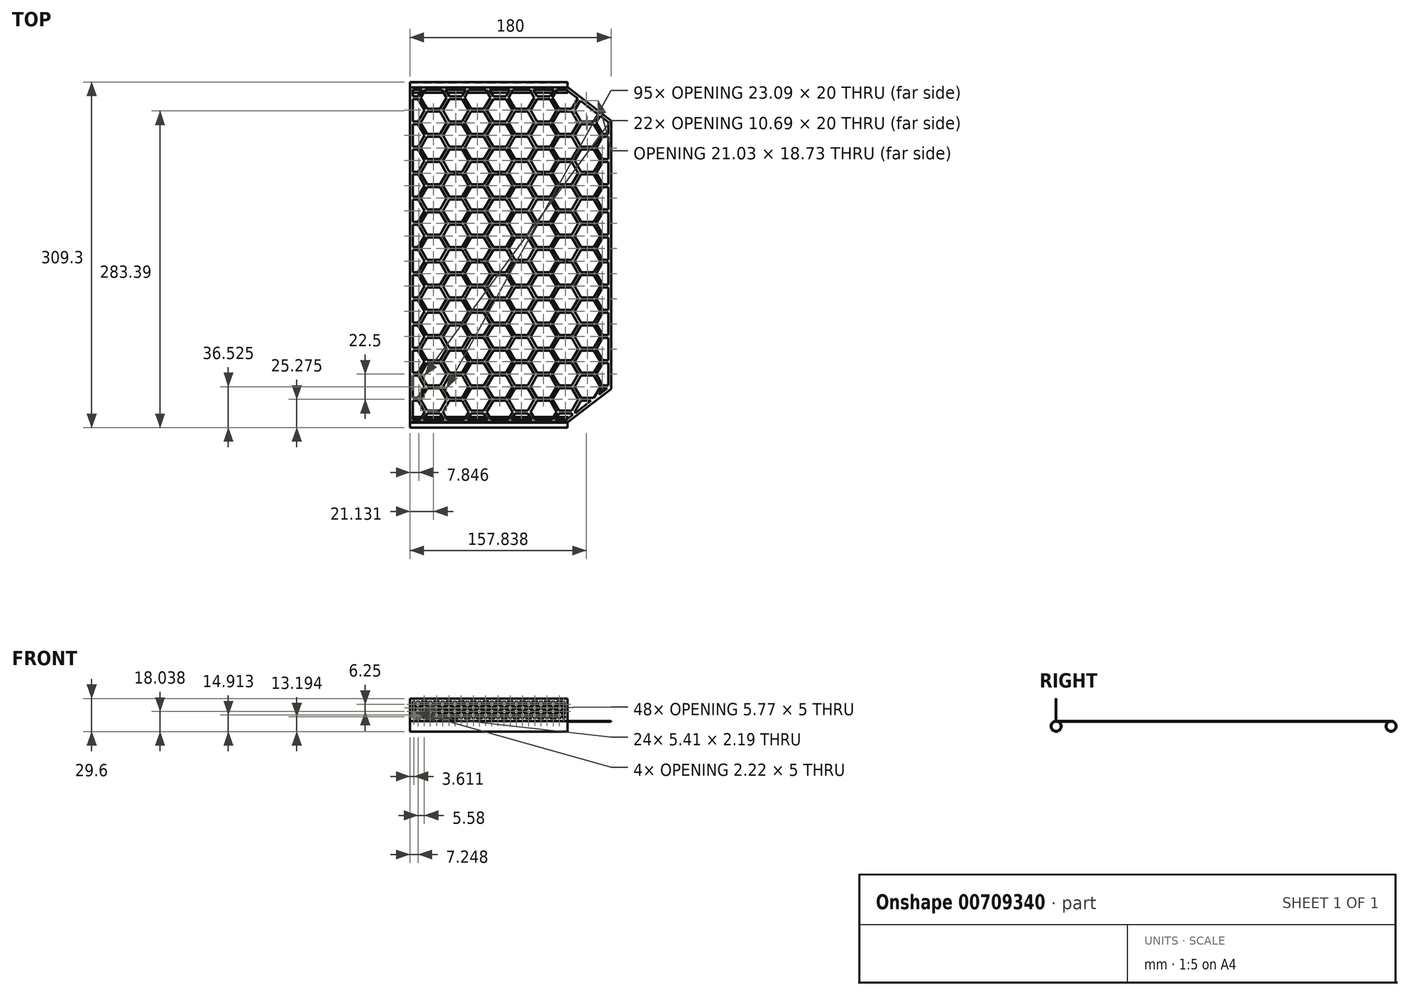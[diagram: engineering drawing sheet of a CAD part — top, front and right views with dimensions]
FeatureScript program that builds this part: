
annotation { "Feature Type Name" : "Feature", "Feature Type Description" : "" }
export const myFeature = defineFeature(function(context is Context, id is Id, definition is map)
    precondition{}
    {
        {
            var Q0;
            Q0=qCreatedBy(makeId("Top.planeOp"),FACE);
            var sketch = newSketch(context, id + "F0", { "sketchPlane" : qUnion([Q0])});
            skLineSegment(sketch, "E0.bottom", {"start": v(90, -150) * mm, "end": v(-90, -150) * mm});
            skLineSegment(sketch, "E0.top", {"start": v(90, 150) * mm, "end": v(-90, 150) * mm});
            skLineSegment(sketch, "E0.left", {"start": v(90, -150) * mm, "end": v(90, 150) * mm});
            skLineSegment(sketch, "E0.right", {"start": v(-90, -150) * mm, "end": v(-90, 150) * mm});
            skPoint(sketch, "E0.middle", {"position": v(0, 0) * mm});
            skLineSegment(sketch, "E1", {"start": v(90, -120) * mm, "end": v(51, -150) * mm});
            skLineSegment(sketch, "E2", {"start": v(51, 150) * mm, "end": v(90, 120) * mm});
            skSolve(sketch);
        }
        {
            var Q0;
            {var subQ0=sQuery(id+"F0.wireOp",EDGE,"E0.right");Q0=makeQuery(id+"F0.imprint","IMPRINT",FACE,{"disambiguationData":[TD([[makeQuery(id+"F0.imprint","IMPRINT",EDGE,{"derivedFrom":subQ0}),-1.0]])]});}
            extrude(context, id + "F1", {"entities" : qUnion([Q0]), "endBound" : BoundingType.SYMMETRIC, "depth" : 0.6 * mm, "offsetDistance" : 25 * mm});
        }
        {
            var Q0;
            Q0=qCreatedBy(makeId("Right.planeOp"),FACE);
            var sketch = newSketch(context, id + "F2", { "sketchPlane" : qUnion([Q0])});
            skCircle(sketch, "E3", {"center": v(-149.85, -4.5) * mm, "radius": 4.2 * mm});
            skCircle(sketch, "E4", {"center": v(-149.85, -4.5) * mm, "radius": 4.8 * mm});
            skCircle(sketch, "E5.MirrorC", {"center": v(149.85, -4.5) * mm, "radius": 4.8 * mm});
            skCircle(sketch, "E6.MirrorC", {"center": v(149.85, -4.5) * mm, "radius": 4.2 * mm});
            skLineSegment(sketch, "E7.bottom", {"start": v(-150.3, 0.3) * mm, "end": v(-149.7, 0.3) * mm});
            skLineSegment(sketch, "E7.top", {"start": v(-150.3, 20.3) * mm, "end": v(-149.7, 20.3) * mm});
            skLineSegment(sketch, "E7.left", {"start": v(-150.3, 0.3) * mm, "end": v(-150.3, 20.3) * mm});
            skLineSegment(sketch, "E7.right", {"start": v(-149.7, 0.3) * mm, "end": v(-149.7, 20.3) * mm});
            skPoint(sketch, "E8", {"position": v(-150, 0.3) * mm});
            skLineSegment(sketch, "E9.0.1", {"start": v(-150, -0.3) * mm, "end": v(-150, 0.3) * mm});
            skLineSegment(sketch, "E9.0.3", {"start": v(-150, 0.3) * mm, "end": v(-150, -0.3) * mm, "construction": true});
            skSolve(sketch);
        }
        {
            var Q0;
            Q0=qSketchRegion(id+"F2",true);
            var Q1;
            Q1=makeQuery(id+"F1.opExtrude","CAP_EDGE",EDGE,{"disambiguationData":[OSD([sQuery(id+"F0.wireOp",EDGE,"E0.bottom")])],"isStart":false});
            sweep(context, id + "F3", {"operationType" : NewBodyOperationType.ADD, "profiles" : qUnion([Q0]), "path" : qUnion([Q1])});
        }
        {
            var Q0;
            Q0=makeQuery(id+"F1.opExtrude","CAP_FACE",FACE,{"disambiguationData":[OSD([sQuery(id+"F0.wireOp",EDGE,"E0.bottom"),sQuery(id+"F0.wireOp",EDGE,"E0.top"),sQuery(id+"F0.wireOp",EDGE,"E0.left"),sQuery(id+"F0.wireOp",EDGE,"E0.right")])],"isStart":false});
            var sketch = newSketch(context, id + "F4", { "sketchPlane" : qUnion([Q0])});
            skPoint(sketch, "E10.0", {"position": v(-90, 147.52) * mm});
            skPoint(sketch, "E11.0", {"position": v(-90, -147.52) * mm});
            skLineSegment(sketch, "E12", {"start": v(-90, 147.52) * mm, "end": v(90, 147.52) * mm});
            skLineSegment(sketch, "E13", {"start": v(-90, -147.52) * mm, "end": v(90, -147.52) * mm});
            skCircle(sketch, "E14.cCircle", {"center": v(-68.87, 163.12) * mm, "radius": 10 * mm, "construction": true});
            skLineSegment(sketch, "E14.0", {"start": v(-63.1, 153.12) * mm, "end": v(-74.64, 153.12) * mm});
            skLineSegment(sketch, "E14.1", {"start": v(-74.64, 153.12) * mm, "end": v(-80.42, 163.12) * mm});
            skLineSegment(sketch, "E14.2", {"start": v(-80.42, 163.12) * mm, "end": v(-74.64, 173.12) * mm});
            skLineSegment(sketch, "E14.3", {"start": v(-74.64, 173.12) * mm, "end": v(-63.1, 173.12) * mm});
            skLineSegment(sketch, "E14.4", {"start": v(-63.1, 173.12) * mm, "end": v(-57.32, 163.12) * mm});
            skLineSegment(sketch, "E14.5", {"start": v(-57.32, 163.12) * mm, "end": v(-63.1, 153.12) * mm});
            skPoint(sketch, "E14.0.midPoint", {"position": v(-68.87, 153.12) * mm});
            skCircle(sketch, "E15.cCircle", {"center": v(-88.35, 151.87) * mm, "radius": 10 * mm, "construction": true});
            skLineSegment(sketch, "E15.0", {"start": v(-82.58, 141.87) * mm, "end": v(-94.13, 141.87) * mm});
            skLineSegment(sketch, "E15.1", {"start": v(-94.13, 141.87) * mm, "end": v(-99.9, 151.87) * mm});
            skLineSegment(sketch, "E15.2", {"start": v(-99.9, 151.87) * mm, "end": v(-94.13, 161.87) * mm});
            skLineSegment(sketch, "E15.3", {"start": v(-94.13, 161.87) * mm, "end": v(-82.58, 161.87) * mm});
            skLineSegment(sketch, "E15.4", {"start": v(-82.58, 161.87) * mm, "end": v(-76.8, 151.87) * mm});
            skLineSegment(sketch, "E15.5", {"start": v(-76.8, 151.87) * mm, "end": v(-82.58, 141.87) * mm});
            skPoint(sketch, "E15.0.midPoint", {"position": v(-88.35, 141.87) * mm});
            skLineSegment(sketch, "E16.0", {"start": v(87.5, -149.7) * mm, "end": v(87.5, 149.7) * mm});
            skLineSegment(sketch, "E17.0", {"start": v(-87.5, -149.7) * mm, "end": v(-87.5, 149.7) * mm});
            skLineSegment(sketch, "E18", {"start": v(0, 147.52) * mm, "end": v(0, -147.52) * mm, "construction": true});
            skLineSegment(sketch, "E19", {"start": v(-87.5, 0) * mm, "end": v(87.5, 0) * mm, "construction": true});
            skLineSegment(sketch, "E20.0.1.0", {"start": v(-94.13, 139.37) * mm, "end": v(-82.58, 139.37) * mm});
            skLineSegment(sketch, "E20.0.1.1", {"start": v(-99.9, 129.37) * mm, "end": v(-94.13, 139.37) * mm});
            skLineSegment(sketch, "E20.0.1.2", {"start": v(-94.13, 119.37) * mm, "end": v(-99.9, 129.37) * mm});
            skLineSegment(sketch, "E20.0.1.3", {"start": v(-82.58, 119.37) * mm, "end": v(-94.13, 119.37) * mm});
            skLineSegment(sketch, "E20.0.1.4", {"start": v(-76.8, 129.37) * mm, "end": v(-82.58, 119.37) * mm});
            skLineSegment(sketch, "E20.0.1.5", {"start": v(-82.58, 139.37) * mm, "end": v(-76.8, 129.37) * mm});
            skLineSegment(sketch, "E20.0.1.6", {"start": v(-80.42, 140.62) * mm, "end": v(-74.64, 150.62) * mm});
            skLineSegment(sketch, "E20.0.1.7", {"start": v(-74.64, 130.62) * mm, "end": v(-80.42, 140.62) * mm});
            skLineSegment(sketch, "E20.0.1.8", {"start": v(-74.64, 150.62) * mm, "end": v(-63.1, 150.62) * mm});
            skLineSegment(sketch, "E20.0.1.9", {"start": v(-63.1, 150.62) * mm, "end": v(-57.32, 140.62) * mm});
            skLineSegment(sketch, "E20.0.1.10", {"start": v(-57.32, 140.62) * mm, "end": v(-63.1, 130.62) * mm});
            skLineSegment(sketch, "E20.0.1.11", {"start": v(-63.1, 130.62) * mm, "end": v(-74.64, 130.62) * mm});
            skLineSegment(sketch, "E20.1.0.0", {"start": v(-54.82, 161.87) * mm, "end": v(-43.28, 161.87) * mm});
            skLineSegment(sketch, "E20.1.0.1", {"start": v(-60.6, 151.87) * mm, "end": v(-54.82, 161.87) * mm});
            skLineSegment(sketch, "E20.1.0.2", {"start": v(-54.82, 141.87) * mm, "end": v(-60.6, 151.87) * mm});
            skLineSegment(sketch, "E20.1.0.3", {"start": v(-43.28, 141.87) * mm, "end": v(-54.82, 141.87) * mm});
            skLineSegment(sketch, "E20.1.0.4", {"start": v(-37.5, 151.87) * mm, "end": v(-43.28, 141.87) * mm});
            skLineSegment(sketch, "E20.1.0.5", {"start": v(-43.28, 161.87) * mm, "end": v(-37.5, 151.87) * mm});
            skLineSegment(sketch, "E20.1.0.6", {"start": v(-41.11, 163.12) * mm, "end": v(-35.34, 173.12) * mm});
            skLineSegment(sketch, "E20.1.0.7", {"start": v(-35.34, 153.12) * mm, "end": v(-41.11, 163.12) * mm});
            skLineSegment(sketch, "E20.1.0.8", {"start": v(-35.34, 173.12) * mm, "end": v(-23.79, 173.12) * mm});
            skLineSegment(sketch, "E20.1.0.9", {"start": v(-23.79, 173.12) * mm, "end": v(-18.02, 163.12) * mm});
            skLineSegment(sketch, "E20.1.0.10", {"start": v(-18.02, 163.12) * mm, "end": v(-23.79, 153.12) * mm});
            skLineSegment(sketch, "E20.1.0.11", {"start": v(-23.79, 153.12) * mm, "end": v(-35.34, 153.12) * mm});
            skLineSegment(sketch, "E20.1.1.0", {"start": v(-54.82, 139.37) * mm, "end": v(-43.28, 139.37) * mm});
            skLineSegment(sketch, "E20.1.1.1", {"start": v(-60.6, 129.37) * mm, "end": v(-54.82, 139.37) * mm});
            skLineSegment(sketch, "E20.1.1.2", {"start": v(-54.82, 119.37) * mm, "end": v(-60.6, 129.37) * mm});
            skLineSegment(sketch, "E20.1.1.3", {"start": v(-43.28, 119.37) * mm, "end": v(-54.82, 119.37) * mm});
            skLineSegment(sketch, "E20.1.1.4", {"start": v(-37.5, 129.37) * mm, "end": v(-43.28, 119.37) * mm});
            skLineSegment(sketch, "E20.1.1.5", {"start": v(-43.28, 139.37) * mm, "end": v(-37.5, 129.37) * mm});
            skLineSegment(sketch, "E20.1.1.6", {"start": v(-41.11, 140.62) * mm, "end": v(-35.34, 150.62) * mm});
            skLineSegment(sketch, "E20.1.1.7", {"start": v(-35.34, 130.62) * mm, "end": v(-41.11, 140.62) * mm});
            skLineSegment(sketch, "E20.1.1.8", {"start": v(-35.34, 150.62) * mm, "end": v(-23.79, 150.62) * mm});
            skLineSegment(sketch, "E20.1.1.9", {"start": v(-23.79, 150.62) * mm, "end": v(-18.02, 140.62) * mm});
            skLineSegment(sketch, "E20.1.1.10", {"start": v(-18.02, 140.62) * mm, "end": v(-23.79, 130.62) * mm});
            skLineSegment(sketch, "E20.1.1.11", {"start": v(-23.79, 130.62) * mm, "end": v(-35.34, 130.62) * mm});
            skLineSegment(sketch, "E20.2.0.0", {"start": v(-15.52, 161.87) * mm, "end": v(-3.97, 161.87) * mm});
            skLineSegment(sketch, "E20.2.0.1", {"start": v(-21.29, 151.87) * mm, "end": v(-15.52, 161.87) * mm});
            skLineSegment(sketch, "E20.2.0.2", {"start": v(-15.52, 141.87) * mm, "end": v(-21.29, 151.87) * mm});
            skLineSegment(sketch, "E20.2.0.3", {"start": v(-3.97, 141.87) * mm, "end": v(-15.52, 141.87) * mm});
            skLineSegment(sketch, "E20.2.0.4", {"start": v(1.8, 151.87) * mm, "end": v(-3.97, 141.87) * mm});
            skLineSegment(sketch, "E20.2.0.5", {"start": v(-3.97, 161.87) * mm, "end": v(1.8, 151.87) * mm});
            skLineSegment(sketch, "E20.2.0.6", {"start": v(-1.8, 163.12) * mm, "end": v(3.97, 173.12) * mm});
            skLineSegment(sketch, "E20.2.0.7", {"start": v(3.97, 153.12) * mm, "end": v(-1.8, 163.12) * mm});
            skLineSegment(sketch, "E20.2.0.8", {"start": v(3.97, 173.12) * mm, "end": v(15.52, 173.12) * mm});
            skLineSegment(sketch, "E20.2.0.9", {"start": v(15.52, 173.12) * mm, "end": v(21.29, 163.12) * mm});
            skLineSegment(sketch, "E20.2.0.10", {"start": v(21.29, 163.12) * mm, "end": v(15.52, 153.12) * mm});
            skLineSegment(sketch, "E20.2.0.11", {"start": v(15.52, 153.12) * mm, "end": v(3.97, 153.12) * mm});
            skLineSegment(sketch, "E20.2.1.0", {"start": v(-15.52, 139.37) * mm, "end": v(-3.97, 139.37) * mm});
            skLineSegment(sketch, "E20.2.1.1", {"start": v(-21.29, 129.37) * mm, "end": v(-15.52, 139.37) * mm});
            skLineSegment(sketch, "E20.2.1.2", {"start": v(-15.52, 119.37) * mm, "end": v(-21.29, 129.37) * mm});
            skLineSegment(sketch, "E20.2.1.3", {"start": v(-3.97, 119.37) * mm, "end": v(-15.52, 119.37) * mm});
            skLineSegment(sketch, "E20.2.1.4", {"start": v(1.8, 129.37) * mm, "end": v(-3.97, 119.37) * mm});
            skLineSegment(sketch, "E20.2.1.5", {"start": v(-3.97, 139.37) * mm, "end": v(1.8, 129.37) * mm});
            skLineSegment(sketch, "E20.2.1.6", {"start": v(-1.8, 140.62) * mm, "end": v(3.97, 150.62) * mm});
            skLineSegment(sketch, "E20.2.1.7", {"start": v(3.97, 130.62) * mm, "end": v(-1.8, 140.62) * mm});
            skLineSegment(sketch, "E20.2.1.8", {"start": v(3.97, 150.62) * mm, "end": v(15.52, 150.62) * mm});
            skLineSegment(sketch, "E20.2.1.9", {"start": v(15.52, 150.62) * mm, "end": v(21.29, 140.62) * mm});
            skLineSegment(sketch, "E20.2.1.10", {"start": v(21.29, 140.62) * mm, "end": v(15.52, 130.62) * mm});
            skLineSegment(sketch, "E20.2.1.11", {"start": v(15.52, 130.62) * mm, "end": v(3.97, 130.62) * mm});
            skLineSegment(sketch, "E20.direction1", {"start": v(-94.13, 161.87) * mm, "end": v(-54.82, 161.87) * mm, "construction": true});
            skLineSegment(sketch, "E20.direction2", {"start": v(-94.13, 161.87) * mm, "end": v(-94.13, 139.37) * mm, "construction": true});
            skLineSegment(sketch, "E21.0.3.0", {"start": v(23.79, 161.87) * mm, "end": v(35.34, 161.87) * mm});
            skLineSegment(sketch, "E21.3.3.0", {"start": v(18.02, 151.87) * mm, "end": v(23.79, 161.87) * mm});
            skLineSegment(sketch, "E21.6.3.0", {"start": v(23.79, 141.87) * mm, "end": v(18.02, 151.87) * mm});
            skLineSegment(sketch, "E21.9.3.0", {"start": v(35.34, 141.87) * mm, "end": v(23.79, 141.87) * mm});
            skLineSegment(sketch, "E21.12.3.0", {"start": v(41.11, 151.87) * mm, "end": v(35.34, 141.87) * mm});
            skLineSegment(sketch, "E21.15.3.0", {"start": v(35.34, 161.87) * mm, "end": v(41.11, 151.87) * mm});
            skLineSegment(sketch, "E21.18.3.0", {"start": v(37.5, 163.12) * mm, "end": v(43.28, 173.12) * mm});
            skLineSegment(sketch, "E21.21.3.0", {"start": v(43.28, 153.12) * mm, "end": v(37.5, 163.12) * mm});
            skLineSegment(sketch, "E21.24.3.0", {"start": v(43.28, 173.12) * mm, "end": v(54.82, 173.12) * mm});
            skLineSegment(sketch, "E21.27.3.0", {"start": v(54.82, 173.12) * mm, "end": v(60.6, 163.12) * mm});
            skLineSegment(sketch, "E21.30.3.0", {"start": v(60.6, 163.12) * mm, "end": v(54.82, 153.12) * mm});
            skLineSegment(sketch, "E21.33.3.0", {"start": v(54.82, 153.12) * mm, "end": v(43.28, 153.12) * mm});
            skLineSegment(sketch, "E21.0.3.1", {"start": v(23.79, 139.37) * mm, "end": v(35.34, 139.37) * mm});
            skLineSegment(sketch, "E21.3.3.1", {"start": v(18.02, 129.37) * mm, "end": v(23.79, 139.37) * mm});
            skLineSegment(sketch, "E21.6.3.1", {"start": v(23.79, 119.37) * mm, "end": v(18.02, 129.37) * mm});
            skLineSegment(sketch, "E21.9.3.1", {"start": v(35.34, 119.37) * mm, "end": v(23.79, 119.37) * mm});
            skLineSegment(sketch, "E21.12.3.1", {"start": v(41.11, 129.37) * mm, "end": v(35.34, 119.37) * mm});
            skLineSegment(sketch, "E21.15.3.1", {"start": v(35.34, 139.37) * mm, "end": v(41.11, 129.37) * mm});
            skLineSegment(sketch, "E21.18.3.1", {"start": v(37.5, 140.62) * mm, "end": v(43.28, 150.62) * mm});
            skLineSegment(sketch, "E21.21.3.1", {"start": v(43.28, 130.62) * mm, "end": v(37.5, 140.62) * mm});
            skLineSegment(sketch, "E21.24.3.1", {"start": v(43.28, 150.62) * mm, "end": v(54.82, 150.62) * mm});
            skLineSegment(sketch, "E21.27.3.1", {"start": v(54.82, 150.62) * mm, "end": v(60.6, 140.62) * mm});
            skLineSegment(sketch, "E21.30.3.1", {"start": v(60.6, 140.62) * mm, "end": v(54.82, 130.62) * mm});
            skLineSegment(sketch, "E21.33.3.1", {"start": v(54.82, 130.62) * mm, "end": v(43.28, 130.62) * mm});
            skLineSegment(sketch, "E21.0.4.0", {"start": v(63.1, 161.87) * mm, "end": v(74.64, 161.87) * mm});
            skLineSegment(sketch, "E21.3.4.0", {"start": v(57.32, 151.87) * mm, "end": v(63.1, 161.87) * mm});
            skLineSegment(sketch, "E21.6.4.0", {"start": v(63.1, 141.87) * mm, "end": v(57.32, 151.87) * mm});
            skLineSegment(sketch, "E21.9.4.0", {"start": v(74.64, 141.87) * mm, "end": v(63.1, 141.87) * mm});
            skLineSegment(sketch, "E21.12.4.0", {"start": v(80.42, 151.87) * mm, "end": v(74.64, 141.87) * mm});
            skLineSegment(sketch, "E21.15.4.0", {"start": v(74.64, 161.87) * mm, "end": v(80.42, 151.87) * mm});
            skLineSegment(sketch, "E21.18.4.0", {"start": v(76.8, 163.12) * mm, "end": v(82.58, 173.12) * mm});
            skLineSegment(sketch, "E21.21.4.0", {"start": v(82.58, 153.12) * mm, "end": v(76.8, 163.12) * mm});
            skLineSegment(sketch, "E21.24.4.0", {"start": v(82.58, 173.12) * mm, "end": v(94.13, 173.12) * mm});
            skLineSegment(sketch, "E21.27.4.0", {"start": v(94.13, 173.12) * mm, "end": v(99.9, 163.12) * mm});
            skLineSegment(sketch, "E21.30.4.0", {"start": v(99.9, 163.12) * mm, "end": v(94.13, 153.12) * mm});
            skLineSegment(sketch, "E21.33.4.0", {"start": v(94.13, 153.12) * mm, "end": v(82.58, 153.12) * mm});
            skLineSegment(sketch, "E21.0.4.1", {"start": v(63.1, 139.37) * mm, "end": v(74.64, 139.37) * mm});
            skLineSegment(sketch, "E21.3.4.1", {"start": v(57.32, 129.37) * mm, "end": v(63.1, 139.37) * mm});
            skLineSegment(sketch, "E21.6.4.1", {"start": v(63.1, 119.37) * mm, "end": v(57.32, 129.37) * mm});
            skLineSegment(sketch, "E21.9.4.1", {"start": v(74.64, 119.37) * mm, "end": v(63.1, 119.37) * mm});
            skLineSegment(sketch, "E21.12.4.1", {"start": v(80.42, 129.37) * mm, "end": v(74.64, 119.37) * mm});
            skLineSegment(sketch, "E21.15.4.1", {"start": v(74.64, 139.37) * mm, "end": v(80.42, 129.37) * mm});
            skLineSegment(sketch, "E21.18.4.1", {"start": v(76.8, 140.62) * mm, "end": v(82.58, 150.62) * mm});
            skLineSegment(sketch, "E21.21.4.1", {"start": v(82.58, 130.62) * mm, "end": v(76.8, 140.62) * mm});
            skLineSegment(sketch, "E21.24.4.1", {"start": v(82.58, 150.62) * mm, "end": v(94.13, 150.62) * mm});
            skLineSegment(sketch, "E21.27.4.1", {"start": v(94.13, 150.62) * mm, "end": v(99.9, 140.62) * mm});
            skLineSegment(sketch, "E21.30.4.1", {"start": v(99.9, 140.62) * mm, "end": v(94.13, 130.62) * mm});
            skLineSegment(sketch, "E21.33.4.1", {"start": v(94.13, 130.62) * mm, "end": v(82.58, 130.62) * mm});
            skLineSegment(sketch, "E22.0.0.2", {"start": v(-94.13, 116.87) * mm, "end": v(-82.58, 116.87) * mm});
            skLineSegment(sketch, "E22.3.0.2", {"start": v(-99.9, 106.87) * mm, "end": v(-94.13, 116.87) * mm});
            skLineSegment(sketch, "E22.6.0.2", {"start": v(-94.13, 96.87) * mm, "end": v(-99.9, 106.87) * mm});
            skLineSegment(sketch, "E22.9.0.2", {"start": v(-82.58, 96.87) * mm, "end": v(-94.13, 96.87) * mm});
            skLineSegment(sketch, "E22.12.0.2", {"start": v(-76.8, 106.87) * mm, "end": v(-82.58, 96.87) * mm});
            skLineSegment(sketch, "E22.15.0.2", {"start": v(-82.58, 116.87) * mm, "end": v(-76.8, 106.87) * mm});
            skLineSegment(sketch, "E22.18.0.2", {"start": v(-80.42, 118.12) * mm, "end": v(-74.64, 128.12) * mm});
            skLineSegment(sketch, "E22.21.0.2", {"start": v(-74.64, 108.12) * mm, "end": v(-80.42, 118.12) * mm});
            skLineSegment(sketch, "E22.24.0.2", {"start": v(-74.64, 128.12) * mm, "end": v(-63.1, 128.12) * mm});
            skLineSegment(sketch, "E22.27.0.2", {"start": v(-63.1, 128.12) * mm, "end": v(-57.32, 118.12) * mm});
            skLineSegment(sketch, "E22.30.0.2", {"start": v(-57.32, 118.12) * mm, "end": v(-63.1, 108.12) * mm});
            skLineSegment(sketch, "E22.33.0.2", {"start": v(-63.1, 108.12) * mm, "end": v(-74.64, 108.12) * mm});
            skLineSegment(sketch, "E22.0.0.3", {"start": v(-94.13, 94.37) * mm, "end": v(-82.58, 94.37) * mm});
            skLineSegment(sketch, "E22.3.0.3", {"start": v(-99.9, 84.37) * mm, "end": v(-94.13, 94.37) * mm});
            skLineSegment(sketch, "E22.6.0.3", {"start": v(-94.13, 74.37) * mm, "end": v(-99.9, 84.37) * mm});
            skLineSegment(sketch, "E22.9.0.3", {"start": v(-82.58, 74.37) * mm, "end": v(-94.13, 74.37) * mm});
            skLineSegment(sketch, "E22.12.0.3", {"start": v(-76.8, 84.37) * mm, "end": v(-82.58, 74.37) * mm});
            skLineSegment(sketch, "E22.15.0.3", {"start": v(-82.58, 94.37) * mm, "end": v(-76.8, 84.37) * mm});
            skLineSegment(sketch, "E22.18.0.3", {"start": v(-80.42, 95.62) * mm, "end": v(-74.64, 105.62) * mm});
            skLineSegment(sketch, "E22.21.0.3", {"start": v(-74.64, 85.62) * mm, "end": v(-80.42, 95.62) * mm});
            skLineSegment(sketch, "E22.24.0.3", {"start": v(-74.64, 105.62) * mm, "end": v(-63.1, 105.62) * mm});
            skLineSegment(sketch, "E22.27.0.3", {"start": v(-63.1, 105.62) * mm, "end": v(-57.32, 95.62) * mm});
            skLineSegment(sketch, "E22.30.0.3", {"start": v(-57.32, 95.62) * mm, "end": v(-63.1, 85.62) * mm});
            skLineSegment(sketch, "E22.33.0.3", {"start": v(-63.1, 85.62) * mm, "end": v(-74.64, 85.62) * mm});
            skLineSegment(sketch, "E22.0.0.4", {"start": v(-94.13, 71.87) * mm, "end": v(-82.58, 71.87) * mm});
            skLineSegment(sketch, "E22.3.0.4", {"start": v(-99.9, 61.87) * mm, "end": v(-94.13, 71.87) * mm});
            skLineSegment(sketch, "E22.6.0.4", {"start": v(-94.13, 51.87) * mm, "end": v(-99.9, 61.87) * mm});
            skLineSegment(sketch, "E22.9.0.4", {"start": v(-82.58, 51.87) * mm, "end": v(-94.13, 51.87) * mm});
            skLineSegment(sketch, "E22.12.0.4", {"start": v(-76.8, 61.87) * mm, "end": v(-82.58, 51.87) * mm});
            skLineSegment(sketch, "E22.15.0.4", {"start": v(-82.58, 71.87) * mm, "end": v(-76.8, 61.87) * mm});
            skLineSegment(sketch, "E22.18.0.4", {"start": v(-80.42, 73.12) * mm, "end": v(-74.64, 83.12) * mm});
            skLineSegment(sketch, "E22.21.0.4", {"start": v(-74.64, 63.12) * mm, "end": v(-80.42, 73.12) * mm});
            skLineSegment(sketch, "E22.24.0.4", {"start": v(-74.64, 83.12) * mm, "end": v(-63.1, 83.12) * mm});
            skLineSegment(sketch, "E22.27.0.4", {"start": v(-63.1, 83.12) * mm, "end": v(-57.32, 73.12) * mm});
            skLineSegment(sketch, "E22.30.0.4", {"start": v(-57.32, 73.12) * mm, "end": v(-63.1, 63.12) * mm});
            skLineSegment(sketch, "E22.33.0.4", {"start": v(-63.1, 63.12) * mm, "end": v(-74.64, 63.12) * mm});
            skLineSegment(sketch, "E22.0.0.5", {"start": v(-94.13, 49.37) * mm, "end": v(-82.58, 49.37) * mm});
            skLineSegment(sketch, "E22.3.0.5", {"start": v(-99.9, 39.37) * mm, "end": v(-94.13, 49.37) * mm});
            skLineSegment(sketch, "E22.6.0.5", {"start": v(-94.13, 29.37) * mm, "end": v(-99.9, 39.37) * mm});
            skLineSegment(sketch, "E22.9.0.5", {"start": v(-82.58, 29.37) * mm, "end": v(-94.13, 29.37) * mm});
            skLineSegment(sketch, "E22.12.0.5", {"start": v(-76.8, 39.37) * mm, "end": v(-82.58, 29.37) * mm});
            skLineSegment(sketch, "E22.15.0.5", {"start": v(-82.58, 49.37) * mm, "end": v(-76.8, 39.37) * mm});
            skLineSegment(sketch, "E22.18.0.5", {"start": v(-80.42, 50.62) * mm, "end": v(-74.64, 60.62) * mm});
            skLineSegment(sketch, "E22.21.0.5", {"start": v(-74.64, 40.62) * mm, "end": v(-80.42, 50.62) * mm});
            skLineSegment(sketch, "E22.24.0.5", {"start": v(-74.64, 60.62) * mm, "end": v(-63.1, 60.62) * mm});
            skLineSegment(sketch, "E22.27.0.5", {"start": v(-63.1, 60.62) * mm, "end": v(-57.32, 50.62) * mm});
            skLineSegment(sketch, "E22.30.0.5", {"start": v(-57.32, 50.62) * mm, "end": v(-63.1, 40.62) * mm});
            skLineSegment(sketch, "E22.33.0.5", {"start": v(-63.1, 40.62) * mm, "end": v(-74.64, 40.62) * mm});
            skLineSegment(sketch, "E22.0.0.6", {"start": v(-94.13, 26.87) * mm, "end": v(-82.58, 26.87) * mm});
            skLineSegment(sketch, "E22.3.0.6", {"start": v(-99.9, 16.87) * mm, "end": v(-94.13, 26.87) * mm});
            skLineSegment(sketch, "E22.6.0.6", {"start": v(-94.13, 6.87) * mm, "end": v(-99.9, 16.87) * mm});
            skLineSegment(sketch, "E22.9.0.6", {"start": v(-82.58, 6.87) * mm, "end": v(-94.13, 6.87) * mm});
            skLineSegment(sketch, "E22.12.0.6", {"start": v(-76.8, 16.87) * mm, "end": v(-82.58, 6.87) * mm});
            skLineSegment(sketch, "E22.15.0.6", {"start": v(-82.58, 26.87) * mm, "end": v(-76.8, 16.87) * mm});
            skLineSegment(sketch, "E22.18.0.6", {"start": v(-80.42, 28.12) * mm, "end": v(-74.64, 38.12) * mm});
            skLineSegment(sketch, "E22.21.0.6", {"start": v(-74.64, 18.12) * mm, "end": v(-80.42, 28.12) * mm});
            skLineSegment(sketch, "E22.24.0.6", {"start": v(-74.64, 38.12) * mm, "end": v(-63.1, 38.12) * mm});
            skLineSegment(sketch, "E22.27.0.6", {"start": v(-63.1, 38.12) * mm, "end": v(-57.32, 28.12) * mm});
            skLineSegment(sketch, "E22.30.0.6", {"start": v(-57.32, 28.12) * mm, "end": v(-63.1, 18.12) * mm});
            skLineSegment(sketch, "E22.33.0.6", {"start": v(-63.1, 18.12) * mm, "end": v(-74.64, 18.12) * mm});
            skLineSegment(sketch, "E22.0.0.7", {"start": v(-94.13, 4.37) * mm, "end": v(-82.58, 4.37) * mm});
            skLineSegment(sketch, "E22.3.0.7", {"start": v(-99.9, -5.63) * mm, "end": v(-94.13, 4.37) * mm});
            skLineSegment(sketch, "E22.6.0.7", {"start": v(-94.13, -15.63) * mm, "end": v(-99.9, -5.63) * mm});
            skLineSegment(sketch, "E22.9.0.7", {"start": v(-82.58, -15.63) * mm, "end": v(-94.13, -15.63) * mm});
            skLineSegment(sketch, "E22.12.0.7", {"start": v(-76.8, -5.63) * mm, "end": v(-82.58, -15.63) * mm});
            skLineSegment(sketch, "E22.15.0.7", {"start": v(-82.58, 4.37) * mm, "end": v(-76.8, -5.63) * mm});
            skLineSegment(sketch, "E22.18.0.7", {"start": v(-80.42, 5.62) * mm, "end": v(-74.64, 15.62) * mm});
            skLineSegment(sketch, "E22.21.0.7", {"start": v(-74.64, -4.38) * mm, "end": v(-80.42, 5.62) * mm});
            skLineSegment(sketch, "E22.24.0.7", {"start": v(-74.64, 15.62) * mm, "end": v(-63.1, 15.62) * mm});
            skLineSegment(sketch, "E22.27.0.7", {"start": v(-63.1, 15.62) * mm, "end": v(-57.32, 5.62) * mm});
            skLineSegment(sketch, "E22.30.0.7", {"start": v(-57.32, 5.62) * mm, "end": v(-63.1, -4.38) * mm});
            skLineSegment(sketch, "E22.33.0.7", {"start": v(-63.1, -4.38) * mm, "end": v(-74.64, -4.38) * mm});
            skLineSegment(sketch, "E22.0.0.8", {"start": v(-94.13, -18.13) * mm, "end": v(-82.58, -18.13) * mm});
            skLineSegment(sketch, "E22.3.0.8", {"start": v(-99.9, -28.13) * mm, "end": v(-94.13, -18.13) * mm});
            skLineSegment(sketch, "E22.6.0.8", {"start": v(-94.13, -38.13) * mm, "end": v(-99.9, -28.13) * mm});
            skLineSegment(sketch, "E22.9.0.8", {"start": v(-82.58, -38.13) * mm, "end": v(-94.13, -38.13) * mm});
            skLineSegment(sketch, "E22.12.0.8", {"start": v(-76.8, -28.13) * mm, "end": v(-82.58, -38.13) * mm});
            skLineSegment(sketch, "E22.15.0.8", {"start": v(-82.58, -18.13) * mm, "end": v(-76.8, -28.13) * mm});
            skLineSegment(sketch, "E22.18.0.8", {"start": v(-80.42, -16.88) * mm, "end": v(-74.64, -6.88) * mm});
            skLineSegment(sketch, "E22.21.0.8", {"start": v(-74.64, -26.88) * mm, "end": v(-80.42, -16.88) * mm});
            skLineSegment(sketch, "E22.24.0.8", {"start": v(-74.64, -6.88) * mm, "end": v(-63.1, -6.88) * mm});
            skLineSegment(sketch, "E22.27.0.8", {"start": v(-63.1, -6.88) * mm, "end": v(-57.32, -16.88) * mm});
            skLineSegment(sketch, "E22.30.0.8", {"start": v(-57.32, -16.88) * mm, "end": v(-63.1, -26.88) * mm});
            skLineSegment(sketch, "E22.33.0.8", {"start": v(-63.1, -26.88) * mm, "end": v(-74.64, -26.88) * mm});
            skLineSegment(sketch, "E22.0.0.9", {"start": v(-94.13, -40.63) * mm, "end": v(-82.58, -40.63) * mm});
            skLineSegment(sketch, "E22.3.0.9", {"start": v(-99.9, -50.63) * mm, "end": v(-94.13, -40.63) * mm});
            skLineSegment(sketch, "E22.6.0.9", {"start": v(-94.13, -60.63) * mm, "end": v(-99.9, -50.63) * mm});
            skLineSegment(sketch, "E22.9.0.9", {"start": v(-82.58, -60.63) * mm, "end": v(-94.13, -60.63) * mm});
            skLineSegment(sketch, "E22.12.0.9", {"start": v(-76.8, -50.63) * mm, "end": v(-82.58, -60.63) * mm});
            skLineSegment(sketch, "E22.15.0.9", {"start": v(-82.58, -40.63) * mm, "end": v(-76.8, -50.63) * mm});
            skLineSegment(sketch, "E22.18.0.9", {"start": v(-80.42, -39.38) * mm, "end": v(-74.64, -29.38) * mm});
            skLineSegment(sketch, "E22.21.0.9", {"start": v(-74.64, -49.38) * mm, "end": v(-80.42, -39.38) * mm});
            skLineSegment(sketch, "E22.24.0.9", {"start": v(-74.64, -29.38) * mm, "end": v(-63.1, -29.38) * mm});
            skLineSegment(sketch, "E22.27.0.9", {"start": v(-63.1, -29.38) * mm, "end": v(-57.32, -39.38) * mm});
            skLineSegment(sketch, "E22.30.0.9", {"start": v(-57.32, -39.38) * mm, "end": v(-63.1, -49.38) * mm});
            skLineSegment(sketch, "E22.33.0.9", {"start": v(-63.1, -49.38) * mm, "end": v(-74.64, -49.38) * mm});
            skLineSegment(sketch, "E22.0.0.10", {"start": v(-94.13, -63.13) * mm, "end": v(-82.58, -63.13) * mm});
            skLineSegment(sketch, "E22.3.0.10", {"start": v(-99.9, -73.13) * mm, "end": v(-94.13, -63.13) * mm});
            skLineSegment(sketch, "E22.6.0.10", {"start": v(-94.13, -83.13) * mm, "end": v(-99.9, -73.13) * mm});
            skLineSegment(sketch, "E22.9.0.10", {"start": v(-82.58, -83.13) * mm, "end": v(-94.13, -83.13) * mm});
            skLineSegment(sketch, "E22.12.0.10", {"start": v(-76.8, -73.13) * mm, "end": v(-82.58, -83.13) * mm});
            skLineSegment(sketch, "E22.15.0.10", {"start": v(-82.58, -63.13) * mm, "end": v(-76.8, -73.13) * mm});
            skLineSegment(sketch, "E22.18.0.10", {"start": v(-80.42, -61.88) * mm, "end": v(-74.64, -51.88) * mm});
            skLineSegment(sketch, "E22.21.0.10", {"start": v(-74.64, -71.88) * mm, "end": v(-80.42, -61.88) * mm});
            skLineSegment(sketch, "E22.24.0.10", {"start": v(-74.64, -51.88) * mm, "end": v(-63.1, -51.88) * mm});
            skLineSegment(sketch, "E22.27.0.10", {"start": v(-63.1, -51.88) * mm, "end": v(-57.32, -61.88) * mm});
            skLineSegment(sketch, "E22.30.0.10", {"start": v(-57.32, -61.88) * mm, "end": v(-63.1, -71.88) * mm});
            skLineSegment(sketch, "E22.33.0.10", {"start": v(-63.1, -71.88) * mm, "end": v(-74.64, -71.88) * mm});
            skLineSegment(sketch, "E22.0.0.11", {"start": v(-94.13, -85.63) * mm, "end": v(-82.58, -85.63) * mm});
            skLineSegment(sketch, "E22.3.0.11", {"start": v(-99.9, -95.63) * mm, "end": v(-94.13, -85.63) * mm});
            skLineSegment(sketch, "E22.6.0.11", {"start": v(-94.13, -105.63) * mm, "end": v(-99.9, -95.63) * mm});
            skLineSegment(sketch, "E22.9.0.11", {"start": v(-82.58, -105.63) * mm, "end": v(-94.13, -105.63) * mm});
            skLineSegment(sketch, "E22.12.0.11", {"start": v(-76.8, -95.63) * mm, "end": v(-82.58, -105.63) * mm});
            skLineSegment(sketch, "E22.15.0.11", {"start": v(-82.58, -85.62) * mm, "end": v(-76.8, -95.63) * mm});
            skLineSegment(sketch, "E22.18.0.11", {"start": v(-80.42, -84.38) * mm, "end": v(-74.64, -74.38) * mm});
            skLineSegment(sketch, "E22.21.0.11", {"start": v(-74.64, -94.38) * mm, "end": v(-80.42, -84.38) * mm});
            skLineSegment(sketch, "E22.24.0.11", {"start": v(-74.64, -74.38) * mm, "end": v(-63.1, -74.38) * mm});
            skLineSegment(sketch, "E22.27.0.11", {"start": v(-63.1, -74.38) * mm, "end": v(-57.32, -84.38) * mm});
            skLineSegment(sketch, "E22.30.0.11", {"start": v(-57.32, -84.38) * mm, "end": v(-63.1, -94.38) * mm});
            skLineSegment(sketch, "E22.33.0.11", {"start": v(-63.1, -94.38) * mm, "end": v(-74.64, -94.38) * mm});
            skLineSegment(sketch, "E22.0.0.12", {"start": v(-94.13, -108.13) * mm, "end": v(-82.58, -108.13) * mm});
            skLineSegment(sketch, "E22.3.0.12", {"start": v(-99.9, -118.13) * mm, "end": v(-94.13, -108.13) * mm});
            skLineSegment(sketch, "E22.6.0.12", {"start": v(-94.13, -128.13) * mm, "end": v(-99.9, -118.13) * mm});
            skLineSegment(sketch, "E22.9.0.12", {"start": v(-82.58, -128.13) * mm, "end": v(-94.13, -128.13) * mm});
            skLineSegment(sketch, "E22.12.0.12", {"start": v(-76.8, -118.13) * mm, "end": v(-82.58, -128.13) * mm});
            skLineSegment(sketch, "E22.15.0.12", {"start": v(-82.58, -108.13) * mm, "end": v(-76.8, -118.13) * mm});
            skLineSegment(sketch, "E22.18.0.12", {"start": v(-80.42, -106.88) * mm, "end": v(-74.64, -96.88) * mm});
            skLineSegment(sketch, "E22.21.0.12", {"start": v(-74.64, -116.87) * mm, "end": v(-80.42, -106.88) * mm});
            skLineSegment(sketch, "E22.24.0.12", {"start": v(-74.64, -96.88) * mm, "end": v(-63.1, -96.88) * mm});
            skLineSegment(sketch, "E22.27.0.12", {"start": v(-63.1, -96.88) * mm, "end": v(-57.32, -106.88) * mm});
            skLineSegment(sketch, "E22.30.0.12", {"start": v(-57.32, -106.88) * mm, "end": v(-63.1, -116.88) * mm});
            skLineSegment(sketch, "E22.33.0.12", {"start": v(-63.1, -116.88) * mm, "end": v(-74.64, -116.88) * mm});
            skLineSegment(sketch, "E22.0.0.13", {"start": v(-94.13, -130.62) * mm, "end": v(-82.58, -130.62) * mm});
            skLineSegment(sketch, "E22.3.0.13", {"start": v(-99.9, -140.63) * mm, "end": v(-94.13, -130.63) * mm});
            skLineSegment(sketch, "E22.6.0.13", {"start": v(-94.13, -150.63) * mm, "end": v(-99.9, -140.63) * mm});
            skLineSegment(sketch, "E22.9.0.13", {"start": v(-82.58, -150.62) * mm, "end": v(-94.13, -150.62) * mm});
            skLineSegment(sketch, "E22.12.0.13", {"start": v(-76.8, -140.62) * mm, "end": v(-82.58, -150.62) * mm});
            skLineSegment(sketch, "E22.15.0.13", {"start": v(-82.58, -130.62) * mm, "end": v(-76.8, -140.62) * mm});
            skLineSegment(sketch, "E22.18.0.13", {"start": v(-80.42, -129.38) * mm, "end": v(-74.64, -119.38) * mm});
            skLineSegment(sketch, "E22.21.0.13", {"start": v(-74.64, -139.37) * mm, "end": v(-80.42, -129.38) * mm});
            skLineSegment(sketch, "E22.24.0.13", {"start": v(-74.64, -119.37) * mm, "end": v(-63.1, -119.37) * mm});
            skLineSegment(sketch, "E22.27.0.13", {"start": v(-63.1, -119.38) * mm, "end": v(-57.32, -129.37) * mm});
            skLineSegment(sketch, "E22.30.0.13", {"start": v(-57.32, -129.38) * mm, "end": v(-63.1, -139.38) * mm});
            skLineSegment(sketch, "E22.33.0.13", {"start": v(-63.1, -139.38) * mm, "end": v(-74.64, -139.38) * mm});
            skLineSegment(sketch, "E22.0.0.14", {"start": v(-94.13, -153.12) * mm, "end": v(-82.58, -153.12) * mm});
            skLineSegment(sketch, "E22.3.0.14", {"start": v(-99.9, -163.13) * mm, "end": v(-94.13, -153.13) * mm});
            skLineSegment(sketch, "E22.6.0.14", {"start": v(-94.13, -173.13) * mm, "end": v(-99.9, -163.13) * mm});
            skLineSegment(sketch, "E22.9.0.14", {"start": v(-82.58, -173.12) * mm, "end": v(-94.13, -173.12) * mm});
            skLineSegment(sketch, "E22.12.0.14", {"start": v(-76.8, -163.13) * mm, "end": v(-82.58, -173.12) * mm});
            skLineSegment(sketch, "E22.15.0.14", {"start": v(-82.58, -153.12) * mm, "end": v(-76.8, -163.12) * mm});
            skLineSegment(sketch, "E22.18.0.14", {"start": v(-80.42, -151.88) * mm, "end": v(-74.64, -141.88) * mm});
            skLineSegment(sketch, "E22.21.0.14", {"start": v(-74.64, -161.87) * mm, "end": v(-80.42, -151.88) * mm});
            skLineSegment(sketch, "E22.24.0.14", {"start": v(-74.64, -141.88) * mm, "end": v(-63.1, -141.88) * mm});
            skLineSegment(sketch, "E22.27.0.14", {"start": v(-63.1, -141.88) * mm, "end": v(-57.32, -151.87) * mm});
            skLineSegment(sketch, "E22.30.0.14", {"start": v(-57.32, -151.88) * mm, "end": v(-63.1, -161.88) * mm});
            skLineSegment(sketch, "E22.33.0.14", {"start": v(-63.1, -161.88) * mm, "end": v(-74.64, -161.88) * mm});
            skLineSegment(sketch, "E22.0.1.2", {"start": v(-54.82, 116.87) * mm, "end": v(-43.28, 116.87) * mm});
            skLineSegment(sketch, "E22.3.1.2", {"start": v(-60.6, 106.87) * mm, "end": v(-54.82, 116.87) * mm});
            skLineSegment(sketch, "E22.6.1.2", {"start": v(-54.82, 96.87) * mm, "end": v(-60.6, 106.87) * mm});
            skLineSegment(sketch, "E22.9.1.2", {"start": v(-43.28, 96.87) * mm, "end": v(-54.82, 96.87) * mm});
            skLineSegment(sketch, "E22.12.1.2", {"start": v(-37.5, 106.87) * mm, "end": v(-43.28, 96.87) * mm});
            skLineSegment(sketch, "E22.15.1.2", {"start": v(-43.28, 116.87) * mm, "end": v(-37.5, 106.87) * mm});
            skLineSegment(sketch, "E22.18.1.2", {"start": v(-41.11, 118.12) * mm, "end": v(-35.34, 128.12) * mm});
            skLineSegment(sketch, "E22.21.1.2", {"start": v(-35.34, 108.12) * mm, "end": v(-41.11, 118.12) * mm});
            skLineSegment(sketch, "E22.24.1.2", {"start": v(-35.34, 128.12) * mm, "end": v(-23.79, 128.12) * mm});
            skLineSegment(sketch, "E22.27.1.2", {"start": v(-23.79, 128.12) * mm, "end": v(-18.02, 118.12) * mm});
            skLineSegment(sketch, "E22.30.1.2", {"start": v(-18.02, 118.12) * mm, "end": v(-23.79, 108.12) * mm});
            skLineSegment(sketch, "E22.33.1.2", {"start": v(-23.79, 108.12) * mm, "end": v(-35.34, 108.12) * mm});
            skLineSegment(sketch, "E22.0.1.3", {"start": v(-54.82, 94.37) * mm, "end": v(-43.28, 94.37) * mm});
            skLineSegment(sketch, "E22.3.1.3", {"start": v(-60.6, 84.37) * mm, "end": v(-54.82, 94.37) * mm});
            skLineSegment(sketch, "E22.6.1.3", {"start": v(-54.82, 74.37) * mm, "end": v(-60.6, 84.37) * mm});
            skLineSegment(sketch, "E22.9.1.3", {"start": v(-43.28, 74.37) * mm, "end": v(-54.82, 74.37) * mm});
            skLineSegment(sketch, "E22.12.1.3", {"start": v(-37.5, 84.37) * mm, "end": v(-43.28, 74.37) * mm});
            skLineSegment(sketch, "E22.15.1.3", {"start": v(-43.28, 94.37) * mm, "end": v(-37.5, 84.37) * mm});
            skLineSegment(sketch, "E22.18.1.3", {"start": v(-41.11, 95.62) * mm, "end": v(-35.34, 105.62) * mm});
            skLineSegment(sketch, "E22.21.1.3", {"start": v(-35.34, 85.62) * mm, "end": v(-41.11, 95.62) * mm});
            skLineSegment(sketch, "E22.24.1.3", {"start": v(-35.34, 105.62) * mm, "end": v(-23.79, 105.62) * mm});
            skLineSegment(sketch, "E22.27.1.3", {"start": v(-23.79, 105.62) * mm, "end": v(-18.02, 95.62) * mm});
            skLineSegment(sketch, "E22.30.1.3", {"start": v(-18.02, 95.62) * mm, "end": v(-23.79, 85.62) * mm});
            skLineSegment(sketch, "E22.33.1.3", {"start": v(-23.79, 85.62) * mm, "end": v(-35.34, 85.62) * mm});
            skLineSegment(sketch, "E22.0.1.4", {"start": v(-54.82, 71.87) * mm, "end": v(-43.28, 71.87) * mm});
            skLineSegment(sketch, "E22.3.1.4", {"start": v(-60.6, 61.87) * mm, "end": v(-54.82, 71.87) * mm});
            skLineSegment(sketch, "E22.6.1.4", {"start": v(-54.82, 51.87) * mm, "end": v(-60.6, 61.87) * mm});
            skLineSegment(sketch, "E22.9.1.4", {"start": v(-43.28, 51.87) * mm, "end": v(-54.82, 51.87) * mm});
            skLineSegment(sketch, "E22.12.1.4", {"start": v(-37.5, 61.87) * mm, "end": v(-43.28, 51.87) * mm});
            skLineSegment(sketch, "E22.15.1.4", {"start": v(-43.28, 71.87) * mm, "end": v(-37.5, 61.87) * mm});
            skLineSegment(sketch, "E22.18.1.4", {"start": v(-41.11, 73.12) * mm, "end": v(-35.34, 83.12) * mm});
            skLineSegment(sketch, "E22.21.1.4", {"start": v(-35.34, 63.12) * mm, "end": v(-41.11, 73.12) * mm});
            skLineSegment(sketch, "E22.24.1.4", {"start": v(-35.34, 83.12) * mm, "end": v(-23.79, 83.12) * mm});
            skLineSegment(sketch, "E22.27.1.4", {"start": v(-23.79, 83.12) * mm, "end": v(-18.02, 73.12) * mm});
            skLineSegment(sketch, "E22.30.1.4", {"start": v(-18.02, 73.12) * mm, "end": v(-23.79, 63.12) * mm});
            skLineSegment(sketch, "E22.33.1.4", {"start": v(-23.79, 63.12) * mm, "end": v(-35.34, 63.12) * mm});
            skLineSegment(sketch, "E22.0.1.5", {"start": v(-54.82, 49.37) * mm, "end": v(-43.28, 49.37) * mm});
            skLineSegment(sketch, "E22.3.1.5", {"start": v(-60.6, 39.37) * mm, "end": v(-54.82, 49.37) * mm});
            skLineSegment(sketch, "E22.6.1.5", {"start": v(-54.82, 29.37) * mm, "end": v(-60.6, 39.37) * mm});
            skLineSegment(sketch, "E22.9.1.5", {"start": v(-43.28, 29.37) * mm, "end": v(-54.82, 29.37) * mm});
            skLineSegment(sketch, "E22.12.1.5", {"start": v(-37.5, 39.37) * mm, "end": v(-43.28, 29.37) * mm});
            skLineSegment(sketch, "E22.15.1.5", {"start": v(-43.28, 49.37) * mm, "end": v(-37.5, 39.37) * mm});
            skLineSegment(sketch, "E22.18.1.5", {"start": v(-41.11, 50.62) * mm, "end": v(-35.34, 60.62) * mm});
            skLineSegment(sketch, "E22.21.1.5", {"start": v(-35.34, 40.62) * mm, "end": v(-41.11, 50.62) * mm});
            skLineSegment(sketch, "E22.24.1.5", {"start": v(-35.34, 60.62) * mm, "end": v(-23.79, 60.62) * mm});
            skLineSegment(sketch, "E22.27.1.5", {"start": v(-23.79, 60.62) * mm, "end": v(-18.02, 50.62) * mm});
            skLineSegment(sketch, "E22.30.1.5", {"start": v(-18.02, 50.62) * mm, "end": v(-23.79, 40.62) * mm});
            skLineSegment(sketch, "E22.33.1.5", {"start": v(-23.79, 40.62) * mm, "end": v(-35.34, 40.62) * mm});
            skLineSegment(sketch, "E22.0.1.6", {"start": v(-54.82, 26.87) * mm, "end": v(-43.28, 26.87) * mm});
            skLineSegment(sketch, "E22.3.1.6", {"start": v(-60.6, 16.87) * mm, "end": v(-54.82, 26.87) * mm});
            skLineSegment(sketch, "E22.6.1.6", {"start": v(-54.82, 6.87) * mm, "end": v(-60.6, 16.87) * mm});
            skLineSegment(sketch, "E22.9.1.6", {"start": v(-43.28, 6.87) * mm, "end": v(-54.82, 6.87) * mm});
            skLineSegment(sketch, "E22.12.1.6", {"start": v(-37.5, 16.87) * mm, "end": v(-43.28, 6.87) * mm});
            skLineSegment(sketch, "E22.15.1.6", {"start": v(-43.28, 26.87) * mm, "end": v(-37.5, 16.87) * mm});
            skLineSegment(sketch, "E22.18.1.6", {"start": v(-41.11, 28.12) * mm, "end": v(-35.34, 38.12) * mm});
            skLineSegment(sketch, "E22.21.1.6", {"start": v(-35.34, 18.12) * mm, "end": v(-41.11, 28.12) * mm});
            skLineSegment(sketch, "E22.24.1.6", {"start": v(-35.34, 38.12) * mm, "end": v(-23.79, 38.12) * mm});
            skLineSegment(sketch, "E22.27.1.6", {"start": v(-23.79, 38.12) * mm, "end": v(-18.02, 28.12) * mm});
            skLineSegment(sketch, "E22.30.1.6", {"start": v(-18.02, 28.12) * mm, "end": v(-23.79, 18.12) * mm});
            skLineSegment(sketch, "E22.33.1.6", {"start": v(-23.79, 18.12) * mm, "end": v(-35.34, 18.12) * mm});
            skLineSegment(sketch, "E22.0.1.7", {"start": v(-54.82, 4.37) * mm, "end": v(-43.28, 4.37) * mm});
            skLineSegment(sketch, "E22.3.1.7", {"start": v(-60.6, -5.63) * mm, "end": v(-54.82, 4.37) * mm});
            skLineSegment(sketch, "E22.6.1.7", {"start": v(-54.82, -15.63) * mm, "end": v(-60.6, -5.63) * mm});
            skLineSegment(sketch, "E22.9.1.7", {"start": v(-43.28, -15.63) * mm, "end": v(-54.82, -15.63) * mm});
            skLineSegment(sketch, "E22.12.1.7", {"start": v(-37.5, -5.63) * mm, "end": v(-43.28, -15.63) * mm});
            skLineSegment(sketch, "E22.15.1.7", {"start": v(-43.28, 4.37) * mm, "end": v(-37.5, -5.63) * mm});
            skLineSegment(sketch, "E22.18.1.7", {"start": v(-41.11, 5.62) * mm, "end": v(-35.34, 15.62) * mm});
            skLineSegment(sketch, "E22.21.1.7", {"start": v(-35.34, -4.38) * mm, "end": v(-41.11, 5.62) * mm});
            skLineSegment(sketch, "E22.24.1.7", {"start": v(-35.34, 15.62) * mm, "end": v(-23.79, 15.62) * mm});
            skLineSegment(sketch, "E22.27.1.7", {"start": v(-23.79, 15.62) * mm, "end": v(-18.02, 5.62) * mm});
            skLineSegment(sketch, "E22.30.1.7", {"start": v(-18.02, 5.62) * mm, "end": v(-23.79, -4.38) * mm});
            skLineSegment(sketch, "E22.33.1.7", {"start": v(-23.79, -4.38) * mm, "end": v(-35.34, -4.38) * mm});
            skLineSegment(sketch, "E22.0.1.8", {"start": v(-54.82, -18.13) * mm, "end": v(-43.28, -18.13) * mm});
            skLineSegment(sketch, "E22.3.1.8", {"start": v(-60.6, -28.13) * mm, "end": v(-54.82, -18.13) * mm});
            skLineSegment(sketch, "E22.6.1.8", {"start": v(-54.82, -38.13) * mm, "end": v(-60.6, -28.13) * mm});
            skLineSegment(sketch, "E22.9.1.8", {"start": v(-43.28, -38.13) * mm, "end": v(-54.82, -38.13) * mm});
            skLineSegment(sketch, "E22.12.1.8", {"start": v(-37.5, -28.13) * mm, "end": v(-43.28, -38.13) * mm});
            skLineSegment(sketch, "E22.15.1.8", {"start": v(-43.28, -18.13) * mm, "end": v(-37.5, -28.13) * mm});
            skLineSegment(sketch, "E22.18.1.8", {"start": v(-41.11, -16.88) * mm, "end": v(-35.34, -6.88) * mm});
            skLineSegment(sketch, "E22.21.1.8", {"start": v(-35.34, -26.88) * mm, "end": v(-41.11, -16.88) * mm});
            skLineSegment(sketch, "E22.24.1.8", {"start": v(-35.34, -6.88) * mm, "end": v(-23.79, -6.88) * mm});
            skLineSegment(sketch, "E22.27.1.8", {"start": v(-23.79, -6.88) * mm, "end": v(-18.02, -16.88) * mm});
            skLineSegment(sketch, "E22.30.1.8", {"start": v(-18.02, -16.88) * mm, "end": v(-23.79, -26.88) * mm});
            skLineSegment(sketch, "E22.33.1.8", {"start": v(-23.79, -26.88) * mm, "end": v(-35.34, -26.88) * mm});
            skLineSegment(sketch, "E22.0.1.9", {"start": v(-54.82, -40.63) * mm, "end": v(-43.28, -40.63) * mm});
            skLineSegment(sketch, "E22.3.1.9", {"start": v(-60.6, -50.63) * mm, "end": v(-54.82, -40.63) * mm});
            skLineSegment(sketch, "E22.6.1.9", {"start": v(-54.82, -60.63) * mm, "end": v(-60.6, -50.63) * mm});
            skLineSegment(sketch, "E22.9.1.9", {"start": v(-43.28, -60.63) * mm, "end": v(-54.82, -60.63) * mm});
            skLineSegment(sketch, "E22.12.1.9", {"start": v(-37.5, -50.63) * mm, "end": v(-43.28, -60.63) * mm});
            skLineSegment(sketch, "E22.15.1.9", {"start": v(-43.28, -40.63) * mm, "end": v(-37.5, -50.63) * mm});
            skLineSegment(sketch, "E22.18.1.9", {"start": v(-41.11, -39.38) * mm, "end": v(-35.34, -29.38) * mm});
            skLineSegment(sketch, "E22.21.1.9", {"start": v(-35.34, -49.38) * mm, "end": v(-41.11, -39.38) * mm});
            skLineSegment(sketch, "E22.24.1.9", {"start": v(-35.34, -29.38) * mm, "end": v(-23.79, -29.38) * mm});
            skLineSegment(sketch, "E22.27.1.9", {"start": v(-23.79, -29.38) * mm, "end": v(-18.02, -39.38) * mm});
            skLineSegment(sketch, "E22.30.1.9", {"start": v(-18.02, -39.38) * mm, "end": v(-23.79, -49.38) * mm});
            skLineSegment(sketch, "E22.33.1.9", {"start": v(-23.79, -49.38) * mm, "end": v(-35.34, -49.38) * mm});
            skLineSegment(sketch, "E22.0.1.10", {"start": v(-54.82, -63.13) * mm, "end": v(-43.28, -63.13) * mm});
            skLineSegment(sketch, "E22.3.1.10", {"start": v(-60.6, -73.13) * mm, "end": v(-54.82, -63.13) * mm});
            skLineSegment(sketch, "E22.6.1.10", {"start": v(-54.82, -83.13) * mm, "end": v(-60.6, -73.13) * mm});
            skLineSegment(sketch, "E22.9.1.10", {"start": v(-43.28, -83.13) * mm, "end": v(-54.82, -83.13) * mm});
            skLineSegment(sketch, "E22.12.1.10", {"start": v(-37.5, -73.13) * mm, "end": v(-43.28, -83.13) * mm});
            skLineSegment(sketch, "E22.15.1.10", {"start": v(-43.28, -63.13) * mm, "end": v(-37.5, -73.13) * mm});
            skLineSegment(sketch, "E22.18.1.10", {"start": v(-41.11, -61.88) * mm, "end": v(-35.34, -51.88) * mm});
            skLineSegment(sketch, "E22.21.1.10", {"start": v(-35.34, -71.88) * mm, "end": v(-41.11, -61.88) * mm});
            skLineSegment(sketch, "E22.24.1.10", {"start": v(-35.34, -51.88) * mm, "end": v(-23.79, -51.88) * mm});
            skLineSegment(sketch, "E22.27.1.10", {"start": v(-23.79, -51.88) * mm, "end": v(-18.02, -61.88) * mm});
            skLineSegment(sketch, "E22.30.1.10", {"start": v(-18.02, -61.88) * mm, "end": v(-23.79, -71.88) * mm});
            skLineSegment(sketch, "E22.33.1.10", {"start": v(-23.79, -71.88) * mm, "end": v(-35.34, -71.88) * mm});
            skLineSegment(sketch, "E22.0.1.11", {"start": v(-54.82, -85.63) * mm, "end": v(-43.28, -85.63) * mm});
            skLineSegment(sketch, "E22.3.1.11", {"start": v(-60.6, -95.63) * mm, "end": v(-54.82, -85.63) * mm});
            skLineSegment(sketch, "E22.6.1.11", {"start": v(-54.82, -105.63) * mm, "end": v(-60.6, -95.63) * mm});
            skLineSegment(sketch, "E22.9.1.11", {"start": v(-43.28, -105.63) * mm, "end": v(-54.82, -105.63) * mm});
            skLineSegment(sketch, "E22.12.1.11", {"start": v(-37.5, -95.63) * mm, "end": v(-43.28, -105.63) * mm});
            skLineSegment(sketch, "E22.15.1.11", {"start": v(-43.28, -85.62) * mm, "end": v(-37.5, -95.63) * mm});
            skLineSegment(sketch, "E22.18.1.11", {"start": v(-41.11, -84.38) * mm, "end": v(-35.34, -74.38) * mm});
            skLineSegment(sketch, "E22.21.1.11", {"start": v(-35.34, -94.38) * mm, "end": v(-41.11, -84.38) * mm});
            skLineSegment(sketch, "E22.24.1.11", {"start": v(-35.34, -74.38) * mm, "end": v(-23.79, -74.38) * mm});
            skLineSegment(sketch, "E22.27.1.11", {"start": v(-23.79, -74.38) * mm, "end": v(-18.02, -84.38) * mm});
            skLineSegment(sketch, "E22.30.1.11", {"start": v(-18.02, -84.38) * mm, "end": v(-23.79, -94.38) * mm});
            skLineSegment(sketch, "E22.33.1.11", {"start": v(-23.79, -94.38) * mm, "end": v(-35.34, -94.38) * mm});
            skLineSegment(sketch, "E22.0.1.12", {"start": v(-54.82, -108.13) * mm, "end": v(-43.28, -108.13) * mm});
            skLineSegment(sketch, "E22.3.1.12", {"start": v(-60.6, -118.13) * mm, "end": v(-54.82, -108.13) * mm});
            skLineSegment(sketch, "E22.6.1.12", {"start": v(-54.82, -128.13) * mm, "end": v(-60.6, -118.13) * mm});
            skLineSegment(sketch, "E22.9.1.12", {"start": v(-43.28, -128.13) * mm, "end": v(-54.82, -128.13) * mm});
            skLineSegment(sketch, "E22.12.1.12", {"start": v(-37.5, -118.13) * mm, "end": v(-43.28, -128.13) * mm});
            skLineSegment(sketch, "E22.15.1.12", {"start": v(-43.28, -108.12) * mm, "end": v(-37.5, -118.13) * mm});
            skLineSegment(sketch, "E22.18.1.12", {"start": v(-41.11, -106.88) * mm, "end": v(-35.34, -96.88) * mm});
            skLineSegment(sketch, "E22.21.1.12", {"start": v(-35.34, -116.87) * mm, "end": v(-41.11, -106.88) * mm});
            skLineSegment(sketch, "E22.24.1.12", {"start": v(-35.34, -96.88) * mm, "end": v(-23.79, -96.88) * mm});
            skLineSegment(sketch, "E22.27.1.12", {"start": v(-23.79, -96.88) * mm, "end": v(-18.02, -106.88) * mm});
            skLineSegment(sketch, "E22.30.1.12", {"start": v(-18.02, -106.88) * mm, "end": v(-23.79, -116.88) * mm});
            skLineSegment(sketch, "E22.33.1.12", {"start": v(-23.79, -116.88) * mm, "end": v(-35.34, -116.88) * mm});
            skLineSegment(sketch, "E22.0.1.13", {"start": v(-54.82, -130.62) * mm, "end": v(-43.28, -130.62) * mm});
            skLineSegment(sketch, "E22.3.1.13", {"start": v(-60.6, -140.63) * mm, "end": v(-54.82, -130.63) * mm});
            skLineSegment(sketch, "E22.6.1.13", {"start": v(-54.82, -150.63) * mm, "end": v(-60.6, -140.62) * mm});
            skLineSegment(sketch, "E22.9.1.13", {"start": v(-43.28, -150.62) * mm, "end": v(-54.82, -150.62) * mm});
            skLineSegment(sketch, "E22.12.1.13", {"start": v(-37.5, -140.62) * mm, "end": v(-43.28, -150.62) * mm});
            skLineSegment(sketch, "E22.15.1.13", {"start": v(-43.28, -130.62) * mm, "end": v(-37.5, -140.62) * mm});
            skLineSegment(sketch, "E22.18.1.13", {"start": v(-41.11, -129.38) * mm, "end": v(-35.34, -119.38) * mm});
            skLineSegment(sketch, "E22.21.1.13", {"start": v(-35.34, -139.37) * mm, "end": v(-41.11, -129.38) * mm});
            skLineSegment(sketch, "E22.24.1.13", {"start": v(-35.34, -119.37) * mm, "end": v(-23.79, -119.37) * mm});
            skLineSegment(sketch, "E22.27.1.13", {"start": v(-23.79, -119.38) * mm, "end": v(-18.02, -129.37) * mm});
            skLineSegment(sketch, "E22.30.1.13", {"start": v(-18.02, -129.38) * mm, "end": v(-23.79, -139.38) * mm});
            skLineSegment(sketch, "E22.33.1.13", {"start": v(-23.79, -139.38) * mm, "end": v(-35.34, -139.38) * mm});
            skLineSegment(sketch, "E22.0.1.14", {"start": v(-54.82, -153.12) * mm, "end": v(-43.28, -153.12) * mm});
            skLineSegment(sketch, "E22.3.1.14", {"start": v(-60.6, -163.13) * mm, "end": v(-54.82, -153.13) * mm});
            skLineSegment(sketch, "E22.6.1.14", {"start": v(-54.82, -173.13) * mm, "end": v(-60.6, -163.13) * mm});
            skLineSegment(sketch, "E22.9.1.14", {"start": v(-43.28, -173.12) * mm, "end": v(-54.82, -173.12) * mm});
            skLineSegment(sketch, "E22.12.1.14", {"start": v(-37.5, -163.13) * mm, "end": v(-43.28, -173.12) * mm});
            skLineSegment(sketch, "E22.15.1.14", {"start": v(-43.28, -153.12) * mm, "end": v(-37.5, -163.12) * mm});
            skLineSegment(sketch, "E22.18.1.14", {"start": v(-41.11, -151.88) * mm, "end": v(-35.34, -141.88) * mm});
            skLineSegment(sketch, "E22.21.1.14", {"start": v(-35.34, -161.87) * mm, "end": v(-41.11, -151.88) * mm});
            skLineSegment(sketch, "E22.24.1.14", {"start": v(-35.34, -141.88) * mm, "end": v(-23.79, -141.88) * mm});
            skLineSegment(sketch, "E22.27.1.14", {"start": v(-23.79, -141.88) * mm, "end": v(-18.02, -151.87) * mm});
            skLineSegment(sketch, "E22.30.1.14", {"start": v(-18.02, -151.88) * mm, "end": v(-23.79, -161.88) * mm});
            skLineSegment(sketch, "E22.33.1.14", {"start": v(-23.79, -161.88) * mm, "end": v(-35.34, -161.88) * mm});
            skLineSegment(sketch, "E22.0.2.2", {"start": v(-15.52, 116.87) * mm, "end": v(-3.97, 116.87) * mm});
            skLineSegment(sketch, "E22.3.2.2", {"start": v(-21.29, 106.87) * mm, "end": v(-15.52, 116.87) * mm});
            skLineSegment(sketch, "E22.6.2.2", {"start": v(-15.52, 96.87) * mm, "end": v(-21.29, 106.87) * mm});
            skLineSegment(sketch, "E22.9.2.2", {"start": v(-3.97, 96.87) * mm, "end": v(-15.52, 96.87) * mm});
            skLineSegment(sketch, "E22.12.2.2", {"start": v(1.8, 106.87) * mm, "end": v(-3.97, 96.87) * mm});
            skLineSegment(sketch, "E22.15.2.2", {"start": v(-3.97, 116.87) * mm, "end": v(1.8, 106.87) * mm});
            skLineSegment(sketch, "E22.18.2.2", {"start": v(-1.8, 118.12) * mm, "end": v(3.97, 128.12) * mm});
            skLineSegment(sketch, "E22.21.2.2", {"start": v(3.97, 108.12) * mm, "end": v(-1.8, 118.12) * mm});
            skLineSegment(sketch, "E22.24.2.2", {"start": v(3.97, 128.12) * mm, "end": v(15.52, 128.12) * mm});
            skLineSegment(sketch, "E22.27.2.2", {"start": v(15.52, 128.12) * mm, "end": v(21.29, 118.12) * mm});
            skLineSegment(sketch, "E22.30.2.2", {"start": v(21.29, 118.12) * mm, "end": v(15.52, 108.12) * mm});
            skLineSegment(sketch, "E22.33.2.2", {"start": v(15.52, 108.12) * mm, "end": v(3.97, 108.12) * mm});
            skLineSegment(sketch, "E22.0.2.3", {"start": v(-15.52, 94.37) * mm, "end": v(-3.97, 94.37) * mm});
            skLineSegment(sketch, "E22.3.2.3", {"start": v(-21.29, 84.37) * mm, "end": v(-15.52, 94.37) * mm});
            skLineSegment(sketch, "E22.6.2.3", {"start": v(-15.52, 74.37) * mm, "end": v(-21.29, 84.37) * mm});
            skLineSegment(sketch, "E22.9.2.3", {"start": v(-3.97, 74.37) * mm, "end": v(-15.52, 74.37) * mm});
            skLineSegment(sketch, "E22.12.2.3", {"start": v(1.8, 84.37) * mm, "end": v(-3.97, 74.37) * mm});
            skLineSegment(sketch, "E22.15.2.3", {"start": v(-3.97, 94.37) * mm, "end": v(1.8, 84.37) * mm});
            skLineSegment(sketch, "E22.18.2.3", {"start": v(-1.8, 95.62) * mm, "end": v(3.97, 105.62) * mm});
            skLineSegment(sketch, "E22.21.2.3", {"start": v(3.97, 85.62) * mm, "end": v(-1.8, 95.62) * mm});
            skLineSegment(sketch, "E22.24.2.3", {"start": v(3.97, 105.62) * mm, "end": v(15.52, 105.62) * mm});
            skLineSegment(sketch, "E22.27.2.3", {"start": v(15.52, 105.62) * mm, "end": v(21.29, 95.62) * mm});
            skLineSegment(sketch, "E22.30.2.3", {"start": v(21.29, 95.62) * mm, "end": v(15.52, 85.62) * mm});
            skLineSegment(sketch, "E22.33.2.3", {"start": v(15.52, 85.62) * mm, "end": v(3.97, 85.62) * mm});
            skLineSegment(sketch, "E22.0.2.4", {"start": v(-15.52, 71.87) * mm, "end": v(-3.97, 71.87) * mm});
            skLineSegment(sketch, "E22.3.2.4", {"start": v(-21.29, 61.87) * mm, "end": v(-15.52, 71.87) * mm});
            skLineSegment(sketch, "E22.6.2.4", {"start": v(-15.52, 51.87) * mm, "end": v(-21.29, 61.87) * mm});
            skLineSegment(sketch, "E22.9.2.4", {"start": v(-3.97, 51.87) * mm, "end": v(-15.52, 51.87) * mm});
            skLineSegment(sketch, "E22.12.2.4", {"start": v(1.8, 61.87) * mm, "end": v(-3.97, 51.87) * mm});
            skLineSegment(sketch, "E22.15.2.4", {"start": v(-3.97, 71.87) * mm, "end": v(1.8, 61.87) * mm});
            skLineSegment(sketch, "E22.18.2.4", {"start": v(-1.8, 73.12) * mm, "end": v(3.97, 83.12) * mm});
            skLineSegment(sketch, "E22.21.2.4", {"start": v(3.97, 63.12) * mm, "end": v(-1.8, 73.12) * mm});
            skLineSegment(sketch, "E22.24.2.4", {"start": v(3.97, 83.12) * mm, "end": v(15.52, 83.12) * mm});
            skLineSegment(sketch, "E22.27.2.4", {"start": v(15.52, 83.12) * mm, "end": v(21.29, 73.12) * mm});
            skLineSegment(sketch, "E22.30.2.4", {"start": v(21.29, 73.12) * mm, "end": v(15.52, 63.12) * mm});
            skLineSegment(sketch, "E22.33.2.4", {"start": v(15.52, 63.12) * mm, "end": v(3.97, 63.12) * mm});
            skLineSegment(sketch, "E22.0.2.5", {"start": v(-15.52, 49.37) * mm, "end": v(-3.97, 49.37) * mm});
            skLineSegment(sketch, "E22.3.2.5", {"start": v(-21.29, 39.37) * mm, "end": v(-15.52, 49.37) * mm});
            skLineSegment(sketch, "E22.6.2.5", {"start": v(-15.52, 29.37) * mm, "end": v(-21.29, 39.37) * mm});
            skLineSegment(sketch, "E22.9.2.5", {"start": v(-3.97, 29.37) * mm, "end": v(-15.52, 29.37) * mm});
            skLineSegment(sketch, "E22.12.2.5", {"start": v(1.8, 39.37) * mm, "end": v(-3.97, 29.37) * mm});
            skLineSegment(sketch, "E22.15.2.5", {"start": v(-3.97, 49.37) * mm, "end": v(1.8, 39.37) * mm});
            skLineSegment(sketch, "E22.18.2.5", {"start": v(-1.8, 50.62) * mm, "end": v(3.97, 60.62) * mm});
            skLineSegment(sketch, "E22.21.2.5", {"start": v(3.97, 40.62) * mm, "end": v(-1.8, 50.62) * mm});
            skLineSegment(sketch, "E22.24.2.5", {"start": v(3.97, 60.62) * mm, "end": v(15.52, 60.62) * mm});
            skLineSegment(sketch, "E22.27.2.5", {"start": v(15.52, 60.62) * mm, "end": v(21.29, 50.62) * mm});
            skLineSegment(sketch, "E22.30.2.5", {"start": v(21.29, 50.62) * mm, "end": v(15.52, 40.62) * mm});
            skLineSegment(sketch, "E22.33.2.5", {"start": v(15.52, 40.62) * mm, "end": v(3.97, 40.62) * mm});
            skLineSegment(sketch, "E22.0.2.6", {"start": v(-15.52, 26.87) * mm, "end": v(-3.97, 26.87) * mm});
            skLineSegment(sketch, "E22.3.2.6", {"start": v(-21.29, 16.87) * mm, "end": v(-15.52, 26.87) * mm});
            skLineSegment(sketch, "E22.6.2.6", {"start": v(-15.52, 6.87) * mm, "end": v(-21.29, 16.87) * mm});
            skLineSegment(sketch, "E22.9.2.6", {"start": v(-3.97, 6.87) * mm, "end": v(-15.52, 6.87) * mm});
            skLineSegment(sketch, "E22.12.2.6", {"start": v(1.8, 16.87) * mm, "end": v(-3.97, 6.87) * mm});
            skLineSegment(sketch, "E22.15.2.6", {"start": v(-3.97, 26.87) * mm, "end": v(1.8, 16.87) * mm});
            skLineSegment(sketch, "E22.18.2.6", {"start": v(-1.8, 28.12) * mm, "end": v(3.97, 38.12) * mm});
            skLineSegment(sketch, "E22.21.2.6", {"start": v(3.97, 18.12) * mm, "end": v(-1.8, 28.12) * mm});
            skLineSegment(sketch, "E22.24.2.6", {"start": v(3.97, 38.12) * mm, "end": v(15.52, 38.12) * mm});
            skLineSegment(sketch, "E22.27.2.6", {"start": v(15.52, 38.12) * mm, "end": v(21.29, 28.12) * mm});
            skLineSegment(sketch, "E22.30.2.6", {"start": v(21.29, 28.12) * mm, "end": v(15.52, 18.12) * mm});
            skLineSegment(sketch, "E22.33.2.6", {"start": v(15.52, 18.12) * mm, "end": v(3.97, 18.12) * mm});
            skLineSegment(sketch, "E22.0.2.7", {"start": v(-15.52, 4.37) * mm, "end": v(-3.97, 4.37) * mm});
            skLineSegment(sketch, "E22.3.2.7", {"start": v(-21.29, -5.63) * mm, "end": v(-15.52, 4.37) * mm});
            skLineSegment(sketch, "E22.6.2.7", {"start": v(-15.52, -15.63) * mm, "end": v(-21.29, -5.63) * mm});
            skLineSegment(sketch, "E22.9.2.7", {"start": v(-3.97, -15.63) * mm, "end": v(-15.52, -15.63) * mm});
            skLineSegment(sketch, "E22.12.2.7", {"start": v(1.8, -5.63) * mm, "end": v(-3.97, -15.63) * mm});
            skLineSegment(sketch, "E22.15.2.7", {"start": v(-3.97, 4.37) * mm, "end": v(1.8, -5.63) * mm});
            skLineSegment(sketch, "E22.18.2.7", {"start": v(-1.8, 5.62) * mm, "end": v(3.97, 15.62) * mm});
            skLineSegment(sketch, "E22.21.2.7", {"start": v(3.97, -4.38) * mm, "end": v(-1.8, 5.62) * mm});
            skLineSegment(sketch, "E22.24.2.7", {"start": v(3.97, 15.62) * mm, "end": v(15.52, 15.62) * mm});
            skLineSegment(sketch, "E22.27.2.7", {"start": v(15.52, 15.62) * mm, "end": v(21.29, 5.62) * mm});
            skLineSegment(sketch, "E22.30.2.7", {"start": v(21.29, 5.62) * mm, "end": v(15.52, -4.38) * mm});
            skLineSegment(sketch, "E22.33.2.7", {"start": v(15.52, -4.38) * mm, "end": v(3.97, -4.38) * mm});
            skLineSegment(sketch, "E22.0.2.8", {"start": v(-15.52, -18.13) * mm, "end": v(-3.97, -18.13) * mm});
            skLineSegment(sketch, "E22.3.2.8", {"start": v(-21.29, -28.13) * mm, "end": v(-15.52, -18.13) * mm});
            skLineSegment(sketch, "E22.6.2.8", {"start": v(-15.52, -38.13) * mm, "end": v(-21.29, -28.13) * mm});
            skLineSegment(sketch, "E22.9.2.8", {"start": v(-3.97, -38.13) * mm, "end": v(-15.52, -38.13) * mm});
            skLineSegment(sketch, "E22.12.2.8", {"start": v(1.8, -28.13) * mm, "end": v(-3.97, -38.13) * mm});
            skLineSegment(sketch, "E22.15.2.8", {"start": v(-3.97, -18.13) * mm, "end": v(1.8, -28.13) * mm});
            skLineSegment(sketch, "E22.18.2.8", {"start": v(-1.8, -16.88) * mm, "end": v(3.97, -6.88) * mm});
            skLineSegment(sketch, "E22.21.2.8", {"start": v(3.97, -26.88) * mm, "end": v(-1.8, -16.88) * mm});
            skLineSegment(sketch, "E22.24.2.8", {"start": v(3.97, -6.88) * mm, "end": v(15.52, -6.88) * mm});
            skLineSegment(sketch, "E22.27.2.8", {"start": v(15.52, -6.88) * mm, "end": v(21.29, -16.88) * mm});
            skLineSegment(sketch, "E22.30.2.8", {"start": v(21.29, -16.88) * mm, "end": v(15.52, -26.88) * mm});
            skLineSegment(sketch, "E22.33.2.8", {"start": v(15.52, -26.88) * mm, "end": v(3.97, -26.88) * mm});
            skLineSegment(sketch, "E22.0.2.9", {"start": v(-15.52, -40.63) * mm, "end": v(-3.97, -40.63) * mm});
            skLineSegment(sketch, "E22.3.2.9", {"start": v(-21.29, -50.63) * mm, "end": v(-15.52, -40.63) * mm});
            skLineSegment(sketch, "E22.6.2.9", {"start": v(-15.52, -60.63) * mm, "end": v(-21.29, -50.63) * mm});
            skLineSegment(sketch, "E22.9.2.9", {"start": v(-3.97, -60.63) * mm, "end": v(-15.52, -60.63) * mm});
            skLineSegment(sketch, "E22.12.2.9", {"start": v(1.8, -50.63) * mm, "end": v(-3.97, -60.63) * mm});
            skLineSegment(sketch, "E22.15.2.9", {"start": v(-3.97, -40.63) * mm, "end": v(1.8, -50.63) * mm});
            skLineSegment(sketch, "E22.18.2.9", {"start": v(-1.8, -39.38) * mm, "end": v(3.97, -29.38) * mm});
            skLineSegment(sketch, "E22.21.2.9", {"start": v(3.97, -49.38) * mm, "end": v(-1.8, -39.38) * mm});
            skLineSegment(sketch, "E22.24.2.9", {"start": v(3.97, -29.38) * mm, "end": v(15.52, -29.38) * mm});
            skLineSegment(sketch, "E22.27.2.9", {"start": v(15.52, -29.38) * mm, "end": v(21.29, -39.38) * mm});
            skLineSegment(sketch, "E22.30.2.9", {"start": v(21.29, -39.38) * mm, "end": v(15.52, -49.38) * mm});
            skLineSegment(sketch, "E22.33.2.9", {"start": v(15.52, -49.38) * mm, "end": v(3.97, -49.38) * mm});
            skLineSegment(sketch, "E22.0.2.10", {"start": v(-15.52, -63.13) * mm, "end": v(-3.97, -63.13) * mm});
            skLineSegment(sketch, "E22.3.2.10", {"start": v(-21.29, -73.13) * mm, "end": v(-15.52, -63.13) * mm});
            skLineSegment(sketch, "E22.6.2.10", {"start": v(-15.52, -83.13) * mm, "end": v(-21.29, -73.13) * mm});
            skLineSegment(sketch, "E22.9.2.10", {"start": v(-3.97, -83.13) * mm, "end": v(-15.52, -83.13) * mm});
            skLineSegment(sketch, "E22.12.2.10", {"start": v(1.8, -73.13) * mm, "end": v(-3.97, -83.13) * mm});
            skLineSegment(sketch, "E22.15.2.10", {"start": v(-3.97, -63.13) * mm, "end": v(1.8, -73.13) * mm});
            skLineSegment(sketch, "E22.18.2.10", {"start": v(-1.8, -61.88) * mm, "end": v(3.97, -51.88) * mm});
            skLineSegment(sketch, "E22.21.2.10", {"start": v(3.97, -71.88) * mm, "end": v(-1.8, -61.88) * mm});
            skLineSegment(sketch, "E22.24.2.10", {"start": v(3.97, -51.88) * mm, "end": v(15.52, -51.88) * mm});
            skLineSegment(sketch, "E22.27.2.10", {"start": v(15.52, -51.88) * mm, "end": v(21.29, -61.88) * mm});
            skLineSegment(sketch, "E22.30.2.10", {"start": v(21.29, -61.88) * mm, "end": v(15.52, -71.88) * mm});
            skLineSegment(sketch, "E22.33.2.10", {"start": v(15.52, -71.88) * mm, "end": v(3.97, -71.88) * mm});
            skLineSegment(sketch, "E22.0.2.11", {"start": v(-15.52, -85.63) * mm, "end": v(-3.97, -85.63) * mm});
            skLineSegment(sketch, "E22.3.2.11", {"start": v(-21.29, -95.63) * mm, "end": v(-15.52, -85.63) * mm});
            skLineSegment(sketch, "E22.6.2.11", {"start": v(-15.52, -105.63) * mm, "end": v(-21.29, -95.63) * mm});
            skLineSegment(sketch, "E22.9.2.11", {"start": v(-3.97, -105.63) * mm, "end": v(-15.52, -105.63) * mm});
            skLineSegment(sketch, "E22.12.2.11", {"start": v(1.8, -95.63) * mm, "end": v(-3.97, -105.63) * mm});
            skLineSegment(sketch, "E22.15.2.11", {"start": v(-3.97, -85.62) * mm, "end": v(1.8, -95.63) * mm});
            skLineSegment(sketch, "E22.18.2.11", {"start": v(-1.8, -84.38) * mm, "end": v(3.97, -74.38) * mm});
            skLineSegment(sketch, "E22.21.2.11", {"start": v(3.97, -94.38) * mm, "end": v(-1.8, -84.38) * mm});
            skLineSegment(sketch, "E22.24.2.11", {"start": v(3.97, -74.38) * mm, "end": v(15.52, -74.38) * mm});
            skLineSegment(sketch, "E22.27.2.11", {"start": v(15.52, -74.38) * mm, "end": v(21.29, -84.38) * mm});
            skLineSegment(sketch, "E22.30.2.11", {"start": v(21.29, -84.38) * mm, "end": v(15.52, -94.38) * mm});
            skLineSegment(sketch, "E22.33.2.11", {"start": v(15.52, -94.38) * mm, "end": v(3.97, -94.38) * mm});
            skLineSegment(sketch, "E22.0.2.12", {"start": v(-15.52, -108.13) * mm, "end": v(-3.97, -108.13) * mm});
            skLineSegment(sketch, "E22.3.2.12", {"start": v(-21.29, -118.13) * mm, "end": v(-15.52, -108.13) * mm});
            skLineSegment(sketch, "E22.6.2.12", {"start": v(-15.52, -128.13) * mm, "end": v(-21.29, -118.13) * mm});
            skLineSegment(sketch, "E22.9.2.12", {"start": v(-3.97, -128.13) * mm, "end": v(-15.52, -128.13) * mm});
            skLineSegment(sketch, "E22.12.2.12", {"start": v(1.8, -118.13) * mm, "end": v(-3.97, -128.13) * mm});
            skLineSegment(sketch, "E22.15.2.12", {"start": v(-3.97, -108.12) * mm, "end": v(1.8, -118.13) * mm});
            skLineSegment(sketch, "E22.18.2.12", {"start": v(-1.8, -106.88) * mm, "end": v(3.97, -96.88) * mm});
            skLineSegment(sketch, "E22.21.2.12", {"start": v(3.97, -116.87) * mm, "end": v(-1.8, -106.88) * mm});
            skLineSegment(sketch, "E22.24.2.12", {"start": v(3.97, -96.88) * mm, "end": v(15.52, -96.88) * mm});
            skLineSegment(sketch, "E22.27.2.12", {"start": v(15.52, -96.88) * mm, "end": v(21.29, -106.88) * mm});
            skLineSegment(sketch, "E22.30.2.12", {"start": v(21.29, -106.88) * mm, "end": v(15.52, -116.88) * mm});
            skLineSegment(sketch, "E22.33.2.12", {"start": v(15.52, -116.88) * mm, "end": v(3.97, -116.88) * mm});
            skLineSegment(sketch, "E22.0.2.13", {"start": v(-15.52, -130.62) * mm, "end": v(-3.97, -130.62) * mm});
            skLineSegment(sketch, "E22.3.2.13", {"start": v(-21.29, -140.63) * mm, "end": v(-15.52, -130.63) * mm});
            skLineSegment(sketch, "E22.6.2.13", {"start": v(-15.52, -150.63) * mm, "end": v(-21.29, -140.63) * mm});
            skLineSegment(sketch, "E22.9.2.13", {"start": v(-3.97, -150.62) * mm, "end": v(-15.52, -150.62) * mm});
            skLineSegment(sketch, "E22.12.2.13", {"start": v(1.8, -140.62) * mm, "end": v(-3.97, -150.62) * mm});
            skLineSegment(sketch, "E22.15.2.13", {"start": v(-3.97, -130.62) * mm, "end": v(1.8, -140.62) * mm});
            skLineSegment(sketch, "E22.18.2.13", {"start": v(-1.8, -129.38) * mm, "end": v(3.97, -119.38) * mm});
            skLineSegment(sketch, "E22.21.2.13", {"start": v(3.97, -139.37) * mm, "end": v(-1.8, -129.38) * mm});
            skLineSegment(sketch, "E22.24.2.13", {"start": v(3.97, -119.37) * mm, "end": v(15.52, -119.37) * mm});
            skLineSegment(sketch, "E22.27.2.13", {"start": v(15.52, -119.38) * mm, "end": v(21.29, -129.37) * mm});
            skLineSegment(sketch, "E22.30.2.13", {"start": v(21.29, -129.38) * mm, "end": v(15.52, -139.38) * mm});
            skLineSegment(sketch, "E22.33.2.13", {"start": v(15.52, -139.38) * mm, "end": v(3.97, -139.38) * mm});
            skLineSegment(sketch, "E22.0.2.14", {"start": v(-15.52, -153.12) * mm, "end": v(-3.97, -153.12) * mm});
            skLineSegment(sketch, "E22.3.2.14", {"start": v(-21.29, -163.13) * mm, "end": v(-15.52, -153.13) * mm});
            skLineSegment(sketch, "E22.6.2.14", {"start": v(-15.52, -173.13) * mm, "end": v(-21.29, -163.13) * mm});
            skLineSegment(sketch, "E22.9.2.14", {"start": v(-3.97, -173.12) * mm, "end": v(-15.52, -173.12) * mm});
            skLineSegment(sketch, "E22.12.2.14", {"start": v(1.8, -163.13) * mm, "end": v(-3.97, -173.12) * mm});
            skLineSegment(sketch, "E22.15.2.14", {"start": v(-3.97, -153.12) * mm, "end": v(1.8, -163.12) * mm});
            skLineSegment(sketch, "E22.18.2.14", {"start": v(-1.8, -151.88) * mm, "end": v(3.97, -141.88) * mm});
            skLineSegment(sketch, "E22.21.2.14", {"start": v(3.97, -161.87) * mm, "end": v(-1.8, -151.88) * mm});
            skLineSegment(sketch, "E22.24.2.14", {"start": v(3.97, -141.88) * mm, "end": v(15.52, -141.88) * mm});
            skLineSegment(sketch, "E22.27.2.14", {"start": v(15.52, -141.88) * mm, "end": v(21.29, -151.87) * mm});
            skLineSegment(sketch, "E22.30.2.14", {"start": v(21.29, -151.88) * mm, "end": v(15.52, -161.88) * mm});
            skLineSegment(sketch, "E22.33.2.14", {"start": v(15.52, -161.88) * mm, "end": v(3.97, -161.88) * mm});
            skLineSegment(sketch, "E22.0.3.2", {"start": v(23.79, 116.87) * mm, "end": v(35.34, 116.87) * mm});
            skLineSegment(sketch, "E22.3.3.2", {"start": v(18.02, 106.87) * mm, "end": v(23.79, 116.87) * mm});
            skLineSegment(sketch, "E22.6.3.2", {"start": v(23.79, 96.87) * mm, "end": v(18.02, 106.87) * mm});
            skLineSegment(sketch, "E22.9.3.2", {"start": v(35.34, 96.87) * mm, "end": v(23.79, 96.87) * mm});
            skLineSegment(sketch, "E22.12.3.2", {"start": v(41.11, 106.87) * mm, "end": v(35.34, 96.87) * mm});
            skLineSegment(sketch, "E22.15.3.2", {"start": v(35.34, 116.87) * mm, "end": v(41.11, 106.87) * mm});
            skLineSegment(sketch, "E22.18.3.2", {"start": v(37.5, 118.12) * mm, "end": v(43.28, 128.12) * mm});
            skLineSegment(sketch, "E22.21.3.2", {"start": v(43.28, 108.12) * mm, "end": v(37.5, 118.12) * mm});
            skLineSegment(sketch, "E22.24.3.2", {"start": v(43.28, 128.12) * mm, "end": v(54.82, 128.12) * mm});
            skLineSegment(sketch, "E22.27.3.2", {"start": v(54.82, 128.12) * mm, "end": v(60.6, 118.12) * mm});
            skLineSegment(sketch, "E22.30.3.2", {"start": v(60.6, 118.12) * mm, "end": v(54.82, 108.12) * mm});
            skLineSegment(sketch, "E22.33.3.2", {"start": v(54.82, 108.12) * mm, "end": v(43.28, 108.12) * mm});
            skLineSegment(sketch, "E22.0.3.3", {"start": v(23.79, 94.37) * mm, "end": v(35.34, 94.37) * mm});
            skLineSegment(sketch, "E22.3.3.3", {"start": v(18.02, 84.37) * mm, "end": v(23.79, 94.37) * mm});
            skLineSegment(sketch, "E22.6.3.3", {"start": v(23.79, 74.37) * mm, "end": v(18.02, 84.37) * mm});
            skLineSegment(sketch, "E22.9.3.3", {"start": v(35.34, 74.37) * mm, "end": v(23.79, 74.37) * mm});
            skLineSegment(sketch, "E22.12.3.3", {"start": v(41.11, 84.37) * mm, "end": v(35.34, 74.37) * mm});
            skLineSegment(sketch, "E22.15.3.3", {"start": v(35.34, 94.37) * mm, "end": v(41.11, 84.37) * mm});
            skLineSegment(sketch, "E22.18.3.3", {"start": v(37.5, 95.62) * mm, "end": v(43.28, 105.62) * mm});
            skLineSegment(sketch, "E22.21.3.3", {"start": v(43.28, 85.62) * mm, "end": v(37.5, 95.62) * mm});
            skLineSegment(sketch, "E22.24.3.3", {"start": v(43.28, 105.62) * mm, "end": v(54.82, 105.62) * mm});
            skLineSegment(sketch, "E22.27.3.3", {"start": v(54.82, 105.62) * mm, "end": v(60.6, 95.62) * mm});
            skLineSegment(sketch, "E22.30.3.3", {"start": v(60.6, 95.62) * mm, "end": v(54.82, 85.62) * mm});
            skLineSegment(sketch, "E22.33.3.3", {"start": v(54.82, 85.62) * mm, "end": v(43.28, 85.62) * mm});
            skLineSegment(sketch, "E22.0.3.4", {"start": v(23.79, 71.87) * mm, "end": v(35.34, 71.87) * mm});
            skLineSegment(sketch, "E22.3.3.4", {"start": v(18.02, 61.87) * mm, "end": v(23.79, 71.87) * mm});
            skLineSegment(sketch, "E22.6.3.4", {"start": v(23.79, 51.87) * mm, "end": v(18.02, 61.87) * mm});
            skLineSegment(sketch, "E22.9.3.4", {"start": v(35.34, 51.87) * mm, "end": v(23.79, 51.87) * mm});
            skLineSegment(sketch, "E22.12.3.4", {"start": v(41.11, 61.87) * mm, "end": v(35.34, 51.87) * mm});
            skLineSegment(sketch, "E22.15.3.4", {"start": v(35.34, 71.87) * mm, "end": v(41.11, 61.87) * mm});
            skLineSegment(sketch, "E22.18.3.4", {"start": v(37.5, 73.12) * mm, "end": v(43.28, 83.12) * mm});
            skLineSegment(sketch, "E22.21.3.4", {"start": v(43.28, 63.12) * mm, "end": v(37.5, 73.12) * mm});
            skLineSegment(sketch, "E22.24.3.4", {"start": v(43.28, 83.12) * mm, "end": v(54.82, 83.12) * mm});
            skLineSegment(sketch, "E22.27.3.4", {"start": v(54.82, 83.12) * mm, "end": v(60.6, 73.12) * mm});
            skLineSegment(sketch, "E22.30.3.4", {"start": v(60.6, 73.12) * mm, "end": v(54.82, 63.12) * mm});
            skLineSegment(sketch, "E22.33.3.4", {"start": v(54.82, 63.12) * mm, "end": v(43.28, 63.12) * mm});
            skLineSegment(sketch, "E22.0.3.5", {"start": v(23.79, 49.37) * mm, "end": v(35.34, 49.37) * mm});
            skLineSegment(sketch, "E22.3.3.5", {"start": v(18.02, 39.37) * mm, "end": v(23.79, 49.37) * mm});
            skLineSegment(sketch, "E22.6.3.5", {"start": v(23.79, 29.37) * mm, "end": v(18.02, 39.37) * mm});
            skLineSegment(sketch, "E22.9.3.5", {"start": v(35.34, 29.37) * mm, "end": v(23.79, 29.37) * mm});
            skLineSegment(sketch, "E22.12.3.5", {"start": v(41.11, 39.37) * mm, "end": v(35.34, 29.37) * mm});
            skLineSegment(sketch, "E22.15.3.5", {"start": v(35.34, 49.37) * mm, "end": v(41.11, 39.37) * mm});
            skLineSegment(sketch, "E22.18.3.5", {"start": v(37.5, 50.62) * mm, "end": v(43.28, 60.62) * mm});
            skLineSegment(sketch, "E22.21.3.5", {"start": v(43.28, 40.62) * mm, "end": v(37.5, 50.62) * mm});
            skLineSegment(sketch, "E22.24.3.5", {"start": v(43.28, 60.62) * mm, "end": v(54.82, 60.62) * mm});
            skLineSegment(sketch, "E22.27.3.5", {"start": v(54.82, 60.62) * mm, "end": v(60.6, 50.62) * mm});
            skLineSegment(sketch, "E22.30.3.5", {"start": v(60.6, 50.62) * mm, "end": v(54.82, 40.62) * mm});
            skLineSegment(sketch, "E22.33.3.5", {"start": v(54.82, 40.62) * mm, "end": v(43.28, 40.62) * mm});
            skLineSegment(sketch, "E22.0.3.6", {"start": v(23.79, 26.87) * mm, "end": v(35.34, 26.87) * mm});
            skLineSegment(sketch, "E22.3.3.6", {"start": v(18.02, 16.87) * mm, "end": v(23.79, 26.87) * mm});
            skLineSegment(sketch, "E22.6.3.6", {"start": v(23.79, 6.87) * mm, "end": v(18.02, 16.87) * mm});
            skLineSegment(sketch, "E22.9.3.6", {"start": v(35.34, 6.87) * mm, "end": v(23.79, 6.87) * mm});
            skLineSegment(sketch, "E22.12.3.6", {"start": v(41.11, 16.87) * mm, "end": v(35.34, 6.87) * mm});
            skLineSegment(sketch, "E22.15.3.6", {"start": v(35.34, 26.87) * mm, "end": v(41.11, 16.87) * mm});
            skLineSegment(sketch, "E22.18.3.6", {"start": v(37.5, 28.12) * mm, "end": v(43.28, 38.12) * mm});
            skLineSegment(sketch, "E22.21.3.6", {"start": v(43.28, 18.12) * mm, "end": v(37.5, 28.12) * mm});
            skLineSegment(sketch, "E22.24.3.6", {"start": v(43.28, 38.12) * mm, "end": v(54.82, 38.12) * mm});
            skLineSegment(sketch, "E22.27.3.6", {"start": v(54.82, 38.12) * mm, "end": v(60.6, 28.12) * mm});
            skLineSegment(sketch, "E22.30.3.6", {"start": v(60.6, 28.12) * mm, "end": v(54.82, 18.12) * mm});
            skLineSegment(sketch, "E22.33.3.6", {"start": v(54.82, 18.12) * mm, "end": v(43.28, 18.12) * mm});
            skLineSegment(sketch, "E22.0.3.7", {"start": v(23.79, 4.37) * mm, "end": v(35.34, 4.37) * mm});
            skLineSegment(sketch, "E22.3.3.7", {"start": v(18.02, -5.63) * mm, "end": v(23.79, 4.37) * mm});
            skLineSegment(sketch, "E22.6.3.7", {"start": v(23.79, -15.63) * mm, "end": v(18.02, -5.63) * mm});
            skLineSegment(sketch, "E22.9.3.7", {"start": v(35.34, -15.63) * mm, "end": v(23.79, -15.63) * mm});
            skLineSegment(sketch, "E22.12.3.7", {"start": v(41.11, -5.63) * mm, "end": v(35.34, -15.63) * mm});
            skLineSegment(sketch, "E22.15.3.7", {"start": v(35.34, 4.37) * mm, "end": v(41.11, -5.63) * mm});
            skLineSegment(sketch, "E22.18.3.7", {"start": v(37.5, 5.62) * mm, "end": v(43.28, 15.62) * mm});
            skLineSegment(sketch, "E22.21.3.7", {"start": v(43.28, -4.38) * mm, "end": v(37.5, 5.62) * mm});
            skLineSegment(sketch, "E22.24.3.7", {"start": v(43.28, 15.62) * mm, "end": v(54.82, 15.62) * mm});
            skLineSegment(sketch, "E22.27.3.7", {"start": v(54.82, 15.62) * mm, "end": v(60.6, 5.62) * mm});
            skLineSegment(sketch, "E22.30.3.7", {"start": v(60.6, 5.62) * mm, "end": v(54.82, -4.38) * mm});
            skLineSegment(sketch, "E22.33.3.7", {"start": v(54.82, -4.38) * mm, "end": v(43.28, -4.38) * mm});
            skLineSegment(sketch, "E22.0.3.8", {"start": v(23.79, -18.13) * mm, "end": v(35.34, -18.13) * mm});
            skLineSegment(sketch, "E22.3.3.8", {"start": v(18.02, -28.13) * mm, "end": v(23.79, -18.13) * mm});
            skLineSegment(sketch, "E22.6.3.8", {"start": v(23.79, -38.13) * mm, "end": v(18.02, -28.13) * mm});
            skLineSegment(sketch, "E22.9.3.8", {"start": v(35.34, -38.13) * mm, "end": v(23.79, -38.13) * mm});
            skLineSegment(sketch, "E22.12.3.8", {"start": v(41.11, -28.13) * mm, "end": v(35.34, -38.13) * mm});
            skLineSegment(sketch, "E22.15.3.8", {"start": v(35.34, -18.13) * mm, "end": v(41.11, -28.13) * mm});
            skLineSegment(sketch, "E22.18.3.8", {"start": v(37.5, -16.88) * mm, "end": v(43.28, -6.88) * mm});
            skLineSegment(sketch, "E22.21.3.8", {"start": v(43.28, -26.88) * mm, "end": v(37.5, -16.88) * mm});
            skLineSegment(sketch, "E22.24.3.8", {"start": v(43.28, -6.88) * mm, "end": v(54.82, -6.88) * mm});
            skLineSegment(sketch, "E22.27.3.8", {"start": v(54.82, -6.88) * mm, "end": v(60.6, -16.88) * mm});
            skLineSegment(sketch, "E22.30.3.8", {"start": v(60.6, -16.88) * mm, "end": v(54.82, -26.88) * mm});
            skLineSegment(sketch, "E22.33.3.8", {"start": v(54.82, -26.88) * mm, "end": v(43.28, -26.88) * mm});
            skLineSegment(sketch, "E22.0.3.9", {"start": v(23.79, -40.63) * mm, "end": v(35.34, -40.63) * mm});
            skLineSegment(sketch, "E22.3.3.9", {"start": v(18.02, -50.63) * mm, "end": v(23.79, -40.63) * mm});
            skLineSegment(sketch, "E22.6.3.9", {"start": v(23.79, -60.63) * mm, "end": v(18.02, -50.63) * mm});
            skLineSegment(sketch, "E22.9.3.9", {"start": v(35.34, -60.63) * mm, "end": v(23.79, -60.63) * mm});
            skLineSegment(sketch, "E22.12.3.9", {"start": v(41.11, -50.63) * mm, "end": v(35.34, -60.63) * mm});
            skLineSegment(sketch, "E22.15.3.9", {"start": v(35.34, -40.63) * mm, "end": v(41.11, -50.63) * mm});
            skLineSegment(sketch, "E22.18.3.9", {"start": v(37.5, -39.38) * mm, "end": v(43.28, -29.38) * mm});
            skLineSegment(sketch, "E22.21.3.9", {"start": v(43.28, -49.38) * mm, "end": v(37.5, -39.38) * mm});
            skLineSegment(sketch, "E22.24.3.9", {"start": v(43.28, -29.38) * mm, "end": v(54.82, -29.38) * mm});
            skLineSegment(sketch, "E22.27.3.9", {"start": v(54.82, -29.38) * mm, "end": v(60.6, -39.38) * mm});
            skLineSegment(sketch, "E22.30.3.9", {"start": v(60.6, -39.38) * mm, "end": v(54.82, -49.38) * mm});
            skLineSegment(sketch, "E22.33.3.9", {"start": v(54.82, -49.38) * mm, "end": v(43.28, -49.38) * mm});
            skLineSegment(sketch, "E22.0.3.10", {"start": v(23.79, -63.13) * mm, "end": v(35.34, -63.13) * mm});
            skLineSegment(sketch, "E22.3.3.10", {"start": v(18.02, -73.13) * mm, "end": v(23.79, -63.13) * mm});
            skLineSegment(sketch, "E22.6.3.10", {"start": v(23.79, -83.13) * mm, "end": v(18.02, -73.13) * mm});
            skLineSegment(sketch, "E22.9.3.10", {"start": v(35.34, -83.13) * mm, "end": v(23.79, -83.13) * mm});
            skLineSegment(sketch, "E22.12.3.10", {"start": v(41.11, -73.13) * mm, "end": v(35.34, -83.13) * mm});
            skLineSegment(sketch, "E22.15.3.10", {"start": v(35.34, -63.13) * mm, "end": v(41.11, -73.13) * mm});
            skLineSegment(sketch, "E22.18.3.10", {"start": v(37.5, -61.88) * mm, "end": v(43.28, -51.88) * mm});
            skLineSegment(sketch, "E22.21.3.10", {"start": v(43.28, -71.88) * mm, "end": v(37.5, -61.88) * mm});
            skLineSegment(sketch, "E22.24.3.10", {"start": v(43.28, -51.88) * mm, "end": v(54.82, -51.88) * mm});
            skLineSegment(sketch, "E22.27.3.10", {"start": v(54.82, -51.88) * mm, "end": v(60.6, -61.88) * mm});
            skLineSegment(sketch, "E22.30.3.10", {"start": v(60.6, -61.88) * mm, "end": v(54.82, -71.88) * mm});
            skLineSegment(sketch, "E22.33.3.10", {"start": v(54.82, -71.88) * mm, "end": v(43.28, -71.88) * mm});
            skLineSegment(sketch, "E22.0.3.11", {"start": v(23.79, -85.63) * mm, "end": v(35.34, -85.63) * mm});
            skLineSegment(sketch, "E22.3.3.11", {"start": v(18.02, -95.63) * mm, "end": v(23.79, -85.63) * mm});
            skLineSegment(sketch, "E22.6.3.11", {"start": v(23.79, -105.63) * mm, "end": v(18.02, -95.63) * mm});
            skLineSegment(sketch, "E22.9.3.11", {"start": v(35.34, -105.63) * mm, "end": v(23.79, -105.63) * mm});
            skLineSegment(sketch, "E22.12.3.11", {"start": v(41.11, -95.63) * mm, "end": v(35.34, -105.63) * mm});
            skLineSegment(sketch, "E22.15.3.11", {"start": v(35.34, -85.62) * mm, "end": v(41.11, -95.63) * mm});
            skLineSegment(sketch, "E22.18.3.11", {"start": v(37.5, -84.38) * mm, "end": v(43.28, -74.38) * mm});
            skLineSegment(sketch, "E22.21.3.11", {"start": v(43.28, -94.37) * mm, "end": v(37.5, -84.38) * mm});
            skLineSegment(sketch, "E22.24.3.11", {"start": v(43.28, -74.38) * mm, "end": v(54.82, -74.38) * mm});
            skLineSegment(sketch, "E22.27.3.11", {"start": v(54.82, -74.38) * mm, "end": v(60.6, -84.38) * mm});
            skLineSegment(sketch, "E22.30.3.11", {"start": v(60.6, -84.38) * mm, "end": v(54.82, -94.38) * mm});
            skLineSegment(sketch, "E22.33.3.11", {"start": v(54.82, -94.38) * mm, "end": v(43.28, -94.38) * mm});
            skLineSegment(sketch, "E22.0.3.12", {"start": v(23.79, -108.13) * mm, "end": v(35.34, -108.13) * mm});
            skLineSegment(sketch, "E22.3.3.12", {"start": v(18.02, -118.13) * mm, "end": v(23.79, -108.13) * mm});
            skLineSegment(sketch, "E22.6.3.12", {"start": v(23.79, -128.13) * mm, "end": v(18.02, -118.13) * mm});
            skLineSegment(sketch, "E22.9.3.12", {"start": v(35.34, -128.13) * mm, "end": v(23.79, -128.13) * mm});
            skLineSegment(sketch, "E22.12.3.12", {"start": v(41.11, -118.13) * mm, "end": v(35.34, -128.13) * mm});
            skLineSegment(sketch, "E22.15.3.12", {"start": v(35.34, -108.12) * mm, "end": v(41.11, -118.13) * mm});
            skLineSegment(sketch, "E22.18.3.12", {"start": v(37.5, -106.88) * mm, "end": v(43.28, -96.88) * mm});
            skLineSegment(sketch, "E22.21.3.12", {"start": v(43.28, -116.87) * mm, "end": v(37.5, -106.88) * mm});
            skLineSegment(sketch, "E22.24.3.12", {"start": v(43.28, -96.88) * mm, "end": v(54.82, -96.88) * mm});
            skLineSegment(sketch, "E22.27.3.12", {"start": v(54.82, -96.88) * mm, "end": v(60.6, -106.88) * mm});
            skLineSegment(sketch, "E22.30.3.12", {"start": v(60.6, -106.88) * mm, "end": v(54.82, -116.88) * mm});
            skLineSegment(sketch, "E22.33.3.12", {"start": v(54.82, -116.88) * mm, "end": v(43.28, -116.88) * mm});
            skLineSegment(sketch, "E22.0.3.13", {"start": v(23.79, -130.62) * mm, "end": v(35.34, -130.62) * mm});
            skLineSegment(sketch, "E22.3.3.13", {"start": v(18.02, -140.63) * mm, "end": v(23.79, -130.63) * mm});
            skLineSegment(sketch, "E22.6.3.13", {"start": v(23.79, -150.63) * mm, "end": v(18.02, -140.63) * mm});
            skLineSegment(sketch, "E22.9.3.13", {"start": v(35.34, -150.62) * mm, "end": v(23.79, -150.62) * mm});
            skLineSegment(sketch, "E22.12.3.13", {"start": v(41.11, -140.62) * mm, "end": v(35.34, -150.62) * mm});
            skLineSegment(sketch, "E22.15.3.13", {"start": v(35.34, -130.62) * mm, "end": v(41.11, -140.62) * mm});
            skLineSegment(sketch, "E22.18.3.13", {"start": v(37.5, -129.38) * mm, "end": v(43.28, -119.38) * mm});
            skLineSegment(sketch, "E22.21.3.13", {"start": v(43.28, -139.37) * mm, "end": v(37.5, -129.38) * mm});
            skLineSegment(sketch, "E22.24.3.13", {"start": v(43.28, -119.37) * mm, "end": v(54.82, -119.37) * mm});
            skLineSegment(sketch, "E22.27.3.13", {"start": v(54.82, -119.37) * mm, "end": v(60.6, -129.37) * mm});
            skLineSegment(sketch, "E22.30.3.13", {"start": v(60.6, -129.38) * mm, "end": v(54.82, -139.38) * mm});
            skLineSegment(sketch, "E22.33.3.13", {"start": v(54.82, -139.38) * mm, "end": v(43.28, -139.38) * mm});
            skLineSegment(sketch, "E22.0.3.14", {"start": v(23.79, -153.12) * mm, "end": v(35.34, -153.12) * mm});
            skLineSegment(sketch, "E22.3.3.14", {"start": v(18.02, -163.13) * mm, "end": v(23.79, -153.13) * mm});
            skLineSegment(sketch, "E22.6.3.14", {"start": v(23.79, -173.13) * mm, "end": v(18.02, -163.13) * mm});
            skLineSegment(sketch, "E22.9.3.14", {"start": v(35.34, -173.12) * mm, "end": v(23.79, -173.12) * mm});
            skLineSegment(sketch, "E22.12.3.14", {"start": v(41.11, -163.13) * mm, "end": v(35.34, -173.13) * mm});
            skLineSegment(sketch, "E22.15.3.14", {"start": v(35.34, -153.12) * mm, "end": v(41.11, -163.12) * mm});
            skLineSegment(sketch, "E22.18.3.14", {"start": v(37.5, -151.88) * mm, "end": v(43.28, -141.88) * mm});
            skLineSegment(sketch, "E22.21.3.14", {"start": v(43.28, -161.87) * mm, "end": v(37.5, -151.88) * mm});
            skLineSegment(sketch, "E22.24.3.14", {"start": v(43.28, -141.88) * mm, "end": v(54.82, -141.88) * mm});
            skLineSegment(sketch, "E22.27.3.14", {"start": v(54.82, -141.88) * mm, "end": v(60.6, -151.87) * mm});
            skLineSegment(sketch, "E22.30.3.14", {"start": v(60.6, -151.88) * mm, "end": v(54.82, -161.88) * mm});
            skLineSegment(sketch, "E22.33.3.14", {"start": v(54.82, -161.88) * mm, "end": v(43.28, -161.88) * mm});
            skLineSegment(sketch, "E22.0.4.2", {"start": v(63.1, 116.87) * mm, "end": v(74.64, 116.87) * mm});
            skLineSegment(sketch, "E22.3.4.2", {"start": v(57.32, 106.87) * mm, "end": v(63.1, 116.87) * mm});
            skLineSegment(sketch, "E22.6.4.2", {"start": v(63.1, 96.87) * mm, "end": v(57.32, 106.87) * mm});
            skLineSegment(sketch, "E22.9.4.2", {"start": v(74.64, 96.87) * mm, "end": v(63.1, 96.87) * mm});
            skLineSegment(sketch, "E22.12.4.2", {"start": v(80.42, 106.87) * mm, "end": v(74.64, 96.87) * mm});
            skLineSegment(sketch, "E22.15.4.2", {"start": v(74.64, 116.87) * mm, "end": v(80.42, 106.87) * mm});
            skLineSegment(sketch, "E22.18.4.2", {"start": v(76.8, 118.12) * mm, "end": v(82.58, 128.12) * mm});
            skLineSegment(sketch, "E22.21.4.2", {"start": v(82.58, 108.12) * mm, "end": v(76.8, 118.12) * mm});
            skLineSegment(sketch, "E22.24.4.2", {"start": v(82.58, 128.12) * mm, "end": v(94.13, 128.12) * mm});
            skLineSegment(sketch, "E22.27.4.2", {"start": v(94.13, 128.12) * mm, "end": v(99.9, 118.12) * mm});
            skLineSegment(sketch, "E22.30.4.2", {"start": v(99.9, 118.12) * mm, "end": v(94.13, 108.12) * mm});
            skLineSegment(sketch, "E22.33.4.2", {"start": v(94.13, 108.12) * mm, "end": v(82.58, 108.12) * mm});
            skLineSegment(sketch, "E22.0.4.3", {"start": v(63.1, 94.37) * mm, "end": v(74.64, 94.37) * mm});
            skLineSegment(sketch, "E22.3.4.3", {"start": v(57.32, 84.37) * mm, "end": v(63.1, 94.37) * mm});
            skLineSegment(sketch, "E22.6.4.3", {"start": v(63.1, 74.37) * mm, "end": v(57.32, 84.37) * mm});
            skLineSegment(sketch, "E22.9.4.3", {"start": v(74.64, 74.37) * mm, "end": v(63.1, 74.37) * mm});
            skLineSegment(sketch, "E22.12.4.3", {"start": v(80.42, 84.37) * mm, "end": v(74.64, 74.37) * mm});
            skLineSegment(sketch, "E22.15.4.3", {"start": v(74.64, 94.37) * mm, "end": v(80.42, 84.37) * mm});
            skLineSegment(sketch, "E22.18.4.3", {"start": v(76.8, 95.62) * mm, "end": v(82.58, 105.62) * mm});
            skLineSegment(sketch, "E22.21.4.3", {"start": v(82.58, 85.62) * mm, "end": v(76.8, 95.62) * mm});
            skLineSegment(sketch, "E22.24.4.3", {"start": v(82.58, 105.62) * mm, "end": v(94.13, 105.62) * mm});
            skLineSegment(sketch, "E22.27.4.3", {"start": v(94.13, 105.62) * mm, "end": v(99.9, 95.62) * mm});
            skLineSegment(sketch, "E22.30.4.3", {"start": v(99.9, 95.62) * mm, "end": v(94.13, 85.62) * mm});
            skLineSegment(sketch, "E22.33.4.3", {"start": v(94.13, 85.62) * mm, "end": v(82.58, 85.62) * mm});
            skLineSegment(sketch, "E22.0.4.4", {"start": v(63.1, 71.87) * mm, "end": v(74.64, 71.87) * mm});
            skLineSegment(sketch, "E22.3.4.4", {"start": v(57.32, 61.87) * mm, "end": v(63.1, 71.87) * mm});
            skLineSegment(sketch, "E22.6.4.4", {"start": v(63.1, 51.87) * mm, "end": v(57.32, 61.87) * mm});
            skLineSegment(sketch, "E22.9.4.4", {"start": v(74.64, 51.87) * mm, "end": v(63.1, 51.87) * mm});
            skLineSegment(sketch, "E22.12.4.4", {"start": v(80.42, 61.87) * mm, "end": v(74.64, 51.87) * mm});
            skLineSegment(sketch, "E22.15.4.4", {"start": v(74.64, 71.87) * mm, "end": v(80.42, 61.87) * mm});
            skLineSegment(sketch, "E22.18.4.4", {"start": v(76.8, 73.12) * mm, "end": v(82.58, 83.12) * mm});
            skLineSegment(sketch, "E22.21.4.4", {"start": v(82.58, 63.12) * mm, "end": v(76.8, 73.12) * mm});
            skLineSegment(sketch, "E22.24.4.4", {"start": v(82.58, 83.12) * mm, "end": v(94.13, 83.12) * mm});
            skLineSegment(sketch, "E22.27.4.4", {"start": v(94.13, 83.12) * mm, "end": v(99.9, 73.12) * mm});
            skLineSegment(sketch, "E22.30.4.4", {"start": v(99.9, 73.12) * mm, "end": v(94.13, 63.12) * mm});
            skLineSegment(sketch, "E22.33.4.4", {"start": v(94.13, 63.12) * mm, "end": v(82.58, 63.12) * mm});
            skLineSegment(sketch, "E22.0.4.5", {"start": v(63.1, 49.37) * mm, "end": v(74.64, 49.37) * mm});
            skLineSegment(sketch, "E22.3.4.5", {"start": v(57.32, 39.37) * mm, "end": v(63.1, 49.37) * mm});
            skLineSegment(sketch, "E22.6.4.5", {"start": v(63.1, 29.37) * mm, "end": v(57.32, 39.37) * mm});
            skLineSegment(sketch, "E22.9.4.5", {"start": v(74.64, 29.37) * mm, "end": v(63.1, 29.37) * mm});
            skLineSegment(sketch, "E22.12.4.5", {"start": v(80.42, 39.37) * mm, "end": v(74.64, 29.37) * mm});
            skLineSegment(sketch, "E22.15.4.5", {"start": v(74.64, 49.37) * mm, "end": v(80.42, 39.37) * mm});
            skLineSegment(sketch, "E22.18.4.5", {"start": v(76.8, 50.62) * mm, "end": v(82.58, 60.62) * mm});
            skLineSegment(sketch, "E22.21.4.5", {"start": v(82.58, 40.62) * mm, "end": v(76.8, 50.62) * mm});
            skLineSegment(sketch, "E22.24.4.5", {"start": v(82.58, 60.62) * mm, "end": v(94.13, 60.62) * mm});
            skLineSegment(sketch, "E22.27.4.5", {"start": v(94.13, 60.62) * mm, "end": v(99.9, 50.62) * mm});
            skLineSegment(sketch, "E22.30.4.5", {"start": v(99.9, 50.62) * mm, "end": v(94.13, 40.62) * mm});
            skLineSegment(sketch, "E22.33.4.5", {"start": v(94.13, 40.62) * mm, "end": v(82.58, 40.62) * mm});
            skLineSegment(sketch, "E22.0.4.6", {"start": v(63.1, 26.87) * mm, "end": v(74.64, 26.87) * mm});
            skLineSegment(sketch, "E22.3.4.6", {"start": v(57.32, 16.87) * mm, "end": v(63.1, 26.87) * mm});
            skLineSegment(sketch, "E22.6.4.6", {"start": v(63.1, 6.87) * mm, "end": v(57.32, 16.87) * mm});
            skLineSegment(sketch, "E22.9.4.6", {"start": v(74.64, 6.87) * mm, "end": v(63.1, 6.87) * mm});
            skLineSegment(sketch, "E22.12.4.6", {"start": v(80.42, 16.87) * mm, "end": v(74.64, 6.87) * mm});
            skLineSegment(sketch, "E22.15.4.6", {"start": v(74.64, 26.87) * mm, "end": v(80.42, 16.87) * mm});
            skLineSegment(sketch, "E22.18.4.6", {"start": v(76.8, 28.12) * mm, "end": v(82.58, 38.12) * mm});
            skLineSegment(sketch, "E22.21.4.6", {"start": v(82.58, 18.12) * mm, "end": v(76.8, 28.12) * mm});
            skLineSegment(sketch, "E22.24.4.6", {"start": v(82.58, 38.12) * mm, "end": v(94.13, 38.12) * mm});
            skLineSegment(sketch, "E22.27.4.6", {"start": v(94.13, 38.12) * mm, "end": v(99.9, 28.12) * mm});
            skLineSegment(sketch, "E22.30.4.6", {"start": v(99.9, 28.12) * mm, "end": v(94.13, 18.12) * mm});
            skLineSegment(sketch, "E22.33.4.6", {"start": v(94.13, 18.12) * mm, "end": v(82.58, 18.12) * mm});
            skLineSegment(sketch, "E22.0.4.7", {"start": v(63.1, 4.37) * mm, "end": v(74.64, 4.37) * mm});
            skLineSegment(sketch, "E22.3.4.7", {"start": v(57.32, -5.63) * mm, "end": v(63.1, 4.37) * mm});
            skLineSegment(sketch, "E22.6.4.7", {"start": v(63.1, -15.63) * mm, "end": v(57.32, -5.63) * mm});
            skLineSegment(sketch, "E22.9.4.7", {"start": v(74.64, -15.63) * mm, "end": v(63.1, -15.63) * mm});
            skLineSegment(sketch, "E22.12.4.7", {"start": v(80.42, -5.63) * mm, "end": v(74.64, -15.63) * mm});
            skLineSegment(sketch, "E22.15.4.7", {"start": v(74.64, 4.37) * mm, "end": v(80.42, -5.63) * mm});
            skLineSegment(sketch, "E22.18.4.7", {"start": v(76.8, 5.62) * mm, "end": v(82.58, 15.62) * mm});
            skLineSegment(sketch, "E22.21.4.7", {"start": v(82.58, -4.38) * mm, "end": v(76.8, 5.62) * mm});
            skLineSegment(sketch, "E22.24.4.7", {"start": v(82.58, 15.62) * mm, "end": v(94.13, 15.62) * mm});
            skLineSegment(sketch, "E22.27.4.7", {"start": v(94.13, 15.62) * mm, "end": v(99.9, 5.62) * mm});
            skLineSegment(sketch, "E22.30.4.7", {"start": v(99.9, 5.62) * mm, "end": v(94.13, -4.38) * mm});
            skLineSegment(sketch, "E22.33.4.7", {"start": v(94.13, -4.38) * mm, "end": v(82.58, -4.38) * mm});
            skLineSegment(sketch, "E22.0.4.8", {"start": v(63.1, -18.13) * mm, "end": v(74.64, -18.13) * mm});
            skLineSegment(sketch, "E22.3.4.8", {"start": v(57.32, -28.13) * mm, "end": v(63.1, -18.13) * mm});
            skLineSegment(sketch, "E22.6.4.8", {"start": v(63.1, -38.13) * mm, "end": v(57.32, -28.13) * mm});
            skLineSegment(sketch, "E22.9.4.8", {"start": v(74.64, -38.13) * mm, "end": v(63.1, -38.13) * mm});
            skLineSegment(sketch, "E22.12.4.8", {"start": v(80.42, -28.13) * mm, "end": v(74.64, -38.13) * mm});
            skLineSegment(sketch, "E22.15.4.8", {"start": v(74.64, -18.13) * mm, "end": v(80.42, -28.13) * mm});
            skLineSegment(sketch, "E22.18.4.8", {"start": v(76.8, -16.88) * mm, "end": v(82.58, -6.88) * mm});
            skLineSegment(sketch, "E22.21.4.8", {"start": v(82.58, -26.88) * mm, "end": v(76.8, -16.88) * mm});
            skLineSegment(sketch, "E22.24.4.8", {"start": v(82.58, -6.88) * mm, "end": v(94.13, -6.88) * mm});
            skLineSegment(sketch, "E22.27.4.8", {"start": v(94.13, -6.88) * mm, "end": v(99.9, -16.88) * mm});
            skLineSegment(sketch, "E22.30.4.8", {"start": v(99.9, -16.88) * mm, "end": v(94.13, -26.88) * mm});
            skLineSegment(sketch, "E22.33.4.8", {"start": v(94.13, -26.88) * mm, "end": v(82.58, -26.88) * mm});
            skLineSegment(sketch, "E22.0.4.9", {"start": v(63.1, -40.63) * mm, "end": v(74.64, -40.63) * mm});
            skLineSegment(sketch, "E22.3.4.9", {"start": v(57.32, -50.63) * mm, "end": v(63.1, -40.63) * mm});
            skLineSegment(sketch, "E22.6.4.9", {"start": v(63.1, -60.63) * mm, "end": v(57.32, -50.63) * mm});
            skLineSegment(sketch, "E22.9.4.9", {"start": v(74.64, -60.63) * mm, "end": v(63.1, -60.63) * mm});
            skLineSegment(sketch, "E22.12.4.9", {"start": v(80.42, -50.63) * mm, "end": v(74.64, -60.63) * mm});
            skLineSegment(sketch, "E22.15.4.9", {"start": v(74.64, -40.63) * mm, "end": v(80.42, -50.63) * mm});
            skLineSegment(sketch, "E22.18.4.9", {"start": v(76.8, -39.38) * mm, "end": v(82.58, -29.38) * mm});
            skLineSegment(sketch, "E22.21.4.9", {"start": v(82.58, -49.38) * mm, "end": v(76.8, -39.38) * mm});
            skLineSegment(sketch, "E22.24.4.9", {"start": v(82.58, -29.38) * mm, "end": v(94.13, -29.38) * mm});
            skLineSegment(sketch, "E22.27.4.9", {"start": v(94.13, -29.38) * mm, "end": v(99.9, -39.38) * mm});
            skLineSegment(sketch, "E22.30.4.9", {"start": v(99.9, -39.38) * mm, "end": v(94.13, -49.38) * mm});
            skLineSegment(sketch, "E22.33.4.9", {"start": v(94.13, -49.38) * mm, "end": v(82.58, -49.38) * mm});
            skLineSegment(sketch, "E22.0.4.10", {"start": v(63.1, -63.13) * mm, "end": v(74.64, -63.13) * mm});
            skLineSegment(sketch, "E22.3.4.10", {"start": v(57.32, -73.13) * mm, "end": v(63.1, -63.13) * mm});
            skLineSegment(sketch, "E22.6.4.10", {"start": v(63.1, -83.13) * mm, "end": v(57.32, -73.13) * mm});
            skLineSegment(sketch, "E22.9.4.10", {"start": v(74.64, -83.13) * mm, "end": v(63.1, -83.13) * mm});
            skLineSegment(sketch, "E22.12.4.10", {"start": v(80.42, -73.13) * mm, "end": v(74.64, -83.13) * mm});
            skLineSegment(sketch, "E22.15.4.10", {"start": v(74.64, -63.13) * mm, "end": v(80.42, -73.13) * mm});
            skLineSegment(sketch, "E22.18.4.10", {"start": v(76.8, -61.88) * mm, "end": v(82.58, -51.88) * mm});
            skLineSegment(sketch, "E22.21.4.10", {"start": v(82.58, -71.88) * mm, "end": v(76.8, -61.88) * mm});
            skLineSegment(sketch, "E22.24.4.10", {"start": v(82.58, -51.88) * mm, "end": v(94.13, -51.88) * mm});
            skLineSegment(sketch, "E22.27.4.10", {"start": v(94.13, -51.88) * mm, "end": v(99.9, -61.88) * mm});
            skLineSegment(sketch, "E22.30.4.10", {"start": v(99.9, -61.88) * mm, "end": v(94.13, -71.88) * mm});
            skLineSegment(sketch, "E22.33.4.10", {"start": v(94.13, -71.88) * mm, "end": v(82.58, -71.88) * mm});
            skLineSegment(sketch, "E22.0.4.11", {"start": v(63.1, -85.63) * mm, "end": v(74.64, -85.63) * mm});
            skLineSegment(sketch, "E22.3.4.11", {"start": v(57.32, -95.63) * mm, "end": v(63.1, -85.63) * mm});
            skLineSegment(sketch, "E22.6.4.11", {"start": v(63.1, -105.63) * mm, "end": v(57.32, -95.63) * mm});
            skLineSegment(sketch, "E22.9.4.11", {"start": v(74.64, -105.63) * mm, "end": v(63.1, -105.63) * mm});
            skLineSegment(sketch, "E22.12.4.11", {"start": v(80.42, -95.63) * mm, "end": v(74.64, -105.63) * mm});
            skLineSegment(sketch, "E22.15.4.11", {"start": v(74.64, -85.62) * mm, "end": v(80.42, -95.63) * mm});
            skLineSegment(sketch, "E22.18.4.11", {"start": v(76.8, -84.38) * mm, "end": v(82.58, -74.38) * mm});
            skLineSegment(sketch, "E22.21.4.11", {"start": v(82.58, -94.37) * mm, "end": v(76.8, -84.38) * mm});
            skLineSegment(sketch, "E22.24.4.11", {"start": v(82.58, -74.38) * mm, "end": v(94.13, -74.38) * mm});
            skLineSegment(sketch, "E22.27.4.11", {"start": v(94.13, -74.38) * mm, "end": v(99.9, -84.38) * mm});
            skLineSegment(sketch, "E22.30.4.11", {"start": v(99.9, -84.38) * mm, "end": v(94.13, -94.38) * mm});
            skLineSegment(sketch, "E22.33.4.11", {"start": v(94.13, -94.38) * mm, "end": v(82.58, -94.38) * mm});
            skLineSegment(sketch, "E22.0.4.12", {"start": v(63.1, -108.13) * mm, "end": v(74.64, -108.13) * mm});
            skLineSegment(sketch, "E22.3.4.12", {"start": v(57.32, -118.13) * mm, "end": v(63.1, -108.13) * mm});
            skLineSegment(sketch, "E22.6.4.12", {"start": v(63.1, -128.13) * mm, "end": v(57.32, -118.13) * mm});
            skLineSegment(sketch, "E22.9.4.12", {"start": v(74.64, -128.13) * mm, "end": v(63.1, -128.13) * mm});
            skLineSegment(sketch, "E22.12.4.12", {"start": v(80.42, -118.13) * mm, "end": v(74.64, -128.13) * mm});
            skLineSegment(sketch, "E22.15.4.12", {"start": v(74.64, -108.12) * mm, "end": v(80.42, -118.13) * mm});
            skLineSegment(sketch, "E22.18.4.12", {"start": v(76.8, -106.88) * mm, "end": v(82.58, -96.88) * mm});
            skLineSegment(sketch, "E22.21.4.12", {"start": v(82.58, -116.87) * mm, "end": v(76.8, -106.88) * mm});
            skLineSegment(sketch, "E22.24.4.12", {"start": v(82.58, -96.88) * mm, "end": v(94.13, -96.88) * mm});
            skLineSegment(sketch, "E22.27.4.12", {"start": v(94.13, -96.88) * mm, "end": v(99.9, -106.88) * mm});
            skLineSegment(sketch, "E22.30.4.12", {"start": v(99.9, -106.88) * mm, "end": v(94.13, -116.88) * mm});
            skLineSegment(sketch, "E22.33.4.12", {"start": v(94.13, -116.88) * mm, "end": v(82.58, -116.88) * mm});
            skLineSegment(sketch, "E22.0.4.13", {"start": v(63.1, -130.62) * mm, "end": v(74.64, -130.62) * mm});
            skLineSegment(sketch, "E22.3.4.13", {"start": v(57.32, -140.63) * mm, "end": v(63.1, -130.63) * mm});
            skLineSegment(sketch, "E22.6.4.13", {"start": v(63.1, -150.63) * mm, "end": v(57.32, -140.63) * mm});
            skLineSegment(sketch, "E22.9.4.13", {"start": v(74.64, -150.62) * mm, "end": v(63.1, -150.62) * mm});
            skLineSegment(sketch, "E22.12.4.13", {"start": v(80.42, -140.62) * mm, "end": v(74.64, -150.62) * mm});
            skLineSegment(sketch, "E22.15.4.13", {"start": v(74.64, -130.62) * mm, "end": v(80.42, -140.62) * mm});
            skLineSegment(sketch, "E22.18.4.13", {"start": v(76.8, -129.38) * mm, "end": v(82.58, -119.38) * mm});
            skLineSegment(sketch, "E22.21.4.13", {"start": v(82.58, -139.37) * mm, "end": v(76.8, -129.38) * mm});
            skLineSegment(sketch, "E22.24.4.13", {"start": v(82.58, -119.37) * mm, "end": v(94.13, -119.37) * mm});
            skLineSegment(sketch, "E22.27.4.13", {"start": v(94.13, -119.38) * mm, "end": v(99.9, -129.37) * mm});
            skLineSegment(sketch, "E22.30.4.13", {"start": v(99.9, -129.38) * mm, "end": v(94.13, -139.38) * mm});
            skLineSegment(sketch, "E22.33.4.13", {"start": v(94.13, -139.38) * mm, "end": v(82.58, -139.38) * mm});
            skLineSegment(sketch, "E22.0.4.14", {"start": v(63.1, -153.12) * mm, "end": v(74.64, -153.12) * mm});
            skLineSegment(sketch, "E22.3.4.14", {"start": v(57.32, -163.13) * mm, "end": v(63.1, -153.13) * mm});
            skLineSegment(sketch, "E22.6.4.14", {"start": v(63.1, -173.13) * mm, "end": v(57.32, -163.13) * mm});
            skLineSegment(sketch, "E22.9.4.14", {"start": v(74.64, -173.13) * mm, "end": v(63.1, -173.13) * mm});
            skLineSegment(sketch, "E22.12.4.14", {"start": v(80.42, -163.13) * mm, "end": v(74.64, -173.13) * mm});
            skLineSegment(sketch, "E22.15.4.14", {"start": v(74.64, -153.12) * mm, "end": v(80.42, -163.12) * mm});
            skLineSegment(sketch, "E22.18.4.14", {"start": v(76.8, -151.88) * mm, "end": v(82.58, -141.88) * mm});
            skLineSegment(sketch, "E22.21.4.14", {"start": v(82.58, -161.87) * mm, "end": v(76.8, -151.88) * mm});
            skLineSegment(sketch, "E22.24.4.14", {"start": v(82.58, -141.88) * mm, "end": v(94.13, -141.88) * mm});
            skLineSegment(sketch, "E22.27.4.14", {"start": v(94.13, -141.88) * mm, "end": v(99.9, -151.87) * mm});
            skLineSegment(sketch, "E22.30.4.14", {"start": v(99.9, -151.88) * mm, "end": v(94.13, -161.88) * mm});
            skLineSegment(sketch, "E22.33.4.14", {"start": v(94.13, -161.88) * mm, "end": v(82.58, -161.88) * mm});
            skLineSegment(sketch, "E23.0", {"start": v(50.12, 147.52) * mm, "end": v(87.5, 118.77) * mm});
            skLineSegment(sketch, "E24.0", {"start": v(87.5, -118.77) * mm, "end": v(50.12, -147.52) * mm});
            skSolve(sketch);
        }
        {
            var Q0;
            {var subQ0=sQuery(id+"F4.wireOp",EDGE,"E17.0");var subQ1=sQuery(id+"F4.wireOp",EDGE,"E12");var subQ2=makeQuery(id+"F4.imprint","INTERSECT",VERTEX,{"derivedFrom":[subQ1,subQ0]});Q0=makeQuery(id+"F4.imprint","IMPRINT",FACE,{"disambiguationData":[TD([[makeQuery(id+"F4.imprint","IMPRINT",EDGE,{"disambiguationData":[TD([[subQ2,-1.0]])],"derivedFrom":subQ1}),-1.0]])]});}
            var Q1;
            {var subQ4=sQuery(id+"F4.wireOp",EDGE,"E20.0.1.7");Q1=makeQuery(id+"F4.imprint","IMPRINT",FACE,{"disambiguationData":[TD([[makeQuery(id+"F4.imprint","IMPRINT",EDGE,{"derivedFrom":subQ4}),-1.0]])]});}
            var Q2;
            {var subQ5=sQuery(id+"F4.wireOp",EDGE,"E20.1.0.3");Q2=makeQuery(id+"F4.imprint","IMPRINT",FACE,{"disambiguationData":[TD([[makeQuery(id+"F4.imprint","IMPRINT",EDGE,{"derivedFrom":subQ5}),-1.0]])]});}
            var Q3;
            {var subQ4=sQuery(id+"F4.wireOp",EDGE,"E20.1.1.7");Q3=makeQuery(id+"F4.imprint","IMPRINT",FACE,{"disambiguationData":[TD([[makeQuery(id+"F4.imprint","IMPRINT",EDGE,{"derivedFrom":subQ4}),-1.0]])]});}
            var Q4;
            {var subQ5=sQuery(id+"F4.wireOp",EDGE,"E20.2.0.3");Q4=makeQuery(id+"F4.imprint","IMPRINT",FACE,{"disambiguationData":[TD([[makeQuery(id+"F4.imprint","IMPRINT",EDGE,{"derivedFrom":subQ5}),-1.0]])]});}
            var Q5;
            {var subQ0=sQuery(id+"F4.wireOp",EDGE,"E20.2.1.7");Q5=makeQuery(id+"F4.imprint","IMPRINT",FACE,{"disambiguationData":[TD([[makeQuery(id+"F4.imprint","IMPRINT",EDGE,{"derivedFrom":subQ0}),-1.0]])]});}
            var Q6;
            {var subQ5=sQuery(id+"F4.wireOp",EDGE,"E21.9.3.0");Q6=makeQuery(id+"F4.imprint","IMPRINT",FACE,{"disambiguationData":[TD([[makeQuery(id+"F4.imprint","IMPRINT",EDGE,{"derivedFrom":subQ5}),-1.0]])]});}
            var Q7;
            {var subQ0=sQuery(id+"F4.wireOp",EDGE,"E21.21.3.1");Q7=makeQuery(id+"F4.imprint","IMPRINT",FACE,{"disambiguationData":[TD([[makeQuery(id+"F4.imprint","IMPRINT",EDGE,{"derivedFrom":subQ0}),-1.0]])]});}
            var Q8;
            {var subQ0=sQuery(id+"F4.wireOp",EDGE,"E20.0.1.4");Q8=makeQuery(id+"F4.imprint","IMPRINT",FACE,{"disambiguationData":[TD([[makeQuery(id+"F4.imprint","IMPRINT",EDGE,{"derivedFrom":subQ0}),-1.0]])]});}
            var Q9;
            Q9=makeQuery(id+"F4.imprint","IMPRINT",FACE,{"disambiguationData":[TD([[makeQuery(id+"F4.imprint","IMPRINT",EDGE,{"derivedFrom":sQuery(id+"F4.wireOp",EDGE,"E20.1.1.0")}),-1.0]])]});
            var Q10;
            Q10=makeQuery(id+"F4.imprint","IMPRINT",FACE,{"disambiguationData":[TD([[makeQuery(id+"F4.imprint","IMPRINT",EDGE,{"derivedFrom":sQuery(id+"F4.wireOp",EDGE,"E20.2.1.0")}),-1.0]])]});
            var Q11;
            Q11=makeQuery(id+"F4.imprint","IMPRINT",FACE,{"disambiguationData":[TD([[makeQuery(id+"F4.imprint","IMPRINT",EDGE,{"derivedFrom":sQuery(id+"F4.wireOp",EDGE,"E21.0.3.1")}),-1.0]])]});
            var Q12;
            Q12=makeQuery(id+"F4.imprint","IMPRINT",FACE,{"disambiguationData":[TD([[makeQuery(id+"F4.imprint","IMPRINT",EDGE,{"derivedFrom":sQuery(id+"F4.wireOp",EDGE,"E22.18.0.2")}),-1.0]])]});
            var Q13;
            Q13=makeQuery(id+"F4.imprint","IMPRINT",FACE,{"disambiguationData":[TD([[makeQuery(id+"F4.imprint","IMPRINT",EDGE,{"derivedFrom":sQuery(id+"F4.wireOp",EDGE,"E22.18.1.2")}),-1.0]])]});
            var Q14;
            Q14=makeQuery(id+"F4.imprint","IMPRINT",FACE,{"disambiguationData":[TD([[makeQuery(id+"F4.imprint","IMPRINT",EDGE,{"derivedFrom":sQuery(id+"F4.wireOp",EDGE,"E22.18.2.2")}),-1.0]])]});
            var Q15;
            Q15=makeQuery(id+"F4.imprint","IMPRINT",FACE,{"disambiguationData":[TD([[makeQuery(id+"F4.imprint","IMPRINT",EDGE,{"derivedFrom":sQuery(id+"F4.wireOp",EDGE,"E22.18.3.2")}),-1.0]])]});
            var Q16;
            {var subQ0=sQuery(id+"F4.wireOp",EDGE,"E22.12.0.2");Q16=makeQuery(id+"F4.imprint","IMPRINT",FACE,{"disambiguationData":[TD([[makeQuery(id+"F4.imprint","IMPRINT",EDGE,{"derivedFrom":subQ0}),-1.0]])]});}
            var Q17;
            Q17=makeQuery(id+"F4.imprint","IMPRINT",FACE,{"disambiguationData":[TD([[makeQuery(id+"F4.imprint","IMPRINT",EDGE,{"derivedFrom":sQuery(id+"F4.wireOp",EDGE,"E22.0.1.2")}),-1.0]])]});
            var Q18;
            Q18=makeQuery(id+"F4.imprint","IMPRINT",FACE,{"disambiguationData":[TD([[makeQuery(id+"F4.imprint","IMPRINT",EDGE,{"derivedFrom":sQuery(id+"F4.wireOp",EDGE,"E22.0.2.2")}),-1.0]])]});
            var Q19;
            Q19=makeQuery(id+"F4.imprint","IMPRINT",FACE,{"disambiguationData":[TD([[makeQuery(id+"F4.imprint","IMPRINT",EDGE,{"derivedFrom":sQuery(id+"F4.wireOp",EDGE,"E22.0.3.2")}),-1.0]])]});
            var Q20;
            Q20=makeQuery(id+"F4.imprint","IMPRINT",FACE,{"disambiguationData":[TD([[makeQuery(id+"F4.imprint","IMPRINT",EDGE,{"derivedFrom":sQuery(id+"F4.wireOp",EDGE,"E22.0.4.2")}),-1.0]])]});
            var Q21;
            Q21=makeQuery(id+"F4.imprint","IMPRINT",FACE,{"disambiguationData":[TD([[makeQuery(id+"F4.imprint","IMPRINT",EDGE,{"derivedFrom":sQuery(id+"F4.wireOp",EDGE,"E22.18.0.3")}),-1.0]])]});
            var Q22;
            Q22=makeQuery(id+"F4.imprint","IMPRINT",FACE,{"disambiguationData":[TD([[makeQuery(id+"F4.imprint","IMPRINT",EDGE,{"derivedFrom":sQuery(id+"F4.wireOp",EDGE,"E22.18.1.3")}),-1.0]])]});
            var Q23;
            Q23=makeQuery(id+"F4.imprint","IMPRINT",FACE,{"disambiguationData":[TD([[makeQuery(id+"F4.imprint","IMPRINT",EDGE,{"derivedFrom":sQuery(id+"F4.wireOp",EDGE,"E22.18.2.3")}),-1.0]])]});
            var Q24;
            Q24=makeQuery(id+"F4.imprint","IMPRINT",FACE,{"disambiguationData":[TD([[makeQuery(id+"F4.imprint","IMPRINT",EDGE,{"derivedFrom":sQuery(id+"F4.wireOp",EDGE,"E22.18.3.3")}),-1.0]])]});
            var Q25;
            {var subQ1=sQuery(id+"F4.wireOp",EDGE,"E22.18.4.3");Q25=makeQuery(id+"F4.imprint","IMPRINT",FACE,{"disambiguationData":[TD([[makeQuery(id+"F4.imprint","IMPRINT",EDGE,{"derivedFrom":subQ1}),-1.0]])]});}
            var Q26;
            {var subQ0=sQuery(id+"F4.wireOp",EDGE,"E22.12.0.3");Q26=makeQuery(id+"F4.imprint","IMPRINT",FACE,{"disambiguationData":[TD([[makeQuery(id+"F4.imprint","IMPRINT",EDGE,{"derivedFrom":subQ0}),-1.0]])]});}
            var Q27;
            Q27=makeQuery(id+"F4.imprint","IMPRINT",FACE,{"disambiguationData":[TD([[makeQuery(id+"F4.imprint","IMPRINT",EDGE,{"derivedFrom":sQuery(id+"F4.wireOp",EDGE,"E22.0.1.3")}),-1.0]])]});
            var Q28;
            Q28=makeQuery(id+"F4.imprint","IMPRINT",FACE,{"disambiguationData":[TD([[makeQuery(id+"F4.imprint","IMPRINT",EDGE,{"derivedFrom":sQuery(id+"F4.wireOp",EDGE,"E22.0.2.3")}),-1.0]])]});
            var Q29;
            Q29=makeQuery(id+"F4.imprint","IMPRINT",FACE,{"disambiguationData":[TD([[makeQuery(id+"F4.imprint","IMPRINT",EDGE,{"derivedFrom":sQuery(id+"F4.wireOp",EDGE,"E22.0.3.3")}),-1.0]])]});
            var Q30;
            Q30=makeQuery(id+"F4.imprint","IMPRINT",FACE,{"disambiguationData":[TD([[makeQuery(id+"F4.imprint","IMPRINT",EDGE,{"derivedFrom":sQuery(id+"F4.wireOp",EDGE,"E22.0.4.3")}),-1.0]])]});
            var Q31;
            Q31=makeQuery(id+"F4.imprint","IMPRINT",FACE,{"disambiguationData":[TD([[makeQuery(id+"F4.imprint","IMPRINT",EDGE,{"derivedFrom":sQuery(id+"F4.wireOp",EDGE,"E22.18.0.4")}),-1.0]])]});
            var Q32;
            Q32=makeQuery(id+"F4.imprint","IMPRINT",FACE,{"disambiguationData":[TD([[makeQuery(id+"F4.imprint","IMPRINT",EDGE,{"derivedFrom":sQuery(id+"F4.wireOp",EDGE,"E22.18.1.4")}),-1.0]])]});
            var Q33;
            Q33=makeQuery(id+"F4.imprint","IMPRINT",FACE,{"disambiguationData":[TD([[makeQuery(id+"F4.imprint","IMPRINT",EDGE,{"derivedFrom":sQuery(id+"F4.wireOp",EDGE,"E22.18.2.4")}),-1.0]])]});
            var Q34;
            Q34=makeQuery(id+"F4.imprint","IMPRINT",FACE,{"disambiguationData":[TD([[makeQuery(id+"F4.imprint","IMPRINT",EDGE,{"derivedFrom":sQuery(id+"F4.wireOp",EDGE,"E22.18.3.4")}),-1.0]])]});
            var Q35;
            {var subQ1=sQuery(id+"F4.wireOp",EDGE,"E22.18.4.4");Q35=makeQuery(id+"F4.imprint","IMPRINT",FACE,{"disambiguationData":[TD([[makeQuery(id+"F4.imprint","IMPRINT",EDGE,{"derivedFrom":subQ1}),-1.0]])]});}
            var Q36;
            {var subQ0=sQuery(id+"F4.wireOp",EDGE,"E22.12.0.4");Q36=makeQuery(id+"F4.imprint","IMPRINT",FACE,{"disambiguationData":[TD([[makeQuery(id+"F4.imprint","IMPRINT",EDGE,{"derivedFrom":subQ0}),-1.0]])]});}
            var Q37;
            Q37=makeQuery(id+"F4.imprint","IMPRINT",FACE,{"disambiguationData":[TD([[makeQuery(id+"F4.imprint","IMPRINT",EDGE,{"derivedFrom":sQuery(id+"F4.wireOp",EDGE,"E22.0.1.4")}),-1.0]])]});
            var Q38;
            Q38=makeQuery(id+"F4.imprint","IMPRINT",FACE,{"disambiguationData":[TD([[makeQuery(id+"F4.imprint","IMPRINT",EDGE,{"derivedFrom":sQuery(id+"F4.wireOp",EDGE,"E22.0.2.4")}),-1.0]])]});
            var Q39;
            Q39=makeQuery(id+"F4.imprint","IMPRINT",FACE,{"disambiguationData":[TD([[makeQuery(id+"F4.imprint","IMPRINT",EDGE,{"derivedFrom":sQuery(id+"F4.wireOp",EDGE,"E22.0.3.4")}),-1.0]])]});
            var Q40;
            Q40=makeQuery(id+"F4.imprint","IMPRINT",FACE,{"disambiguationData":[TD([[makeQuery(id+"F4.imprint","IMPRINT",EDGE,{"derivedFrom":sQuery(id+"F4.wireOp",EDGE,"E22.0.4.4")}),-1.0]])]});
            var Q41;
            Q41=makeQuery(id+"F4.imprint","IMPRINT",FACE,{"disambiguationData":[TD([[makeQuery(id+"F4.imprint","IMPRINT",EDGE,{"derivedFrom":sQuery(id+"F4.wireOp",EDGE,"E22.18.0.5")}),-1.0]])]});
            var Q42;
            Q42=makeQuery(id+"F4.imprint","IMPRINT",FACE,{"disambiguationData":[TD([[makeQuery(id+"F4.imprint","IMPRINT",EDGE,{"derivedFrom":sQuery(id+"F4.wireOp",EDGE,"E22.18.1.5")}),-1.0]])]});
            var Q43;
            Q43=makeQuery(id+"F4.imprint","IMPRINT",FACE,{"disambiguationData":[TD([[makeQuery(id+"F4.imprint","IMPRINT",EDGE,{"derivedFrom":sQuery(id+"F4.wireOp",EDGE,"E22.18.2.5")}),-1.0]])]});
            var Q44;
            Q44=makeQuery(id+"F4.imprint","IMPRINT",FACE,{"disambiguationData":[TD([[makeQuery(id+"F4.imprint","IMPRINT",EDGE,{"derivedFrom":sQuery(id+"F4.wireOp",EDGE,"E22.18.3.5")}),-1.0]])]});
            var Q45;
            {var subQ1=sQuery(id+"F4.wireOp",EDGE,"E22.18.4.5");Q45=makeQuery(id+"F4.imprint","IMPRINT",FACE,{"disambiguationData":[TD([[makeQuery(id+"F4.imprint","IMPRINT",EDGE,{"derivedFrom":subQ1}),-1.0]])]});}
            var Q46;
            {var subQ0=sQuery(id+"F4.wireOp",EDGE,"E22.12.0.5");Q46=makeQuery(id+"F4.imprint","IMPRINT",FACE,{"disambiguationData":[TD([[makeQuery(id+"F4.imprint","IMPRINT",EDGE,{"derivedFrom":subQ0}),-1.0]])]});}
            var Q47;
            Q47=makeQuery(id+"F4.imprint","IMPRINT",FACE,{"disambiguationData":[TD([[makeQuery(id+"F4.imprint","IMPRINT",EDGE,{"derivedFrom":sQuery(id+"F4.wireOp",EDGE,"E22.0.1.5")}),-1.0]])]});
            var Q48;
            Q48=makeQuery(id+"F4.imprint","IMPRINT",FACE,{"disambiguationData":[TD([[makeQuery(id+"F4.imprint","IMPRINT",EDGE,{"derivedFrom":sQuery(id+"F4.wireOp",EDGE,"E22.0.2.5")}),-1.0]])]});
            var Q49;
            Q49=makeQuery(id+"F4.imprint","IMPRINT",FACE,{"disambiguationData":[TD([[makeQuery(id+"F4.imprint","IMPRINT",EDGE,{"derivedFrom":sQuery(id+"F4.wireOp",EDGE,"E22.0.3.5")}),-1.0]])]});
            var Q50;
            Q50=makeQuery(id+"F4.imprint","IMPRINT",FACE,{"disambiguationData":[TD([[makeQuery(id+"F4.imprint","IMPRINT",EDGE,{"derivedFrom":sQuery(id+"F4.wireOp",EDGE,"E22.0.4.5")}),-1.0]])]});
            var Q51;
            Q51=makeQuery(id+"F4.imprint","IMPRINT",FACE,{"disambiguationData":[TD([[makeQuery(id+"F4.imprint","IMPRINT",EDGE,{"derivedFrom":sQuery(id+"F4.wireOp",EDGE,"E22.18.0.6")}),-1.0]])]});
            var Q52;
            Q52=makeQuery(id+"F4.imprint","IMPRINT",FACE,{"disambiguationData":[TD([[makeQuery(id+"F4.imprint","IMPRINT",EDGE,{"derivedFrom":sQuery(id+"F4.wireOp",EDGE,"E22.18.1.6")}),-1.0]])]});
            var Q53;
            Q53=makeQuery(id+"F4.imprint","IMPRINT",FACE,{"disambiguationData":[TD([[makeQuery(id+"F4.imprint","IMPRINT",EDGE,{"derivedFrom":sQuery(id+"F4.wireOp",EDGE,"E22.18.2.6")}),-1.0]])]});
            var Q54;
            Q54=makeQuery(id+"F4.imprint","IMPRINT",FACE,{"disambiguationData":[TD([[makeQuery(id+"F4.imprint","IMPRINT",EDGE,{"derivedFrom":sQuery(id+"F4.wireOp",EDGE,"E22.18.3.6")}),-1.0]])]});
            var Q55;
            {var subQ1=sQuery(id+"F4.wireOp",EDGE,"E22.18.4.6");Q55=makeQuery(id+"F4.imprint","IMPRINT",FACE,{"disambiguationData":[TD([[makeQuery(id+"F4.imprint","IMPRINT",EDGE,{"derivedFrom":subQ1}),-1.0]])]});}
            var Q56;
            {var subQ0=sQuery(id+"F4.wireOp",EDGE,"E22.12.0.6");Q56=makeQuery(id+"F4.imprint","IMPRINT",FACE,{"disambiguationData":[TD([[makeQuery(id+"F4.imprint","IMPRINT",EDGE,{"derivedFrom":subQ0}),-1.0]])]});}
            var Q57;
            Q57=makeQuery(id+"F4.imprint","IMPRINT",FACE,{"disambiguationData":[TD([[makeQuery(id+"F4.imprint","IMPRINT",EDGE,{"derivedFrom":sQuery(id+"F4.wireOp",EDGE,"E22.0.1.6")}),-1.0]])]});
            var Q58;
            Q58=makeQuery(id+"F4.imprint","IMPRINT",FACE,{"disambiguationData":[TD([[makeQuery(id+"F4.imprint","IMPRINT",EDGE,{"derivedFrom":sQuery(id+"F4.wireOp",EDGE,"E22.0.2.6")}),-1.0]])]});
            var Q59;
            Q59=makeQuery(id+"F4.imprint","IMPRINT",FACE,{"disambiguationData":[TD([[makeQuery(id+"F4.imprint","IMPRINT",EDGE,{"derivedFrom":sQuery(id+"F4.wireOp",EDGE,"E22.0.3.6")}),-1.0]])]});
            var Q60;
            Q60=makeQuery(id+"F4.imprint","IMPRINT",FACE,{"disambiguationData":[TD([[makeQuery(id+"F4.imprint","IMPRINT",EDGE,{"derivedFrom":sQuery(id+"F4.wireOp",EDGE,"E22.0.4.6")}),-1.0]])]});
            var Q61;
            Q61=makeQuery(id+"F4.imprint","IMPRINT",FACE,{"disambiguationData":[TD([[makeQuery(id+"F4.imprint","IMPRINT",EDGE,{"derivedFrom":sQuery(id+"F4.wireOp",EDGE,"E22.18.0.7")}),-1.0]])]});
            var Q62;
            Q62=makeQuery(id+"F4.imprint","IMPRINT",FACE,{"disambiguationData":[TD([[makeQuery(id+"F4.imprint","IMPRINT",EDGE,{"derivedFrom":sQuery(id+"F4.wireOp",EDGE,"E22.18.1.7")}),-1.0]])]});
            var Q63;
            Q63=makeQuery(id+"F4.imprint","IMPRINT",FACE,{"disambiguationData":[TD([[makeQuery(id+"F4.imprint","IMPRINT",EDGE,{"derivedFrom":sQuery(id+"F4.wireOp",EDGE,"E22.18.2.7")}),-1.0]])]});
            var Q64;
            Q64=makeQuery(id+"F4.imprint","IMPRINT",FACE,{"disambiguationData":[TD([[makeQuery(id+"F4.imprint","IMPRINT",EDGE,{"derivedFrom":sQuery(id+"F4.wireOp",EDGE,"E22.18.3.7")}),-1.0]])]});
            var Q65;
            {var subQ1=sQuery(id+"F4.wireOp",EDGE,"E22.18.4.7");Q65=makeQuery(id+"F4.imprint","IMPRINT",FACE,{"disambiguationData":[TD([[makeQuery(id+"F4.imprint","IMPRINT",EDGE,{"derivedFrom":subQ1}),-1.0]])]});}
            var Q66;
            {var subQ0=sQuery(id+"F4.wireOp",EDGE,"E22.12.0.7");Q66=makeQuery(id+"F4.imprint","IMPRINT",FACE,{"disambiguationData":[TD([[makeQuery(id+"F4.imprint","IMPRINT",EDGE,{"derivedFrom":subQ0}),-1.0]])]});}
            var Q67;
            Q67=makeQuery(id+"F4.imprint","IMPRINT",FACE,{"disambiguationData":[TD([[makeQuery(id+"F4.imprint","IMPRINT",EDGE,{"derivedFrom":sQuery(id+"F4.wireOp",EDGE,"E22.0.1.7")}),-1.0]])]});
            var Q68;
            Q68=makeQuery(id+"F4.imprint","IMPRINT",FACE,{"disambiguationData":[TD([[makeQuery(id+"F4.imprint","IMPRINT",EDGE,{"derivedFrom":sQuery(id+"F4.wireOp",EDGE,"E22.0.2.7")}),-1.0]])]});
            var Q69;
            Q69=makeQuery(id+"F4.imprint","IMPRINT",FACE,{"disambiguationData":[TD([[makeQuery(id+"F4.imprint","IMPRINT",EDGE,{"derivedFrom":sQuery(id+"F4.wireOp",EDGE,"E22.0.3.7")}),-1.0]])]});
            var Q70;
            Q70=makeQuery(id+"F4.imprint","IMPRINT",FACE,{"disambiguationData":[TD([[makeQuery(id+"F4.imprint","IMPRINT",EDGE,{"derivedFrom":sQuery(id+"F4.wireOp",EDGE,"E22.0.4.7")}),-1.0]])]});
            var Q71;
            Q71=makeQuery(id+"F4.imprint","IMPRINT",FACE,{"disambiguationData":[TD([[makeQuery(id+"F4.imprint","IMPRINT",EDGE,{"derivedFrom":sQuery(id+"F4.wireOp",EDGE,"E22.18.0.8")}),-1.0]])]});
            var Q72;
            Q72=makeQuery(id+"F4.imprint","IMPRINT",FACE,{"disambiguationData":[TD([[makeQuery(id+"F4.imprint","IMPRINT",EDGE,{"derivedFrom":sQuery(id+"F4.wireOp",EDGE,"E22.18.1.8")}),-1.0]])]});
            var Q73;
            Q73=makeQuery(id+"F4.imprint","IMPRINT",FACE,{"disambiguationData":[TD([[makeQuery(id+"F4.imprint","IMPRINT",EDGE,{"derivedFrom":sQuery(id+"F4.wireOp",EDGE,"E22.18.2.8")}),-1.0]])]});
            var Q74;
            Q74=makeQuery(id+"F4.imprint","IMPRINT",FACE,{"disambiguationData":[TD([[makeQuery(id+"F4.imprint","IMPRINT",EDGE,{"derivedFrom":sQuery(id+"F4.wireOp",EDGE,"E22.18.3.8")}),-1.0]])]});
            var Q75;
            {var subQ1=sQuery(id+"F4.wireOp",EDGE,"E22.18.4.8");Q75=makeQuery(id+"F4.imprint","IMPRINT",FACE,{"disambiguationData":[TD([[makeQuery(id+"F4.imprint","IMPRINT",EDGE,{"derivedFrom":subQ1}),-1.0]])]});}
            var Q76;
            {var subQ0=sQuery(id+"F4.wireOp",EDGE,"E22.12.0.8");Q76=makeQuery(id+"F4.imprint","IMPRINT",FACE,{"disambiguationData":[TD([[makeQuery(id+"F4.imprint","IMPRINT",EDGE,{"derivedFrom":subQ0}),-1.0]])]});}
            var Q77;
            Q77=makeQuery(id+"F4.imprint","IMPRINT",FACE,{"disambiguationData":[TD([[makeQuery(id+"F4.imprint","IMPRINT",EDGE,{"derivedFrom":sQuery(id+"F4.wireOp",EDGE,"E22.0.1.8")}),-1.0]])]});
            var Q78;
            Q78=makeQuery(id+"F4.imprint","IMPRINT",FACE,{"disambiguationData":[TD([[makeQuery(id+"F4.imprint","IMPRINT",EDGE,{"derivedFrom":sQuery(id+"F4.wireOp",EDGE,"E22.0.2.8")}),-1.0]])]});
            var Q79;
            Q79=makeQuery(id+"F4.imprint","IMPRINT",FACE,{"disambiguationData":[TD([[makeQuery(id+"F4.imprint","IMPRINT",EDGE,{"derivedFrom":sQuery(id+"F4.wireOp",EDGE,"E22.0.3.8")}),-1.0]])]});
            var Q80;
            Q80=makeQuery(id+"F4.imprint","IMPRINT",FACE,{"disambiguationData":[TD([[makeQuery(id+"F4.imprint","IMPRINT",EDGE,{"derivedFrom":sQuery(id+"F4.wireOp",EDGE,"E22.0.4.8")}),-1.0]])]});
            var Q81;
            Q81=makeQuery(id+"F4.imprint","IMPRINT",FACE,{"disambiguationData":[TD([[makeQuery(id+"F4.imprint","IMPRINT",EDGE,{"derivedFrom":sQuery(id+"F4.wireOp",EDGE,"E22.18.0.9")}),-1.0]])]});
            var Q82;
            Q82=makeQuery(id+"F4.imprint","IMPRINT",FACE,{"disambiguationData":[TD([[makeQuery(id+"F4.imprint","IMPRINT",EDGE,{"derivedFrom":sQuery(id+"F4.wireOp",EDGE,"E22.18.1.9")}),-1.0]])]});
            var Q83;
            Q83=makeQuery(id+"F4.imprint","IMPRINT",FACE,{"disambiguationData":[TD([[makeQuery(id+"F4.imprint","IMPRINT",EDGE,{"derivedFrom":sQuery(id+"F4.wireOp",EDGE,"E22.18.2.9")}),-1.0]])]});
            var Q84;
            Q84=makeQuery(id+"F4.imprint","IMPRINT",FACE,{"disambiguationData":[TD([[makeQuery(id+"F4.imprint","IMPRINT",EDGE,{"derivedFrom":sQuery(id+"F4.wireOp",EDGE,"E22.18.3.9")}),-1.0]])]});
            var Q85;
            {var subQ1=sQuery(id+"F4.wireOp",EDGE,"E22.18.4.9");Q85=makeQuery(id+"F4.imprint","IMPRINT",FACE,{"disambiguationData":[TD([[makeQuery(id+"F4.imprint","IMPRINT",EDGE,{"derivedFrom":subQ1}),-1.0]])]});}
            var Q86;
            {var subQ0=sQuery(id+"F4.wireOp",EDGE,"E22.12.0.9");Q86=makeQuery(id+"F4.imprint","IMPRINT",FACE,{"disambiguationData":[TD([[makeQuery(id+"F4.imprint","IMPRINT",EDGE,{"derivedFrom":subQ0}),-1.0]])]});}
            var Q87;
            Q87=makeQuery(id+"F4.imprint","IMPRINT",FACE,{"disambiguationData":[TD([[makeQuery(id+"F4.imprint","IMPRINT",EDGE,{"derivedFrom":sQuery(id+"F4.wireOp",EDGE,"E22.0.1.9")}),-1.0]])]});
            var Q88;
            Q88=makeQuery(id+"F4.imprint","IMPRINT",FACE,{"disambiguationData":[TD([[makeQuery(id+"F4.imprint","IMPRINT",EDGE,{"derivedFrom":sQuery(id+"F4.wireOp",EDGE,"E22.0.2.9")}),-1.0]])]});
            var Q89;
            Q89=makeQuery(id+"F4.imprint","IMPRINT",FACE,{"disambiguationData":[TD([[makeQuery(id+"F4.imprint","IMPRINT",EDGE,{"derivedFrom":sQuery(id+"F4.wireOp",EDGE,"E22.0.3.9")}),-1.0]])]});
            var Q90;
            Q90=makeQuery(id+"F4.imprint","IMPRINT",FACE,{"disambiguationData":[TD([[makeQuery(id+"F4.imprint","IMPRINT",EDGE,{"derivedFrom":sQuery(id+"F4.wireOp",EDGE,"E22.0.4.9")}),-1.0]])]});
            var Q91;
            Q91=makeQuery(id+"F4.imprint","IMPRINT",FACE,{"disambiguationData":[TD([[makeQuery(id+"F4.imprint","IMPRINT",EDGE,{"derivedFrom":sQuery(id+"F4.wireOp",EDGE,"E22.18.0.10")}),-1.0]])]});
            var Q92;
            Q92=makeQuery(id+"F4.imprint","IMPRINT",FACE,{"disambiguationData":[TD([[makeQuery(id+"F4.imprint","IMPRINT",EDGE,{"derivedFrom":sQuery(id+"F4.wireOp",EDGE,"E22.18.1.10")}),-1.0]])]});
            var Q93;
            Q93=makeQuery(id+"F4.imprint","IMPRINT",FACE,{"disambiguationData":[TD([[makeQuery(id+"F4.imprint","IMPRINT",EDGE,{"derivedFrom":sQuery(id+"F4.wireOp",EDGE,"E22.18.2.10")}),-1.0]])]});
            var Q94;
            Q94=makeQuery(id+"F4.imprint","IMPRINT",FACE,{"disambiguationData":[TD([[makeQuery(id+"F4.imprint","IMPRINT",EDGE,{"derivedFrom":sQuery(id+"F4.wireOp",EDGE,"E22.18.3.10")}),-1.0]])]});
            var Q95;
            {var subQ1=sQuery(id+"F4.wireOp",EDGE,"E22.18.4.10");Q95=makeQuery(id+"F4.imprint","IMPRINT",FACE,{"disambiguationData":[TD([[makeQuery(id+"F4.imprint","IMPRINT",EDGE,{"derivedFrom":subQ1}),-1.0]])]});}
            var Q96;
            {var subQ0=sQuery(id+"F4.wireOp",EDGE,"E22.12.0.10");Q96=makeQuery(id+"F4.imprint","IMPRINT",FACE,{"disambiguationData":[TD([[makeQuery(id+"F4.imprint","IMPRINT",EDGE,{"derivedFrom":subQ0}),-1.0]])]});}
            var Q97;
            Q97=makeQuery(id+"F4.imprint","IMPRINT",FACE,{"disambiguationData":[TD([[makeQuery(id+"F4.imprint","IMPRINT",EDGE,{"derivedFrom":sQuery(id+"F4.wireOp",EDGE,"E22.0.1.10")}),-1.0]])]});
            var Q98;
            Q98=makeQuery(id+"F4.imprint","IMPRINT",FACE,{"disambiguationData":[TD([[makeQuery(id+"F4.imprint","IMPRINT",EDGE,{"derivedFrom":sQuery(id+"F4.wireOp",EDGE,"E22.0.2.10")}),-1.0]])]});
            var Q99;
            Q99=makeQuery(id+"F4.imprint","IMPRINT",FACE,{"disambiguationData":[TD([[makeQuery(id+"F4.imprint","IMPRINT",EDGE,{"derivedFrom":sQuery(id+"F4.wireOp",EDGE,"E22.0.3.10")}),-1.0]])]});
            var Q100;
            Q100=makeQuery(id+"F4.imprint","IMPRINT",FACE,{"disambiguationData":[TD([[makeQuery(id+"F4.imprint","IMPRINT",EDGE,{"derivedFrom":sQuery(id+"F4.wireOp",EDGE,"E22.0.4.10")}),-1.0]])]});
            var Q101;
            Q101=makeQuery(id+"F4.imprint","IMPRINT",FACE,{"disambiguationData":[TD([[makeQuery(id+"F4.imprint","IMPRINT",EDGE,{"derivedFrom":sQuery(id+"F4.wireOp",EDGE,"E22.18.0.11")}),-1.0]])]});
            var Q102;
            Q102=makeQuery(id+"F4.imprint","IMPRINT",FACE,{"disambiguationData":[TD([[makeQuery(id+"F4.imprint","IMPRINT",EDGE,{"derivedFrom":sQuery(id+"F4.wireOp",EDGE,"E22.18.1.11")}),-1.0]])]});
            var Q103;
            Q103=makeQuery(id+"F4.imprint","IMPRINT",FACE,{"disambiguationData":[TD([[makeQuery(id+"F4.imprint","IMPRINT",EDGE,{"derivedFrom":sQuery(id+"F4.wireOp",EDGE,"E22.18.2.11")}),-1.0]])]});
            var Q104;
            Q104=makeQuery(id+"F4.imprint","IMPRINT",FACE,{"disambiguationData":[TD([[makeQuery(id+"F4.imprint","IMPRINT",EDGE,{"derivedFrom":sQuery(id+"F4.wireOp",EDGE,"E22.18.3.11")}),-1.0]])]});
            var Q105;
            {var subQ1=sQuery(id+"F4.wireOp",EDGE,"E22.18.4.11");Q105=makeQuery(id+"F4.imprint","IMPRINT",FACE,{"disambiguationData":[TD([[makeQuery(id+"F4.imprint","IMPRINT",EDGE,{"derivedFrom":subQ1}),-1.0]])]});}
            var Q106;
            {var subQ0=sQuery(id+"F4.wireOp",EDGE,"E22.12.0.11");Q106=makeQuery(id+"F4.imprint","IMPRINT",FACE,{"disambiguationData":[TD([[makeQuery(id+"F4.imprint","IMPRINT",EDGE,{"derivedFrom":subQ0}),-1.0]])]});}
            var Q107;
            Q107=makeQuery(id+"F4.imprint","IMPRINT",FACE,{"disambiguationData":[TD([[makeQuery(id+"F4.imprint","IMPRINT",EDGE,{"derivedFrom":sQuery(id+"F4.wireOp",EDGE,"E22.0.1.11")}),-1.0]])]});
            var Q108;
            Q108=makeQuery(id+"F4.imprint","IMPRINT",FACE,{"disambiguationData":[TD([[makeQuery(id+"F4.imprint","IMPRINT",EDGE,{"derivedFrom":sQuery(id+"F4.wireOp",EDGE,"E22.0.2.11")}),-1.0]])]});
            var Q109;
            Q109=makeQuery(id+"F4.imprint","IMPRINT",FACE,{"disambiguationData":[TD([[makeQuery(id+"F4.imprint","IMPRINT",EDGE,{"derivedFrom":sQuery(id+"F4.wireOp",EDGE,"E22.0.3.11")}),-1.0]])]});
            var Q110;
            Q110=makeQuery(id+"F4.imprint","IMPRINT",FACE,{"disambiguationData":[TD([[makeQuery(id+"F4.imprint","IMPRINT",EDGE,{"derivedFrom":sQuery(id+"F4.wireOp",EDGE,"E22.0.4.11")}),-1.0]])]});
            var Q111;
            Q111=makeQuery(id+"F4.imprint","IMPRINT",FACE,{"disambiguationData":[TD([[makeQuery(id+"F4.imprint","IMPRINT",EDGE,{"derivedFrom":sQuery(id+"F4.wireOp",EDGE,"E22.18.0.12")}),-1.0]])]});
            var Q112;
            Q112=makeQuery(id+"F4.imprint","IMPRINT",FACE,{"disambiguationData":[TD([[makeQuery(id+"F4.imprint","IMPRINT",EDGE,{"derivedFrom":sQuery(id+"F4.wireOp",EDGE,"E22.18.1.12")}),-1.0]])]});
            var Q113;
            Q113=makeQuery(id+"F4.imprint","IMPRINT",FACE,{"disambiguationData":[TD([[makeQuery(id+"F4.imprint","IMPRINT",EDGE,{"derivedFrom":sQuery(id+"F4.wireOp",EDGE,"E22.18.2.12")}),-1.0]])]});
            var Q114;
            Q114=makeQuery(id+"F4.imprint","IMPRINT",FACE,{"disambiguationData":[TD([[makeQuery(id+"F4.imprint","IMPRINT",EDGE,{"derivedFrom":sQuery(id+"F4.wireOp",EDGE,"E22.18.3.12")}),-1.0]])]});
            var Q115;
            {var subQ1=sQuery(id+"F4.wireOp",EDGE,"E22.18.4.12");Q115=makeQuery(id+"F4.imprint","IMPRINT",FACE,{"disambiguationData":[TD([[makeQuery(id+"F4.imprint","IMPRINT",EDGE,{"derivedFrom":subQ1}),-1.0]])]});}
            var Q116;
            {var subQ0=sQuery(id+"F4.wireOp",EDGE,"E22.12.0.12");Q116=makeQuery(id+"F4.imprint","IMPRINT",FACE,{"disambiguationData":[TD([[makeQuery(id+"F4.imprint","IMPRINT",EDGE,{"derivedFrom":subQ0}),-1.0]])]});}
            var Q117;
            Q117=makeQuery(id+"F4.imprint","IMPRINT",FACE,{"disambiguationData":[TD([[makeQuery(id+"F4.imprint","IMPRINT",EDGE,{"derivedFrom":sQuery(id+"F4.wireOp",EDGE,"E22.0.1.12")}),-1.0]])]});
            var Q118;
            Q118=makeQuery(id+"F4.imprint","IMPRINT",FACE,{"disambiguationData":[TD([[makeQuery(id+"F4.imprint","IMPRINT",EDGE,{"derivedFrom":sQuery(id+"F4.wireOp",EDGE,"E22.0.2.12")}),-1.0]])]});
            var Q119;
            Q119=makeQuery(id+"F4.imprint","IMPRINT",FACE,{"disambiguationData":[TD([[makeQuery(id+"F4.imprint","IMPRINT",EDGE,{"derivedFrom":sQuery(id+"F4.wireOp",EDGE,"E22.0.3.12")}),-1.0]])]});
            var Q120;
            Q120=makeQuery(id+"F4.imprint","IMPRINT",FACE,{"disambiguationData":[TD([[makeQuery(id+"F4.imprint","IMPRINT",EDGE,{"derivedFrom":sQuery(id+"F4.wireOp",EDGE,"E22.0.4.12")}),-1.0]])]});
            var Q121;
            Q121=makeQuery(id+"F4.imprint","IMPRINT",FACE,{"disambiguationData":[TD([[makeQuery(id+"F4.imprint","IMPRINT",EDGE,{"derivedFrom":sQuery(id+"F4.wireOp",EDGE,"E22.18.0.13")}),-1.0]])]});
            var Q122;
            Q122=makeQuery(id+"F4.imprint","IMPRINT",FACE,{"disambiguationData":[TD([[makeQuery(id+"F4.imprint","IMPRINT",EDGE,{"derivedFrom":sQuery(id+"F4.wireOp",EDGE,"E22.18.1.13")}),-1.0]])]});
            var Q123;
            Q123=makeQuery(id+"F4.imprint","IMPRINT",FACE,{"disambiguationData":[TD([[makeQuery(id+"F4.imprint","IMPRINT",EDGE,{"derivedFrom":sQuery(id+"F4.wireOp",EDGE,"E22.18.2.13")}),-1.0]])]});
            var Q124;
            Q124=makeQuery(id+"F4.imprint","IMPRINT",FACE,{"disambiguationData":[TD([[makeQuery(id+"F4.imprint","IMPRINT",EDGE,{"derivedFrom":sQuery(id+"F4.wireOp",EDGE,"E22.18.3.13")}),-1.0]])]});
            var Q125;
            {var subQ0=sQuery(id+"F4.wireOp",EDGE,"E22.24.4.13");var subQ1=sQuery(id+"F4.wireOp",EDGE,"E22.18.4.13");var subQ2=makeQuery(id+"F4.imprint","INTERSECT",VERTEX,{"derivedFrom":[subQ1,subQ0]});Q125=makeQuery(id+"F4.imprint","IMPRINT",FACE,{"disambiguationData":[TD([[makeQuery(id+"F4.imprint","IMPRINT",EDGE,{"disambiguationData":[TD([[subQ2,1.0]])],"derivedFrom":subQ1}),-1.0]])]});}
            var Q126;
            {var subQ0=sQuery(id+"F4.wireOp",EDGE,"E22.15.0.13");Q126=makeQuery(id+"F4.imprint","IMPRINT",FACE,{"disambiguationData":[TD([[makeQuery(id+"F4.imprint","IMPRINT",EDGE,{"derivedFrom":subQ0}),-1.0]])]});}
            var Q127;
            {var subQ5=sQuery(id+"F4.wireOp",EDGE,"E22.24.0.14");Q127=makeQuery(id+"F4.imprint","IMPRINT",FACE,{"disambiguationData":[TD([[makeQuery(id+"F4.imprint","IMPRINT",EDGE,{"derivedFrom":subQ5}),-1.0]])]});}
            var Q128;
            {var subQ5=sQuery(id+"F4.wireOp",EDGE,"E22.24.1.14");Q128=makeQuery(id+"F4.imprint","IMPRINT",FACE,{"disambiguationData":[TD([[makeQuery(id+"F4.imprint","IMPRINT",EDGE,{"derivedFrom":subQ5}),-1.0]])]});}
            var Q129;
            Q129=makeQuery(id+"F4.imprint","IMPRINT",FACE,{"disambiguationData":[TD([[makeQuery(id+"F4.imprint","IMPRINT",EDGE,{"derivedFrom":sQuery(id+"F4.wireOp",EDGE,"E22.0.2.13")}),-1.0]])]});
            var Q130;
            {var subQ5=sQuery(id+"F4.wireOp",EDGE,"E22.24.2.14");Q130=makeQuery(id+"F4.imprint","IMPRINT",FACE,{"disambiguationData":[TD([[makeQuery(id+"F4.imprint","IMPRINT",EDGE,{"derivedFrom":subQ5}),-1.0]])]});}
            var Q131;
            Q131=makeQuery(id+"F4.imprint","IMPRINT",FACE,{"disambiguationData":[TD([[makeQuery(id+"F4.imprint","IMPRINT",EDGE,{"derivedFrom":sQuery(id+"F4.wireOp",EDGE,"E22.0.3.13")}),-1.0]])]});
            var Q132;
            {var subQ1=sQuery(id+"F4.wireOp",EDGE,"E22.24.3.14");Q132=makeQuery(id+"F4.imprint","IMPRINT",FACE,{"disambiguationData":[TD([[makeQuery(id+"F4.imprint","IMPRINT",EDGE,{"derivedFrom":subQ1}),-1.0]])]});}
            var Q133;
            {var subQ0=sQuery(id+"F4.wireOp",EDGE,"E22.3.4.13");Q133=makeQuery(id+"F4.imprint","IMPRINT",FACE,{"disambiguationData":[TD([[makeQuery(id+"F4.imprint","IMPRINT",EDGE,{"derivedFrom":subQ0}),-1.0]])]});}
            var Q134;
            Q134=makeQuery(id+"F4.imprint","IMPRINT",FACE,{"disambiguationData":[TD([[makeQuery(id+"F4.imprint","IMPRINT",EDGE,{"derivedFrom":sQuery(id+"F4.wireOp",EDGE,"E22.0.1.13")}),-1.0]])]});
            var Q135;
            {var subQ4=sQuery(id+"F4.wireOp",EDGE,"E21.6.4.1");Q135=makeQuery(id+"F4.imprint","IMPRINT",FACE,{"disambiguationData":[TD([[makeQuery(id+"F4.imprint","IMPRINT",EDGE,{"derivedFrom":subQ4}),-1.0]])]});}
            var Q136;
            {var subQ0=sQuery(id+"F4.wireOp",EDGE,"E22.21.4.2");Q136=makeQuery(id+"F4.imprint","IMPRINT",FACE,{"disambiguationData":[TD([[makeQuery(id+"F4.imprint","IMPRINT",EDGE,{"derivedFrom":subQ0}),-1.0]])]});}
            var Q137;
            Q137=makeQuery(id+"F1.opExtrude","CAP_FACE",FACE,{"disambiguationData":[OSD([sQuery(id+"F0.wireOp",EDGE,"E0.bottom"),sQuery(id+"F0.wireOp",EDGE,"E0.top"),sQuery(id+"F0.wireOp",EDGE,"E0.left"),sQuery(id+"F0.wireOp",EDGE,"E0.right")])],"isStart":true});
            extrude(context, id + "F5", {"entities" : qUnion([Q0, Q1, Q2, Q3, Q4, Q5, Q6, Q7, Q8, Q9, Q10, Q11, Q12, Q13, Q14, Q15, Q16, Q17, Q18, Q19, Q20, Q21, Q22, Q23, Q24, Q25, Q26, Q27, Q28, Q29, Q30, Q31, Q32, Q33, Q34, Q35, Q36, Q37, Q38, Q39, Q40, Q41, Q42, Q43, Q44, Q45, Q46, Q47, Q48, Q49, Q50, Q51, Q52, Q53, Q54, Q55, Q56, Q57, Q58, Q59, Q60, Q61, Q62, Q63, Q64, Q65, Q66, Q67, Q68, Q69, Q70, Q71, Q72, Q73, Q74, Q75, Q76, Q77, Q78, Q79, Q80, Q81, Q82, Q83, Q84, Q85, Q86, Q87, Q88, Q89, Q90, Q91, Q92, Q93, Q94, Q95, Q96, Q97, Q98, Q99, Q100, Q101, Q102, Q103, Q104, Q105, Q106, Q107, Q108, Q109, Q110, Q111, Q112, Q113, Q114, Q115, Q116, Q117, Q118, Q119, Q120, Q121, Q122, Q123, Q124, Q125, Q126, Q127, Q128, Q129, Q130, Q131, Q132, Q133, Q134, Q135, Q136]), "operationType" : NewBodyOperationType.REMOVE, "endBound" : BoundingType.UP_TO_SURFACE, "oppositeDirection" : true, "depth" : 25 * mm, "endBoundEntityFace" : qUnion([Q137]), "offsetDistance" : 25 * mm});
        }
        {
            var Q0;
            Q0=makeQuery(id+"F3.opSweep","SWEPT_FACE",FACE,{"disambiguationData":[OSD([sQuery(id+"F0.wireOp",EDGE,"E0.bottom"),sQuery(id+"F2.wireOp",EDGE,"E7.left")])]});
            var sketch = newSketch(context, id + "F6", { "sketchPlane" : qUnion([Q0])});
            skLineSegment(sketch, "E25.0", {"start": v(-90, 17.8) * mm, "end": v(51, 17.8) * mm});
            skLineSegment(sketch, "E26.0", {"start": v(-87.5, 20.3) * mm, "end": v(-87.5, 0.3) * mm});
            skLineSegment(sketch, "E27.0", {"start": v(-90, 2.8) * mm, "end": v(51, 2.8) * mm});
            skLineSegment(sketch, "E28.0", {"start": v(48.5, 20.3) * mm, "end": v(48.5, 0.3) * mm});
            skCircle(sketch, "E29.cCircle", {"center": v(-82.75, 21.24) * mm, "radius": 2.5 * mm, "construction": true});
            skLineSegment(sketch, "E29.0", {"start": v(-81.3, 18.74) * mm, "end": v(-84.2, 18.74) * mm});
            skLineSegment(sketch, "E29.1", {"start": v(-84.2, 18.74) * mm, "end": v(-85.64, 21.24) * mm});
            skLineSegment(sketch, "E29.2", {"start": v(-85.64, 21.24) * mm, "end": v(-84.2, 23.74) * mm});
            skLineSegment(sketch, "E29.3", {"start": v(-84.2, 23.74) * mm, "end": v(-81.3, 23.74) * mm});
            skLineSegment(sketch, "E29.4", {"start": v(-81.3, 23.74) * mm, "end": v(-79.86, 21.24) * mm});
            skLineSegment(sketch, "E29.5", {"start": v(-79.86, 21.24) * mm, "end": v(-81.3, 18.74) * mm});
            skPoint(sketch, "E29.0.midPoint", {"position": v(-82.75, 18.74) * mm});
            skCircle(sketch, "E30.cCircle", {"center": v(-88.16, 18.11) * mm, "radius": 2.5 * mm, "construction": true});
            skLineSegment(sketch, "E30.0", {"start": v(-86.72, 15.61) * mm, "end": v(-89.6, 15.61) * mm});
            skLineSegment(sketch, "E30.1", {"start": v(-89.6, 15.61) * mm, "end": v(-91.05, 18.11) * mm});
            skLineSegment(sketch, "E30.2", {"start": v(-91.05, 18.11) * mm, "end": v(-89.6, 20.61) * mm});
            skLineSegment(sketch, "E30.3", {"start": v(-89.6, 20.61) * mm, "end": v(-86.72, 20.61) * mm});
            skLineSegment(sketch, "E30.4", {"start": v(-86.72, 20.61) * mm, "end": v(-85.28, 18.11) * mm});
            skLineSegment(sketch, "E30.5", {"start": v(-85.28, 18.11) * mm, "end": v(-86.72, 15.61) * mm});
            skPoint(sketch, "E30.0.midPoint", {"position": v(-88.16, 15.61) * mm});
            skLineSegment(sketch, "E31.0.1.0", {"start": v(-89.6, 14.36) * mm, "end": v(-86.72, 14.36) * mm});
            skLineSegment(sketch, "E31.0.1.1", {"start": v(-91.05, 11.86) * mm, "end": v(-89.6, 14.36) * mm});
            skLineSegment(sketch, "E31.0.1.2", {"start": v(-89.6, 9.36) * mm, "end": v(-91.05, 11.86) * mm});
            skLineSegment(sketch, "E31.0.1.3", {"start": v(-86.72, 9.36) * mm, "end": v(-89.6, 9.36) * mm});
            skLineSegment(sketch, "E31.0.1.4", {"start": v(-85.28, 11.86) * mm, "end": v(-86.72, 9.36) * mm});
            skLineSegment(sketch, "E31.0.1.5", {"start": v(-86.72, 14.36) * mm, "end": v(-85.28, 11.86) * mm});
            skLineSegment(sketch, "E31.0.1.6", {"start": v(-84.2, 12.49) * mm, "end": v(-85.64, 14.99) * mm});
            skLineSegment(sketch, "E31.0.1.7", {"start": v(-85.64, 14.99) * mm, "end": v(-84.2, 17.49) * mm});
            skLineSegment(sketch, "E31.0.1.8", {"start": v(-84.2, 17.49) * mm, "end": v(-81.3, 17.49) * mm});
            skLineSegment(sketch, "E31.0.1.9", {"start": v(-81.3, 17.49) * mm, "end": v(-79.86, 14.99) * mm});
            skLineSegment(sketch, "E31.0.1.10", {"start": v(-79.86, 14.99) * mm, "end": v(-81.3, 12.49) * mm});
            skLineSegment(sketch, "E31.0.1.11", {"start": v(-81.3, 12.49) * mm, "end": v(-84.2, 12.49) * mm});
            skLineSegment(sketch, "E31.1.0.0", {"start": v(-78.61, 20.61) * mm, "end": v(-75.73, 20.61) * mm});
            skLineSegment(sketch, "E31.1.0.1", {"start": v(-80.06, 18.11) * mm, "end": v(-78.61, 20.61) * mm});
            skLineSegment(sketch, "E31.1.0.2", {"start": v(-78.61, 15.61) * mm, "end": v(-80.06, 18.11) * mm});
            skLineSegment(sketch, "E31.1.0.3", {"start": v(-75.73, 15.61) * mm, "end": v(-78.61, 15.61) * mm});
            skLineSegment(sketch, "E31.1.0.4", {"start": v(-74.28, 18.11) * mm, "end": v(-75.73, 15.61) * mm});
            skLineSegment(sketch, "E31.1.0.5", {"start": v(-75.73, 20.61) * mm, "end": v(-74.28, 18.11) * mm});
            skLineSegment(sketch, "E31.1.0.6", {"start": v(-73.2, 18.74) * mm, "end": v(-74.65, 21.24) * mm});
            skLineSegment(sketch, "E31.1.0.7", {"start": v(-74.65, 21.24) * mm, "end": v(-73.2, 23.74) * mm});
            skLineSegment(sketch, "E31.1.0.8", {"start": v(-73.2, 23.74) * mm, "end": v(-70.32, 23.74) * mm});
            skLineSegment(sketch, "E31.1.0.9", {"start": v(-70.32, 23.74) * mm, "end": v(-68.87, 21.24) * mm});
            skLineSegment(sketch, "E31.1.0.10", {"start": v(-68.87, 21.24) * mm, "end": v(-70.32, 18.74) * mm});
            skLineSegment(sketch, "E31.1.0.11", {"start": v(-70.32, 18.74) * mm, "end": v(-73.2, 18.74) * mm});
            skLineSegment(sketch, "E31.1.1.0", {"start": v(-78.61, 14.36) * mm, "end": v(-75.73, 14.36) * mm});
            skLineSegment(sketch, "E31.1.1.1", {"start": v(-80.06, 11.86) * mm, "end": v(-78.61, 14.36) * mm});
            skLineSegment(sketch, "E31.1.1.2", {"start": v(-78.61, 9.36) * mm, "end": v(-80.06, 11.86) * mm});
            skLineSegment(sketch, "E31.1.1.3", {"start": v(-75.73, 9.36) * mm, "end": v(-78.61, 9.36) * mm});
            skLineSegment(sketch, "E31.1.1.4", {"start": v(-74.28, 11.86) * mm, "end": v(-75.73, 9.36) * mm});
            skLineSegment(sketch, "E31.1.1.5", {"start": v(-75.73, 14.36) * mm, "end": v(-74.28, 11.86) * mm});
            skLineSegment(sketch, "E31.1.1.6", {"start": v(-73.2, 12.49) * mm, "end": v(-74.65, 14.99) * mm});
            skLineSegment(sketch, "E31.1.1.7", {"start": v(-74.65, 14.99) * mm, "end": v(-73.2, 17.49) * mm});
            skLineSegment(sketch, "E31.1.1.8", {"start": v(-73.2, 17.49) * mm, "end": v(-70.32, 17.49) * mm});
            skLineSegment(sketch, "E31.1.1.9", {"start": v(-70.32, 17.49) * mm, "end": v(-68.87, 14.99) * mm});
            skLineSegment(sketch, "E31.1.1.10", {"start": v(-68.87, 14.99) * mm, "end": v(-70.32, 12.49) * mm});
            skLineSegment(sketch, "E31.1.1.11", {"start": v(-70.32, 12.49) * mm, "end": v(-73.2, 12.49) * mm});
            skLineSegment(sketch, "E31.2.0.0", {"start": v(-67.62, 20.61) * mm, "end": v(-64.73, 20.61) * mm});
            skLineSegment(sketch, "E31.2.0.1", {"start": v(-69.07, 18.11) * mm, "end": v(-67.62, 20.61) * mm});
            skLineSegment(sketch, "E31.2.0.2", {"start": v(-67.62, 15.61) * mm, "end": v(-69.07, 18.11) * mm});
            skLineSegment(sketch, "E31.2.0.3", {"start": v(-64.73, 15.61) * mm, "end": v(-67.62, 15.61) * mm});
            skLineSegment(sketch, "E31.2.0.4", {"start": v(-63.3, 18.11) * mm, "end": v(-64.73, 15.61) * mm});
            skLineSegment(sketch, "E31.2.0.5", {"start": v(-64.73, 20.61) * mm, "end": v(-63.3, 18.11) * mm});
            skLineSegment(sketch, "E31.2.0.6", {"start": v(-62.2, 18.74) * mm, "end": v(-63.65, 21.24) * mm});
            skLineSegment(sketch, "E31.2.0.7", {"start": v(-63.65, 21.24) * mm, "end": v(-62.2, 23.74) * mm});
            skLineSegment(sketch, "E31.2.0.8", {"start": v(-62.2, 23.74) * mm, "end": v(-59.32, 23.74) * mm});
            skLineSegment(sketch, "E31.2.0.9", {"start": v(-59.32, 23.74) * mm, "end": v(-57.88, 21.24) * mm});
            skLineSegment(sketch, "E31.2.0.10", {"start": v(-57.88, 21.24) * mm, "end": v(-59.32, 18.74) * mm});
            skLineSegment(sketch, "E31.2.0.11", {"start": v(-59.32, 18.74) * mm, "end": v(-62.2, 18.74) * mm});
            skLineSegment(sketch, "E31.2.1.0", {"start": v(-67.62, 14.36) * mm, "end": v(-64.73, 14.36) * mm});
            skLineSegment(sketch, "E31.2.1.1", {"start": v(-69.07, 11.86) * mm, "end": v(-67.62, 14.36) * mm});
            skLineSegment(sketch, "E31.2.1.2", {"start": v(-67.62, 9.36) * mm, "end": v(-69.07, 11.86) * mm});
            skLineSegment(sketch, "E31.2.1.3", {"start": v(-64.73, 9.36) * mm, "end": v(-67.62, 9.36) * mm});
            skLineSegment(sketch, "E31.2.1.4", {"start": v(-63.3, 11.86) * mm, "end": v(-64.73, 9.36) * mm});
            skLineSegment(sketch, "E31.2.1.5", {"start": v(-64.73, 14.36) * mm, "end": v(-63.3, 11.86) * mm});
            skLineSegment(sketch, "E31.2.1.6", {"start": v(-62.2, 12.49) * mm, "end": v(-63.65, 14.99) * mm});
            skLineSegment(sketch, "E31.2.1.7", {"start": v(-63.65, 14.99) * mm, "end": v(-62.2, 17.49) * mm});
            skLineSegment(sketch, "E31.2.1.8", {"start": v(-62.2, 17.49) * mm, "end": v(-59.32, 17.49) * mm});
            skLineSegment(sketch, "E31.2.1.9", {"start": v(-59.32, 17.49) * mm, "end": v(-57.88, 14.99) * mm});
            skLineSegment(sketch, "E31.2.1.10", {"start": v(-57.88, 14.99) * mm, "end": v(-59.32, 12.49) * mm});
            skLineSegment(sketch, "E31.2.1.11", {"start": v(-59.32, 12.49) * mm, "end": v(-62.2, 12.49) * mm});
            skLineSegment(sketch, "E31.direction1", {"start": v(-89.6, 20.61) * mm, "end": v(-78.61, 20.61) * mm, "construction": true});
            skLineSegment(sketch, "E31.direction2", {"start": v(-89.6, 20.61) * mm, "end": v(-89.6, 14.36) * mm, "construction": true});
            skLineSegment(sketch, "E32.0.0.2", {"start": v(-89.6, 8.11) * mm, "end": v(-86.72, 8.11) * mm});
            skLineSegment(sketch, "E32.3.0.2", {"start": v(-91.05, 5.61) * mm, "end": v(-89.6, 8.11) * mm});
            skLineSegment(sketch, "E32.6.0.2", {"start": v(-89.6, 3.11) * mm, "end": v(-91.05, 5.61) * mm});
            skLineSegment(sketch, "E32.9.0.2", {"start": v(-86.72, 3.11) * mm, "end": v(-89.6, 3.11) * mm});
            skLineSegment(sketch, "E32.12.0.2", {"start": v(-85.28, 5.61) * mm, "end": v(-86.72, 3.11) * mm});
            skLineSegment(sketch, "E32.15.0.2", {"start": v(-86.72, 8.11) * mm, "end": v(-85.28, 5.61) * mm});
            skLineSegment(sketch, "E32.18.0.2", {"start": v(-84.2, 6.24) * mm, "end": v(-85.64, 8.74) * mm});
            skLineSegment(sketch, "E32.21.0.2", {"start": v(-85.64, 8.74) * mm, "end": v(-84.2, 11.24) * mm});
            skLineSegment(sketch, "E32.24.0.2", {"start": v(-84.2, 11.24) * mm, "end": v(-81.3, 11.24) * mm});
            skLineSegment(sketch, "E32.27.0.2", {"start": v(-81.3, 11.24) * mm, "end": v(-79.86, 8.74) * mm});
            skLineSegment(sketch, "E32.30.0.2", {"start": v(-79.86, 8.74) * mm, "end": v(-81.3, 6.24) * mm});
            skLineSegment(sketch, "E32.33.0.2", {"start": v(-81.3, 6.24) * mm, "end": v(-84.2, 6.24) * mm});
            skLineSegment(sketch, "E32.0.1.2", {"start": v(-78.61, 8.11) * mm, "end": v(-75.73, 8.11) * mm});
            skLineSegment(sketch, "E32.3.1.2", {"start": v(-80.06, 5.61) * mm, "end": v(-78.61, 8.11) * mm});
            skLineSegment(sketch, "E32.6.1.2", {"start": v(-78.61, 3.11) * mm, "end": v(-80.06, 5.61) * mm});
            skLineSegment(sketch, "E32.9.1.2", {"start": v(-75.73, 3.11) * mm, "end": v(-78.61, 3.11) * mm});
            skLineSegment(sketch, "E32.12.1.2", {"start": v(-74.28, 5.61) * mm, "end": v(-75.73, 3.11) * mm});
            skLineSegment(sketch, "E32.15.1.2", {"start": v(-75.73, 8.11) * mm, "end": v(-74.28, 5.61) * mm});
            skLineSegment(sketch, "E32.18.1.2", {"start": v(-73.2, 6.24) * mm, "end": v(-74.65, 8.74) * mm});
            skLineSegment(sketch, "E32.21.1.2", {"start": v(-74.65, 8.74) * mm, "end": v(-73.2, 11.24) * mm});
            skLineSegment(sketch, "E32.24.1.2", {"start": v(-73.2, 11.24) * mm, "end": v(-70.32, 11.24) * mm});
            skLineSegment(sketch, "E32.27.1.2", {"start": v(-70.32, 11.24) * mm, "end": v(-68.87, 8.74) * mm});
            skLineSegment(sketch, "E32.30.1.2", {"start": v(-68.87, 8.74) * mm, "end": v(-70.32, 6.24) * mm});
            skLineSegment(sketch, "E32.33.1.2", {"start": v(-70.32, 6.24) * mm, "end": v(-73.2, 6.24) * mm});
            skLineSegment(sketch, "E32.0.2.2", {"start": v(-67.62, 8.11) * mm, "end": v(-64.73, 8.11) * mm});
            skLineSegment(sketch, "E32.3.2.2", {"start": v(-69.07, 5.61) * mm, "end": v(-67.62, 8.11) * mm});
            skLineSegment(sketch, "E32.6.2.2", {"start": v(-67.62, 3.11) * mm, "end": v(-69.07, 5.61) * mm});
            skLineSegment(sketch, "E32.9.2.2", {"start": v(-64.73, 3.11) * mm, "end": v(-67.62, 3.11) * mm});
            skLineSegment(sketch, "E32.12.2.2", {"start": v(-63.3, 5.61) * mm, "end": v(-64.73, 3.11) * mm});
            skLineSegment(sketch, "E32.15.2.2", {"start": v(-64.73, 8.11) * mm, "end": v(-63.3, 5.61) * mm});
            skLineSegment(sketch, "E32.18.2.2", {"start": v(-62.2, 6.24) * mm, "end": v(-63.65, 8.74) * mm});
            skLineSegment(sketch, "E32.21.2.2", {"start": v(-63.65, 8.74) * mm, "end": v(-62.2, 11.24) * mm});
            skLineSegment(sketch, "E32.24.2.2", {"start": v(-62.2, 11.24) * mm, "end": v(-59.32, 11.24) * mm});
            skLineSegment(sketch, "E32.27.2.2", {"start": v(-59.32, 11.24) * mm, "end": v(-57.88, 8.74) * mm});
            skLineSegment(sketch, "E32.30.2.2", {"start": v(-57.88, 8.74) * mm, "end": v(-59.32, 6.24) * mm});
            skLineSegment(sketch, "E32.33.2.2", {"start": v(-59.32, 6.24) * mm, "end": v(-62.2, 6.24) * mm});
            skLineSegment(sketch, "E33.0.0.3", {"start": v(-89.6, 1.86) * mm, "end": v(-86.72, 1.86) * mm});
            skLineSegment(sketch, "E33.3.0.3", {"start": v(-91.05, -0.64) * mm, "end": v(-89.6, 1.86) * mm});
            skLineSegment(sketch, "E33.6.0.3", {"start": v(-89.6, -3.14) * mm, "end": v(-91.05, -0.64) * mm});
            skLineSegment(sketch, "E33.9.0.3", {"start": v(-86.72, -3.14) * mm, "end": v(-89.6, -3.14) * mm});
            skLineSegment(sketch, "E33.12.0.3", {"start": v(-85.28, -0.64) * mm, "end": v(-86.72, -3.14) * mm});
            skLineSegment(sketch, "E33.15.0.3", {"start": v(-86.72, 1.86) * mm, "end": v(-85.28, -0.64) * mm});
            skLineSegment(sketch, "E33.18.0.3", {"start": v(-84.2, -0.01) * mm, "end": v(-85.64, 2.49) * mm});
            skLineSegment(sketch, "E33.21.0.3", {"start": v(-85.64, 2.49) * mm, "end": v(-84.2, 4.99) * mm});
            skLineSegment(sketch, "E33.24.0.3", {"start": v(-84.2, 4.99) * mm, "end": v(-81.3, 4.99) * mm});
            skLineSegment(sketch, "E33.27.0.3", {"start": v(-81.3, 4.99) * mm, "end": v(-79.86, 2.49) * mm});
            skLineSegment(sketch, "E33.30.0.3", {"start": v(-79.86, 2.49) * mm, "end": v(-81.3, -0.01) * mm});
            skLineSegment(sketch, "E33.33.0.3", {"start": v(-81.3, -0.01) * mm, "end": v(-84.2, -0.01) * mm});
            skLineSegment(sketch, "E33.0.1.3", {"start": v(-78.61, 1.86) * mm, "end": v(-75.73, 1.86) * mm});
            skLineSegment(sketch, "E33.3.1.3", {"start": v(-80.06, -0.64) * mm, "end": v(-78.61, 1.86) * mm});
            skLineSegment(sketch, "E33.6.1.3", {"start": v(-78.61, -3.14) * mm, "end": v(-80.06, -0.64) * mm});
            skLineSegment(sketch, "E33.9.1.3", {"start": v(-75.73, -3.14) * mm, "end": v(-78.61, -3.14) * mm});
            skLineSegment(sketch, "E33.12.1.3", {"start": v(-74.28, -0.64) * mm, "end": v(-75.73, -3.14) * mm});
            skLineSegment(sketch, "E33.15.1.3", {"start": v(-75.73, 1.86) * mm, "end": v(-74.28, -0.64) * mm});
            skLineSegment(sketch, "E33.18.1.3", {"start": v(-73.2, -0.01) * mm, "end": v(-74.65, 2.49) * mm});
            skLineSegment(sketch, "E33.21.1.3", {"start": v(-74.65, 2.49) * mm, "end": v(-73.2, 4.99) * mm});
            skLineSegment(sketch, "E33.24.1.3", {"start": v(-73.2, 4.99) * mm, "end": v(-70.32, 4.99) * mm});
            skLineSegment(sketch, "E33.27.1.3", {"start": v(-70.32, 4.99) * mm, "end": v(-68.87, 2.49) * mm});
            skLineSegment(sketch, "E33.30.1.3", {"start": v(-68.87, 2.49) * mm, "end": v(-70.32, -0.01) * mm});
            skLineSegment(sketch, "E33.33.1.3", {"start": v(-70.32, -0.01) * mm, "end": v(-73.2, -0.01) * mm});
            skLineSegment(sketch, "E33.0.2.3", {"start": v(-67.62, 1.86) * mm, "end": v(-64.73, 1.86) * mm});
            skLineSegment(sketch, "E33.3.2.3", {"start": v(-69.07, -0.64) * mm, "end": v(-67.62, 1.86) * mm});
            skLineSegment(sketch, "E33.6.2.3", {"start": v(-67.62, -3.14) * mm, "end": v(-69.07, -0.64) * mm});
            skLineSegment(sketch, "E33.9.2.3", {"start": v(-64.73, -3.14) * mm, "end": v(-67.62, -3.14) * mm});
            skLineSegment(sketch, "E33.12.2.3", {"start": v(-63.3, -0.64) * mm, "end": v(-64.73, -3.14) * mm});
            skLineSegment(sketch, "E33.15.2.3", {"start": v(-64.73, 1.86) * mm, "end": v(-63.3, -0.64) * mm});
            skLineSegment(sketch, "E33.18.2.3", {"start": v(-62.2, -0.01) * mm, "end": v(-63.65, 2.49) * mm});
            skLineSegment(sketch, "E33.21.2.3", {"start": v(-63.65, 2.49) * mm, "end": v(-62.2, 4.99) * mm});
            skLineSegment(sketch, "E33.24.2.3", {"start": v(-62.2, 4.99) * mm, "end": v(-59.32, 4.99) * mm});
            skLineSegment(sketch, "E33.27.2.3", {"start": v(-59.32, 4.99) * mm, "end": v(-57.88, 2.49) * mm});
            skLineSegment(sketch, "E33.30.2.3", {"start": v(-57.88, 2.49) * mm, "end": v(-59.32, -0.01) * mm});
            skLineSegment(sketch, "E33.33.2.3", {"start": v(-59.32, -0.01) * mm, "end": v(-62.2, -0.01) * mm});
            skLineSegment(sketch, "E34.0.3.0", {"start": v(-56.63, 20.61) * mm, "end": v(-53.74, 20.61) * mm});
            skLineSegment(sketch, "E34.3.3.0", {"start": v(-58.07, 18.11) * mm, "end": v(-56.63, 20.61) * mm});
            skLineSegment(sketch, "E34.6.3.0", {"start": v(-56.63, 15.61) * mm, "end": v(-58.07, 18.11) * mm});
            skLineSegment(sketch, "E34.9.3.0", {"start": v(-53.74, 15.61) * mm, "end": v(-56.63, 15.61) * mm});
            skLineSegment(sketch, "E34.12.3.0", {"start": v(-52.3, 18.11) * mm, "end": v(-53.74, 15.61) * mm});
            skLineSegment(sketch, "E34.15.3.0", {"start": v(-53.74, 20.61) * mm, "end": v(-52.3, 18.11) * mm});
            skLineSegment(sketch, "E34.18.3.0", {"start": v(-51.22, 18.74) * mm, "end": v(-52.66, 21.24) * mm});
            skLineSegment(sketch, "E34.21.3.0", {"start": v(-52.66, 21.24) * mm, "end": v(-51.22, 23.74) * mm});
            skLineSegment(sketch, "E34.24.3.0", {"start": v(-51.22, 23.74) * mm, "end": v(-48.33, 23.74) * mm});
            skLineSegment(sketch, "E34.27.3.0", {"start": v(-48.33, 23.74) * mm, "end": v(-46.89, 21.24) * mm});
            skLineSegment(sketch, "E34.30.3.0", {"start": v(-46.89, 21.24) * mm, "end": v(-48.33, 18.74) * mm});
            skLineSegment(sketch, "E34.33.3.0", {"start": v(-48.33, 18.74) * mm, "end": v(-51.22, 18.74) * mm});
            skLineSegment(sketch, "E34.0.3.1", {"start": v(-56.63, 14.36) * mm, "end": v(-53.74, 14.36) * mm});
            skLineSegment(sketch, "E34.3.3.1", {"start": v(-58.07, 11.86) * mm, "end": v(-56.63, 14.36) * mm});
            skLineSegment(sketch, "E34.6.3.1", {"start": v(-56.63, 9.36) * mm, "end": v(-58.07, 11.86) * mm});
            skLineSegment(sketch, "E34.9.3.1", {"start": v(-53.74, 9.36) * mm, "end": v(-56.63, 9.36) * mm});
            skLineSegment(sketch, "E34.12.3.1", {"start": v(-52.3, 11.86) * mm, "end": v(-53.74, 9.36) * mm});
            skLineSegment(sketch, "E34.15.3.1", {"start": v(-53.74, 14.36) * mm, "end": v(-52.3, 11.86) * mm});
            skLineSegment(sketch, "E34.18.3.1", {"start": v(-51.22, 12.49) * mm, "end": v(-52.66, 14.99) * mm});
            skLineSegment(sketch, "E34.21.3.1", {"start": v(-52.66, 14.99) * mm, "end": v(-51.22, 17.49) * mm});
            skLineSegment(sketch, "E34.24.3.1", {"start": v(-51.22, 17.49) * mm, "end": v(-48.33, 17.49) * mm});
            skLineSegment(sketch, "E34.27.3.1", {"start": v(-48.33, 17.49) * mm, "end": v(-46.89, 14.99) * mm});
            skLineSegment(sketch, "E34.30.3.1", {"start": v(-46.89, 14.99) * mm, "end": v(-48.33, 12.49) * mm});
            skLineSegment(sketch, "E34.33.3.1", {"start": v(-48.33, 12.49) * mm, "end": v(-51.22, 12.49) * mm});
            skLineSegment(sketch, "E34.0.3.2", {"start": v(-56.63, 8.11) * mm, "end": v(-53.74, 8.11) * mm});
            skLineSegment(sketch, "E34.3.3.2", {"start": v(-58.07, 5.61) * mm, "end": v(-56.63, 8.11) * mm});
            skLineSegment(sketch, "E34.6.3.2", {"start": v(-56.63, 3.11) * mm, "end": v(-58.07, 5.61) * mm});
            skLineSegment(sketch, "E34.9.3.2", {"start": v(-53.74, 3.11) * mm, "end": v(-56.63, 3.11) * mm});
            skLineSegment(sketch, "E34.12.3.2", {"start": v(-52.3, 5.61) * mm, "end": v(-53.74, 3.11) * mm});
            skLineSegment(sketch, "E34.15.3.2", {"start": v(-53.74, 8.11) * mm, "end": v(-52.3, 5.61) * mm});
            skLineSegment(sketch, "E34.18.3.2", {"start": v(-51.22, 6.24) * mm, "end": v(-52.66, 8.74) * mm});
            skLineSegment(sketch, "E34.21.3.2", {"start": v(-52.66, 8.74) * mm, "end": v(-51.22, 11.24) * mm});
            skLineSegment(sketch, "E34.24.3.2", {"start": v(-51.22, 11.24) * mm, "end": v(-48.33, 11.24) * mm});
            skLineSegment(sketch, "E34.27.3.2", {"start": v(-48.33, 11.24) * mm, "end": v(-46.89, 8.74) * mm});
            skLineSegment(sketch, "E34.30.3.2", {"start": v(-46.89, 8.74) * mm, "end": v(-48.33, 6.24) * mm});
            skLineSegment(sketch, "E34.33.3.2", {"start": v(-48.33, 6.24) * mm, "end": v(-51.22, 6.24) * mm});
            skLineSegment(sketch, "E34.0.3.3", {"start": v(-56.63, 1.86) * mm, "end": v(-53.74, 1.86) * mm});
            skLineSegment(sketch, "E34.3.3.3", {"start": v(-58.07, -0.64) * mm, "end": v(-56.63, 1.86) * mm});
            skLineSegment(sketch, "E34.6.3.3", {"start": v(-56.63, -3.14) * mm, "end": v(-58.07, -0.64) * mm});
            skLineSegment(sketch, "E34.9.3.3", {"start": v(-53.74, -3.14) * mm, "end": v(-56.63, -3.14) * mm});
            skLineSegment(sketch, "E34.12.3.3", {"start": v(-52.3, -0.64) * mm, "end": v(-53.74, -3.14) * mm});
            skLineSegment(sketch, "E34.15.3.3", {"start": v(-53.74, 1.86) * mm, "end": v(-52.3, -0.64) * mm});
            skLineSegment(sketch, "E34.18.3.3", {"start": v(-51.22, -0.01) * mm, "end": v(-52.66, 2.49) * mm});
            skLineSegment(sketch, "E34.21.3.3", {"start": v(-52.66, 2.49) * mm, "end": v(-51.22, 4.99) * mm});
            skLineSegment(sketch, "E34.24.3.3", {"start": v(-51.22, 4.99) * mm, "end": v(-48.33, 4.99) * mm});
            skLineSegment(sketch, "E34.27.3.3", {"start": v(-48.33, 4.99) * mm, "end": v(-46.89, 2.49) * mm});
            skLineSegment(sketch, "E34.30.3.3", {"start": v(-46.89, 2.49) * mm, "end": v(-48.33, -0.01) * mm});
            skLineSegment(sketch, "E34.33.3.3", {"start": v(-48.33, -0.01) * mm, "end": v(-51.22, -0.01) * mm});
            skLineSegment(sketch, "E34.0.4.0", {"start": v(-45.64, 20.61) * mm, "end": v(-42.75, 20.61) * mm});
            skLineSegment(sketch, "E34.3.4.0", {"start": v(-47.08, 18.11) * mm, "end": v(-45.64, 20.61) * mm});
            skLineSegment(sketch, "E34.6.4.0", {"start": v(-45.64, 15.61) * mm, "end": v(-47.08, 18.11) * mm});
            skLineSegment(sketch, "E34.9.4.0", {"start": v(-42.75, 15.61) * mm, "end": v(-45.64, 15.61) * mm});
            skLineSegment(sketch, "E34.12.4.0", {"start": v(-41.3, 18.11) * mm, "end": v(-42.75, 15.61) * mm});
            skLineSegment(sketch, "E34.15.4.0", {"start": v(-42.75, 20.61) * mm, "end": v(-41.3, 18.11) * mm});
            skLineSegment(sketch, "E34.18.4.0", {"start": v(-40.22, 18.74) * mm, "end": v(-41.67, 21.24) * mm});
            skLineSegment(sketch, "E34.21.4.0", {"start": v(-41.67, 21.24) * mm, "end": v(-40.22, 23.74) * mm});
            skLineSegment(sketch, "E34.24.4.0", {"start": v(-40.22, 23.74) * mm, "end": v(-37.34, 23.74) * mm});
            skLineSegment(sketch, "E34.27.4.0", {"start": v(-37.34, 23.74) * mm, "end": v(-35.9, 21.24) * mm});
            skLineSegment(sketch, "E34.30.4.0", {"start": v(-35.9, 21.24) * mm, "end": v(-37.34, 18.74) * mm});
            skLineSegment(sketch, "E34.33.4.0", {"start": v(-37.34, 18.74) * mm, "end": v(-40.22, 18.74) * mm});
            skLineSegment(sketch, "E34.0.4.1", {"start": v(-45.64, 14.36) * mm, "end": v(-42.75, 14.36) * mm});
            skLineSegment(sketch, "E34.3.4.1", {"start": v(-47.08, 11.86) * mm, "end": v(-45.64, 14.36) * mm});
            skLineSegment(sketch, "E34.6.4.1", {"start": v(-45.64, 9.36) * mm, "end": v(-47.08, 11.86) * mm});
            skLineSegment(sketch, "E34.9.4.1", {"start": v(-42.75, 9.36) * mm, "end": v(-45.64, 9.36) * mm});
            skLineSegment(sketch, "E34.12.4.1", {"start": v(-41.3, 11.86) * mm, "end": v(-42.75, 9.36) * mm});
            skLineSegment(sketch, "E34.15.4.1", {"start": v(-42.75, 14.36) * mm, "end": v(-41.3, 11.86) * mm});
            skLineSegment(sketch, "E34.18.4.1", {"start": v(-40.22, 12.49) * mm, "end": v(-41.67, 14.99) * mm});
            skLineSegment(sketch, "E34.21.4.1", {"start": v(-41.67, 14.99) * mm, "end": v(-40.22, 17.49) * mm});
            skLineSegment(sketch, "E34.24.4.1", {"start": v(-40.22, 17.49) * mm, "end": v(-37.34, 17.49) * mm});
            skLineSegment(sketch, "E34.27.4.1", {"start": v(-37.34, 17.49) * mm, "end": v(-35.9, 14.99) * mm});
            skLineSegment(sketch, "E34.30.4.1", {"start": v(-35.9, 14.99) * mm, "end": v(-37.34, 12.49) * mm});
            skLineSegment(sketch, "E34.33.4.1", {"start": v(-37.34, 12.49) * mm, "end": v(-40.22, 12.49) * mm});
            skLineSegment(sketch, "E34.0.4.2", {"start": v(-45.64, 8.11) * mm, "end": v(-42.75, 8.11) * mm});
            skLineSegment(sketch, "E34.3.4.2", {"start": v(-47.08, 5.61) * mm, "end": v(-45.64, 8.11) * mm});
            skLineSegment(sketch, "E34.6.4.2", {"start": v(-45.64, 3.11) * mm, "end": v(-47.08, 5.61) * mm});
            skLineSegment(sketch, "E34.9.4.2", {"start": v(-42.75, 3.11) * mm, "end": v(-45.64, 3.11) * mm});
            skLineSegment(sketch, "E34.12.4.2", {"start": v(-41.3, 5.61) * mm, "end": v(-42.75, 3.11) * mm});
            skLineSegment(sketch, "E34.15.4.2", {"start": v(-42.75, 8.11) * mm, "end": v(-41.3, 5.61) * mm});
            skLineSegment(sketch, "E34.18.4.2", {"start": v(-40.22, 6.24) * mm, "end": v(-41.67, 8.74) * mm});
            skLineSegment(sketch, "E34.21.4.2", {"start": v(-41.67, 8.74) * mm, "end": v(-40.22, 11.24) * mm});
            skLineSegment(sketch, "E34.24.4.2", {"start": v(-40.22, 11.24) * mm, "end": v(-37.34, 11.24) * mm});
            skLineSegment(sketch, "E34.27.4.2", {"start": v(-37.34, 11.24) * mm, "end": v(-35.9, 8.74) * mm});
            skLineSegment(sketch, "E34.30.4.2", {"start": v(-35.9, 8.74) * mm, "end": v(-37.34, 6.24) * mm});
            skLineSegment(sketch, "E34.33.4.2", {"start": v(-37.34, 6.24) * mm, "end": v(-40.22, 6.24) * mm});
            skLineSegment(sketch, "E34.0.4.3", {"start": v(-45.64, 1.86) * mm, "end": v(-42.75, 1.86) * mm});
            skLineSegment(sketch, "E34.3.4.3", {"start": v(-47.08, -0.64) * mm, "end": v(-45.64, 1.86) * mm});
            skLineSegment(sketch, "E34.6.4.3", {"start": v(-45.64, -3.14) * mm, "end": v(-47.08, -0.64) * mm});
            skLineSegment(sketch, "E34.9.4.3", {"start": v(-42.75, -3.14) * mm, "end": v(-45.64, -3.14) * mm});
            skLineSegment(sketch, "E34.12.4.3", {"start": v(-41.3, -0.64) * mm, "end": v(-42.75, -3.14) * mm});
            skLineSegment(sketch, "E34.15.4.3", {"start": v(-42.75, 1.86) * mm, "end": v(-41.3, -0.64) * mm});
            skLineSegment(sketch, "E34.18.4.3", {"start": v(-40.22, -0.01) * mm, "end": v(-41.67, 2.49) * mm});
            skLineSegment(sketch, "E34.21.4.3", {"start": v(-41.67, 2.49) * mm, "end": v(-40.22, 4.99) * mm});
            skLineSegment(sketch, "E34.24.4.3", {"start": v(-40.22, 4.99) * mm, "end": v(-37.34, 4.99) * mm});
            skLineSegment(sketch, "E34.27.4.3", {"start": v(-37.34, 4.99) * mm, "end": v(-35.9, 2.49) * mm});
            skLineSegment(sketch, "E34.30.4.3", {"start": v(-35.9, 2.49) * mm, "end": v(-37.34, -0.01) * mm});
            skLineSegment(sketch, "E34.33.4.3", {"start": v(-37.34, -0.01) * mm, "end": v(-40.22, -0.01) * mm});
            skLineSegment(sketch, "E34.0.5.0", {"start": v(-34.64, 20.61) * mm, "end": v(-31.76, 20.61) * mm});
            skLineSegment(sketch, "E34.3.5.0", {"start": v(-36.09, 18.11) * mm, "end": v(-34.64, 20.61) * mm});
            skLineSegment(sketch, "E34.6.5.0", {"start": v(-34.64, 15.61) * mm, "end": v(-36.09, 18.11) * mm});
            skLineSegment(sketch, "E34.9.5.0", {"start": v(-31.76, 15.61) * mm, "end": v(-34.64, 15.61) * mm});
            skLineSegment(sketch, "E34.12.5.0", {"start": v(-30.31, 18.11) * mm, "end": v(-31.76, 15.61) * mm});
            skLineSegment(sketch, "E34.15.5.0", {"start": v(-31.76, 20.61) * mm, "end": v(-30.31, 18.11) * mm});
            skLineSegment(sketch, "E34.18.5.0", {"start": v(-29.23, 18.74) * mm, "end": v(-30.67, 21.24) * mm});
            skLineSegment(sketch, "E34.21.5.0", {"start": v(-30.67, 21.24) * mm, "end": v(-29.23, 23.74) * mm});
            skLineSegment(sketch, "E34.24.5.0", {"start": v(-29.23, 23.74) * mm, "end": v(-26.34, 23.74) * mm});
            skLineSegment(sketch, "E34.27.5.0", {"start": v(-26.34, 23.74) * mm, "end": v(-24.9, 21.24) * mm});
            skLineSegment(sketch, "E34.30.5.0", {"start": v(-24.9, 21.24) * mm, "end": v(-26.34, 18.74) * mm});
            skLineSegment(sketch, "E34.33.5.0", {"start": v(-26.34, 18.74) * mm, "end": v(-29.23, 18.74) * mm});
            skLineSegment(sketch, "E34.0.5.1", {"start": v(-34.64, 14.36) * mm, "end": v(-31.76, 14.36) * mm});
            skLineSegment(sketch, "E34.3.5.1", {"start": v(-36.09, 11.86) * mm, "end": v(-34.64, 14.36) * mm});
            skLineSegment(sketch, "E34.6.5.1", {"start": v(-34.64, 9.36) * mm, "end": v(-36.09, 11.86) * mm});
            skLineSegment(sketch, "E34.9.5.1", {"start": v(-31.76, 9.36) * mm, "end": v(-34.64, 9.36) * mm});
            skLineSegment(sketch, "E34.12.5.1", {"start": v(-30.31, 11.86) * mm, "end": v(-31.76, 9.36) * mm});
            skLineSegment(sketch, "E34.15.5.1", {"start": v(-31.76, 14.36) * mm, "end": v(-30.31, 11.86) * mm});
            skLineSegment(sketch, "E34.18.5.1", {"start": v(-29.23, 12.49) * mm, "end": v(-30.67, 14.99) * mm});
            skLineSegment(sketch, "E34.21.5.1", {"start": v(-30.67, 14.99) * mm, "end": v(-29.23, 17.49) * mm});
            skLineSegment(sketch, "E34.24.5.1", {"start": v(-29.23, 17.49) * mm, "end": v(-26.34, 17.49) * mm});
            skLineSegment(sketch, "E34.27.5.1", {"start": v(-26.34, 17.49) * mm, "end": v(-24.9, 14.99) * mm});
            skLineSegment(sketch, "E34.30.5.1", {"start": v(-24.9, 14.99) * mm, "end": v(-26.34, 12.49) * mm});
            skLineSegment(sketch, "E34.33.5.1", {"start": v(-26.34, 12.49) * mm, "end": v(-29.23, 12.49) * mm});
            skLineSegment(sketch, "E34.0.5.2", {"start": v(-34.64, 8.11) * mm, "end": v(-31.76, 8.11) * mm});
            skLineSegment(sketch, "E34.3.5.2", {"start": v(-36.09, 5.61) * mm, "end": v(-34.64, 8.11) * mm});
            skLineSegment(sketch, "E34.6.5.2", {"start": v(-34.64, 3.11) * mm, "end": v(-36.09, 5.61) * mm});
            skLineSegment(sketch, "E34.9.5.2", {"start": v(-31.76, 3.11) * mm, "end": v(-34.64, 3.11) * mm});
            skLineSegment(sketch, "E34.12.5.2", {"start": v(-30.31, 5.61) * mm, "end": v(-31.76, 3.11) * mm});
            skLineSegment(sketch, "E34.15.5.2", {"start": v(-31.76, 8.11) * mm, "end": v(-30.31, 5.61) * mm});
            skLineSegment(sketch, "E34.18.5.2", {"start": v(-29.23, 6.24) * mm, "end": v(-30.67, 8.74) * mm});
            skLineSegment(sketch, "E34.21.5.2", {"start": v(-30.67, 8.74) * mm, "end": v(-29.23, 11.24) * mm});
            skLineSegment(sketch, "E34.24.5.2", {"start": v(-29.23, 11.24) * mm, "end": v(-26.34, 11.24) * mm});
            skLineSegment(sketch, "E34.27.5.2", {"start": v(-26.34, 11.24) * mm, "end": v(-24.9, 8.74) * mm});
            skLineSegment(sketch, "E34.30.5.2", {"start": v(-24.9, 8.74) * mm, "end": v(-26.34, 6.24) * mm});
            skLineSegment(sketch, "E34.33.5.2", {"start": v(-26.34, 6.24) * mm, "end": v(-29.23, 6.24) * mm});
            skLineSegment(sketch, "E34.0.5.3", {"start": v(-34.64, 1.86) * mm, "end": v(-31.76, 1.86) * mm});
            skLineSegment(sketch, "E34.3.5.3", {"start": v(-36.09, -0.64) * mm, "end": v(-34.64, 1.86) * mm});
            skLineSegment(sketch, "E34.6.5.3", {"start": v(-34.64, -3.14) * mm, "end": v(-36.09, -0.64) * mm});
            skLineSegment(sketch, "E34.9.5.3", {"start": v(-31.76, -3.14) * mm, "end": v(-34.64, -3.14) * mm});
            skLineSegment(sketch, "E34.12.5.3", {"start": v(-30.31, -0.64) * mm, "end": v(-31.76, -3.14) * mm});
            skLineSegment(sketch, "E34.15.5.3", {"start": v(-31.76, 1.86) * mm, "end": v(-30.31, -0.64) * mm});
            skLineSegment(sketch, "E34.18.5.3", {"start": v(-29.23, -0.01) * mm, "end": v(-30.67, 2.49) * mm});
            skLineSegment(sketch, "E34.21.5.3", {"start": v(-30.67, 2.49) * mm, "end": v(-29.23, 4.99) * mm});
            skLineSegment(sketch, "E34.24.5.3", {"start": v(-29.23, 4.99) * mm, "end": v(-26.34, 4.99) * mm});
            skLineSegment(sketch, "E34.27.5.3", {"start": v(-26.34, 4.99) * mm, "end": v(-24.9, 2.49) * mm});
            skLineSegment(sketch, "E34.30.5.3", {"start": v(-24.9, 2.49) * mm, "end": v(-26.34, -0.01) * mm});
            skLineSegment(sketch, "E34.33.5.3", {"start": v(-26.34, -0.01) * mm, "end": v(-29.23, -0.01) * mm});
            skLineSegment(sketch, "E34.0.6.0", {"start": v(-23.65, 20.61) * mm, "end": v(-20.76, 20.61) * mm});
            skLineSegment(sketch, "E34.3.6.0", {"start": v(-25.1, 18.11) * mm, "end": v(-23.65, 20.61) * mm});
            skLineSegment(sketch, "E34.6.6.0", {"start": v(-23.65, 15.61) * mm, "end": v(-25.1, 18.11) * mm});
            skLineSegment(sketch, "E34.9.6.0", {"start": v(-20.76, 15.61) * mm, "end": v(-23.65, 15.61) * mm});
            skLineSegment(sketch, "E34.12.6.0", {"start": v(-19.32, 18.11) * mm, "end": v(-20.76, 15.61) * mm});
            skLineSegment(sketch, "E34.15.6.0", {"start": v(-20.76, 20.61) * mm, "end": v(-19.32, 18.11) * mm});
            skLineSegment(sketch, "E34.18.6.0", {"start": v(-18.24, 18.74) * mm, "end": v(-19.68, 21.24) * mm});
            skLineSegment(sketch, "E34.21.6.0", {"start": v(-19.68, 21.24) * mm, "end": v(-18.24, 23.74) * mm});
            skLineSegment(sketch, "E34.24.6.0", {"start": v(-18.24, 23.74) * mm, "end": v(-15.35, 23.74) * mm});
            skLineSegment(sketch, "E34.27.6.0", {"start": v(-15.35, 23.74) * mm, "end": v(-13.9, 21.24) * mm});
            skLineSegment(sketch, "E34.30.6.0", {"start": v(-13.9, 21.24) * mm, "end": v(-15.35, 18.74) * mm});
            skLineSegment(sketch, "E34.33.6.0", {"start": v(-15.35, 18.74) * mm, "end": v(-18.24, 18.74) * mm});
            skLineSegment(sketch, "E34.0.6.1", {"start": v(-23.65, 14.36) * mm, "end": v(-20.76, 14.36) * mm});
            skLineSegment(sketch, "E34.3.6.1", {"start": v(-25.1, 11.86) * mm, "end": v(-23.65, 14.36) * mm});
            skLineSegment(sketch, "E34.6.6.1", {"start": v(-23.65, 9.36) * mm, "end": v(-25.1, 11.86) * mm});
            skLineSegment(sketch, "E34.9.6.1", {"start": v(-20.76, 9.36) * mm, "end": v(-23.65, 9.36) * mm});
            skLineSegment(sketch, "E34.12.6.1", {"start": v(-19.32, 11.86) * mm, "end": v(-20.76, 9.36) * mm});
            skLineSegment(sketch, "E34.15.6.1", {"start": v(-20.76, 14.36) * mm, "end": v(-19.32, 11.86) * mm});
            skLineSegment(sketch, "E34.18.6.1", {"start": v(-18.24, 12.49) * mm, "end": v(-19.68, 14.99) * mm});
            skLineSegment(sketch, "E34.21.6.1", {"start": v(-19.68, 14.99) * mm, "end": v(-18.24, 17.49) * mm});
            skLineSegment(sketch, "E34.24.6.1", {"start": v(-18.24, 17.49) * mm, "end": v(-15.35, 17.49) * mm});
            skLineSegment(sketch, "E34.27.6.1", {"start": v(-15.35, 17.49) * mm, "end": v(-13.9, 14.99) * mm});
            skLineSegment(sketch, "E34.30.6.1", {"start": v(-13.9, 14.99) * mm, "end": v(-15.35, 12.49) * mm});
            skLineSegment(sketch, "E34.33.6.1", {"start": v(-15.35, 12.49) * mm, "end": v(-18.24, 12.49) * mm});
            skLineSegment(sketch, "E34.0.6.2", {"start": v(-23.65, 8.11) * mm, "end": v(-20.76, 8.11) * mm});
            skLineSegment(sketch, "E34.3.6.2", {"start": v(-25.1, 5.61) * mm, "end": v(-23.65, 8.11) * mm});
            skLineSegment(sketch, "E34.6.6.2", {"start": v(-23.65, 3.11) * mm, "end": v(-25.1, 5.61) * mm});
            skLineSegment(sketch, "E34.9.6.2", {"start": v(-20.76, 3.11) * mm, "end": v(-23.65, 3.11) * mm});
            skLineSegment(sketch, "E34.12.6.2", {"start": v(-19.32, 5.61) * mm, "end": v(-20.76, 3.11) * mm});
            skLineSegment(sketch, "E34.15.6.2", {"start": v(-20.76, 8.11) * mm, "end": v(-19.32, 5.61) * mm});
            skLineSegment(sketch, "E34.18.6.2", {"start": v(-18.24, 6.24) * mm, "end": v(-19.68, 8.74) * mm});
            skLineSegment(sketch, "E34.21.6.2", {"start": v(-19.68, 8.74) * mm, "end": v(-18.24, 11.24) * mm});
            skLineSegment(sketch, "E34.24.6.2", {"start": v(-18.24, 11.24) * mm, "end": v(-15.35, 11.24) * mm});
            skLineSegment(sketch, "E34.27.6.2", {"start": v(-15.35, 11.24) * mm, "end": v(-13.9, 8.74) * mm});
            skLineSegment(sketch, "E34.30.6.2", {"start": v(-13.9, 8.74) * mm, "end": v(-15.35, 6.24) * mm});
            skLineSegment(sketch, "E34.33.6.2", {"start": v(-15.35, 6.24) * mm, "end": v(-18.24, 6.24) * mm});
            skLineSegment(sketch, "E34.0.6.3", {"start": v(-23.65, 1.86) * mm, "end": v(-20.76, 1.86) * mm});
            skLineSegment(sketch, "E34.3.6.3", {"start": v(-25.1, -0.64) * mm, "end": v(-23.65, 1.86) * mm});
            skLineSegment(sketch, "E34.6.6.3", {"start": v(-23.65, -3.14) * mm, "end": v(-25.1, -0.64) * mm});
            skLineSegment(sketch, "E34.9.6.3", {"start": v(-20.76, -3.14) * mm, "end": v(-23.65, -3.14) * mm});
            skLineSegment(sketch, "E34.12.6.3", {"start": v(-19.32, -0.64) * mm, "end": v(-20.76, -3.14) * mm});
            skLineSegment(sketch, "E34.15.6.3", {"start": v(-20.76, 1.86) * mm, "end": v(-19.32, -0.64) * mm});
            skLineSegment(sketch, "E34.18.6.3", {"start": v(-18.24, -0.01) * mm, "end": v(-19.68, 2.49) * mm});
            skLineSegment(sketch, "E34.21.6.3", {"start": v(-19.68, 2.49) * mm, "end": v(-18.24, 4.99) * mm});
            skLineSegment(sketch, "E34.24.6.3", {"start": v(-18.24, 4.99) * mm, "end": v(-15.35, 4.99) * mm});
            skLineSegment(sketch, "E34.27.6.3", {"start": v(-15.35, 4.99) * mm, "end": v(-13.9, 2.49) * mm});
            skLineSegment(sketch, "E34.30.6.3", {"start": v(-13.9, 2.49) * mm, "end": v(-15.35, -0.01) * mm});
            skLineSegment(sketch, "E34.33.6.3", {"start": v(-15.35, -0.01) * mm, "end": v(-18.24, -0.01) * mm});
            skLineSegment(sketch, "E34.0.7.0", {"start": v(-12.66, 20.61) * mm, "end": v(-9.77, 20.61) * mm});
            skLineSegment(sketch, "E34.3.7.0", {"start": v(-14.1, 18.11) * mm, "end": v(-12.66, 20.61) * mm});
            skLineSegment(sketch, "E34.6.7.0", {"start": v(-12.66, 15.61) * mm, "end": v(-14.1, 18.11) * mm});
            skLineSegment(sketch, "E34.9.7.0", {"start": v(-9.77, 15.61) * mm, "end": v(-12.66, 15.61) * mm});
            skLineSegment(sketch, "E34.12.7.0", {"start": v(-8.33, 18.11) * mm, "end": v(-9.77, 15.61) * mm});
            skLineSegment(sketch, "E34.15.7.0", {"start": v(-9.77, 20.61) * mm, "end": v(-8.33, 18.11) * mm});
            skLineSegment(sketch, "E34.18.7.0", {"start": v(-7.24, 18.74) * mm, "end": v(-8.69, 21.24) * mm});
            skLineSegment(sketch, "E34.21.7.0", {"start": v(-8.69, 21.24) * mm, "end": v(-7.24, 23.74) * mm});
            skLineSegment(sketch, "E34.24.7.0", {"start": v(-7.24, 23.74) * mm, "end": v(-4.36, 23.74) * mm});
            skLineSegment(sketch, "E34.27.7.0", {"start": v(-4.36, 23.74) * mm, "end": v(-2.91, 21.24) * mm});
            skLineSegment(sketch, "E34.30.7.0", {"start": v(-2.91, 21.24) * mm, "end": v(-4.36, 18.74) * mm});
            skLineSegment(sketch, "E34.33.7.0", {"start": v(-4.36, 18.74) * mm, "end": v(-7.24, 18.74) * mm});
            skLineSegment(sketch, "E34.0.7.1", {"start": v(-12.66, 14.36) * mm, "end": v(-9.77, 14.36) * mm});
            skLineSegment(sketch, "E34.3.7.1", {"start": v(-14.1, 11.86) * mm, "end": v(-12.66, 14.36) * mm});
            skLineSegment(sketch, "E34.6.7.1", {"start": v(-12.66, 9.36) * mm, "end": v(-14.1, 11.86) * mm});
            skLineSegment(sketch, "E34.9.7.1", {"start": v(-9.77, 9.36) * mm, "end": v(-12.66, 9.36) * mm});
            skLineSegment(sketch, "E34.12.7.1", {"start": v(-8.33, 11.86) * mm, "end": v(-9.77, 9.36) * mm});
            skLineSegment(sketch, "E34.15.7.1", {"start": v(-9.77, 14.36) * mm, "end": v(-8.33, 11.86) * mm});
            skLineSegment(sketch, "E34.18.7.1", {"start": v(-7.24, 12.49) * mm, "end": v(-8.69, 14.99) * mm});
            skLineSegment(sketch, "E34.21.7.1", {"start": v(-8.69, 14.99) * mm, "end": v(-7.24, 17.49) * mm});
            skLineSegment(sketch, "E34.24.7.1", {"start": v(-7.24, 17.49) * mm, "end": v(-4.36, 17.49) * mm});
            skLineSegment(sketch, "E34.27.7.1", {"start": v(-4.36, 17.49) * mm, "end": v(-2.91, 14.99) * mm});
            skLineSegment(sketch, "E34.30.7.1", {"start": v(-2.91, 14.99) * mm, "end": v(-4.36, 12.49) * mm});
            skLineSegment(sketch, "E34.33.7.1", {"start": v(-4.36, 12.49) * mm, "end": v(-7.24, 12.49) * mm});
            skLineSegment(sketch, "E34.0.7.2", {"start": v(-12.66, 8.11) * mm, "end": v(-9.77, 8.11) * mm});
            skLineSegment(sketch, "E34.3.7.2", {"start": v(-14.1, 5.61) * mm, "end": v(-12.66, 8.11) * mm});
            skLineSegment(sketch, "E34.6.7.2", {"start": v(-12.66, 3.11) * mm, "end": v(-14.1, 5.61) * mm});
            skLineSegment(sketch, "E34.9.7.2", {"start": v(-9.77, 3.11) * mm, "end": v(-12.66, 3.11) * mm});
            skLineSegment(sketch, "E34.12.7.2", {"start": v(-8.33, 5.61) * mm, "end": v(-9.77, 3.11) * mm});
            skLineSegment(sketch, "E34.15.7.2", {"start": v(-9.77, 8.11) * mm, "end": v(-8.33, 5.61) * mm});
            skLineSegment(sketch, "E34.18.7.2", {"start": v(-7.24, 6.24) * mm, "end": v(-8.69, 8.74) * mm});
            skLineSegment(sketch, "E34.21.7.2", {"start": v(-8.69, 8.74) * mm, "end": v(-7.24, 11.24) * mm});
            skLineSegment(sketch, "E34.24.7.2", {"start": v(-7.24, 11.24) * mm, "end": v(-4.36, 11.24) * mm});
            skLineSegment(sketch, "E34.27.7.2", {"start": v(-4.36, 11.24) * mm, "end": v(-2.91, 8.74) * mm});
            skLineSegment(sketch, "E34.30.7.2", {"start": v(-2.91, 8.74) * mm, "end": v(-4.36, 6.24) * mm});
            skLineSegment(sketch, "E34.33.7.2", {"start": v(-4.36, 6.24) * mm, "end": v(-7.24, 6.24) * mm});
            skLineSegment(sketch, "E34.0.7.3", {"start": v(-12.66, 1.86) * mm, "end": v(-9.77, 1.86) * mm});
            skLineSegment(sketch, "E34.3.7.3", {"start": v(-14.1, -0.64) * mm, "end": v(-12.66, 1.86) * mm});
            skLineSegment(sketch, "E34.6.7.3", {"start": v(-12.66, -3.14) * mm, "end": v(-14.1, -0.64) * mm});
            skLineSegment(sketch, "E34.9.7.3", {"start": v(-9.77, -3.14) * mm, "end": v(-12.66, -3.14) * mm});
            skLineSegment(sketch, "E34.12.7.3", {"start": v(-8.33, -0.64) * mm, "end": v(-9.77, -3.14) * mm});
            skLineSegment(sketch, "E34.15.7.3", {"start": v(-9.77, 1.86) * mm, "end": v(-8.33, -0.64) * mm});
            skLineSegment(sketch, "E34.18.7.3", {"start": v(-7.24, -0.01) * mm, "end": v(-8.69, 2.49) * mm});
            skLineSegment(sketch, "E34.21.7.3", {"start": v(-8.69, 2.49) * mm, "end": v(-7.24, 4.99) * mm});
            skLineSegment(sketch, "E34.24.7.3", {"start": v(-7.24, 4.99) * mm, "end": v(-4.36, 4.99) * mm});
            skLineSegment(sketch, "E34.27.7.3", {"start": v(-4.36, 4.99) * mm, "end": v(-2.91, 2.49) * mm});
            skLineSegment(sketch, "E34.30.7.3", {"start": v(-2.91, 2.49) * mm, "end": v(-4.36, -0.01) * mm});
            skLineSegment(sketch, "E34.33.7.3", {"start": v(-4.36, -0.01) * mm, "end": v(-7.24, -0.01) * mm});
            skLineSegment(sketch, "E34.0.8.0", {"start": v(-1.66, 20.61) * mm, "end": v(1.22, 20.61) * mm});
            skLineSegment(sketch, "E34.3.8.0", {"start": v(-3.1, 18.11) * mm, "end": v(-1.66, 20.61) * mm});
            skLineSegment(sketch, "E34.6.8.0", {"start": v(-1.66, 15.61) * mm, "end": v(-3.1, 18.11) * mm});
            skLineSegment(sketch, "E34.9.8.0", {"start": v(1.22, 15.61) * mm, "end": v(-1.66, 15.61) * mm});
            skLineSegment(sketch, "E34.12.8.0", {"start": v(2.67, 18.11) * mm, "end": v(1.22, 15.61) * mm});
            skLineSegment(sketch, "E34.15.8.0", {"start": v(1.22, 20.61) * mm, "end": v(2.67, 18.11) * mm});
            skLineSegment(sketch, "E34.18.8.0", {"start": v(3.75, 18.74) * mm, "end": v(2.3, 21.24) * mm});
            skLineSegment(sketch, "E34.21.8.0", {"start": v(2.3, 21.24) * mm, "end": v(3.75, 23.74) * mm});
            skLineSegment(sketch, "E34.24.8.0", {"start": v(3.75, 23.74) * mm, "end": v(6.64, 23.74) * mm});
            skLineSegment(sketch, "E34.27.8.0", {"start": v(6.64, 23.74) * mm, "end": v(8.08, 21.24) * mm});
            skLineSegment(sketch, "E34.30.8.0", {"start": v(8.08, 21.24) * mm, "end": v(6.64, 18.74) * mm});
            skLineSegment(sketch, "E34.33.8.0", {"start": v(6.64, 18.74) * mm, "end": v(3.75, 18.74) * mm});
            skLineSegment(sketch, "E34.0.8.1", {"start": v(-1.66, 14.36) * mm, "end": v(1.22, 14.36) * mm});
            skLineSegment(sketch, "E34.3.8.1", {"start": v(-3.1, 11.86) * mm, "end": v(-1.66, 14.36) * mm});
            skLineSegment(sketch, "E34.6.8.1", {"start": v(-1.66, 9.36) * mm, "end": v(-3.1, 11.86) * mm});
            skLineSegment(sketch, "E34.9.8.1", {"start": v(1.22, 9.36) * mm, "end": v(-1.66, 9.36) * mm});
            skLineSegment(sketch, "E34.12.8.1", {"start": v(2.67, 11.86) * mm, "end": v(1.22, 9.36) * mm});
            skLineSegment(sketch, "E34.15.8.1", {"start": v(1.22, 14.36) * mm, "end": v(2.67, 11.86) * mm});
            skLineSegment(sketch, "E34.18.8.1", {"start": v(3.75, 12.49) * mm, "end": v(2.3, 14.99) * mm});
            skLineSegment(sketch, "E34.21.8.1", {"start": v(2.3, 14.99) * mm, "end": v(3.75, 17.49) * mm});
            skLineSegment(sketch, "E34.24.8.1", {"start": v(3.75, 17.49) * mm, "end": v(6.64, 17.49) * mm});
            skLineSegment(sketch, "E34.27.8.1", {"start": v(6.64, 17.49) * mm, "end": v(8.08, 14.99) * mm});
            skLineSegment(sketch, "E34.30.8.1", {"start": v(8.08, 14.99) * mm, "end": v(6.64, 12.49) * mm});
            skLineSegment(sketch, "E34.33.8.1", {"start": v(6.64, 12.49) * mm, "end": v(3.75, 12.49) * mm});
            skLineSegment(sketch, "E34.0.8.2", {"start": v(-1.66, 8.11) * mm, "end": v(1.22, 8.11) * mm});
            skLineSegment(sketch, "E34.3.8.2", {"start": v(-3.1, 5.61) * mm, "end": v(-1.66, 8.11) * mm});
            skLineSegment(sketch, "E34.6.8.2", {"start": v(-1.66, 3.11) * mm, "end": v(-3.1, 5.61) * mm});
            skLineSegment(sketch, "E34.9.8.2", {"start": v(1.22, 3.11) * mm, "end": v(-1.66, 3.11) * mm});
            skLineSegment(sketch, "E34.12.8.2", {"start": v(2.67, 5.61) * mm, "end": v(1.22, 3.11) * mm});
            skLineSegment(sketch, "E34.15.8.2", {"start": v(1.22, 8.11) * mm, "end": v(2.67, 5.61) * mm});
            skLineSegment(sketch, "E34.18.8.2", {"start": v(3.75, 6.24) * mm, "end": v(2.3, 8.74) * mm});
            skLineSegment(sketch, "E34.21.8.2", {"start": v(2.3, 8.74) * mm, "end": v(3.75, 11.24) * mm});
            skLineSegment(sketch, "E34.24.8.2", {"start": v(3.75, 11.24) * mm, "end": v(6.64, 11.24) * mm});
            skLineSegment(sketch, "E34.27.8.2", {"start": v(6.64, 11.24) * mm, "end": v(8.08, 8.74) * mm});
            skLineSegment(sketch, "E34.30.8.2", {"start": v(8.08, 8.74) * mm, "end": v(6.64, 6.24) * mm});
            skLineSegment(sketch, "E34.33.8.2", {"start": v(6.64, 6.24) * mm, "end": v(3.75, 6.24) * mm});
            skLineSegment(sketch, "E34.0.8.3", {"start": v(-1.66, 1.86) * mm, "end": v(1.22, 1.86) * mm});
            skLineSegment(sketch, "E34.3.8.3", {"start": v(-3.1, -0.64) * mm, "end": v(-1.66, 1.86) * mm});
            skLineSegment(sketch, "E34.6.8.3", {"start": v(-1.66, -3.14) * mm, "end": v(-3.1, -0.64) * mm});
            skLineSegment(sketch, "E34.9.8.3", {"start": v(1.22, -3.14) * mm, "end": v(-1.66, -3.14) * mm});
            skLineSegment(sketch, "E34.12.8.3", {"start": v(2.67, -0.64) * mm, "end": v(1.22, -3.14) * mm});
            skLineSegment(sketch, "E34.15.8.3", {"start": v(1.22, 1.86) * mm, "end": v(2.67, -0.64) * mm});
            skLineSegment(sketch, "E34.18.8.3", {"start": v(3.75, -0.01) * mm, "end": v(2.3, 2.49) * mm});
            skLineSegment(sketch, "E34.21.8.3", {"start": v(2.3, 2.49) * mm, "end": v(3.75, 4.99) * mm});
            skLineSegment(sketch, "E34.24.8.3", {"start": v(3.75, 4.99) * mm, "end": v(6.64, 4.99) * mm});
            skLineSegment(sketch, "E34.27.8.3", {"start": v(6.64, 4.99) * mm, "end": v(8.08, 2.49) * mm});
            skLineSegment(sketch, "E34.30.8.3", {"start": v(8.08, 2.49) * mm, "end": v(6.64, -0.01) * mm});
            skLineSegment(sketch, "E34.33.8.3", {"start": v(6.64, -0.01) * mm, "end": v(3.75, -0.01) * mm});
            skLineSegment(sketch, "E34.0.9.0", {"start": v(9.33, 20.61) * mm, "end": v(12.22, 20.61) * mm});
            skLineSegment(sketch, "E34.3.9.0", {"start": v(7.89, 18.11) * mm, "end": v(9.33, 20.61) * mm});
            skLineSegment(sketch, "E34.6.9.0", {"start": v(9.33, 15.61) * mm, "end": v(7.89, 18.11) * mm});
            skLineSegment(sketch, "E34.9.9.0", {"start": v(12.22, 15.61) * mm, "end": v(9.33, 15.61) * mm});
            skLineSegment(sketch, "E34.12.9.0", {"start": v(13.66, 18.11) * mm, "end": v(12.22, 15.61) * mm});
            skLineSegment(sketch, "E34.15.9.0", {"start": v(12.22, 20.61) * mm, "end": v(13.66, 18.11) * mm});
            skLineSegment(sketch, "E34.18.9.0", {"start": v(14.74, 18.74) * mm, "end": v(13.3, 21.24) * mm});
            skLineSegment(sketch, "E34.21.9.0", {"start": v(13.3, 21.24) * mm, "end": v(14.74, 23.74) * mm});
            skLineSegment(sketch, "E34.24.9.0", {"start": v(14.74, 23.74) * mm, "end": v(17.63, 23.74) * mm});
            skLineSegment(sketch, "E34.27.9.0", {"start": v(17.63, 23.74) * mm, "end": v(19.07, 21.24) * mm});
            skLineSegment(sketch, "E34.30.9.0", {"start": v(19.07, 21.24) * mm, "end": v(17.63, 18.74) * mm});
            skLineSegment(sketch, "E34.33.9.0", {"start": v(17.63, 18.74) * mm, "end": v(14.74, 18.74) * mm});
            skLineSegment(sketch, "E34.0.9.1", {"start": v(9.33, 14.36) * mm, "end": v(12.22, 14.36) * mm});
            skLineSegment(sketch, "E34.3.9.1", {"start": v(7.89, 11.86) * mm, "end": v(9.33, 14.36) * mm});
            skLineSegment(sketch, "E34.6.9.1", {"start": v(9.33, 9.36) * mm, "end": v(7.89, 11.86) * mm});
            skLineSegment(sketch, "E34.9.9.1", {"start": v(12.22, 9.36) * mm, "end": v(9.33, 9.36) * mm});
            skLineSegment(sketch, "E34.12.9.1", {"start": v(13.66, 11.86) * mm, "end": v(12.22, 9.36) * mm});
            skLineSegment(sketch, "E34.15.9.1", {"start": v(12.22, 14.36) * mm, "end": v(13.66, 11.86) * mm});
            skLineSegment(sketch, "E34.18.9.1", {"start": v(14.74, 12.49) * mm, "end": v(13.3, 14.99) * mm});
            skLineSegment(sketch, "E34.21.9.1", {"start": v(13.3, 14.99) * mm, "end": v(14.74, 17.49) * mm});
            skLineSegment(sketch, "E34.24.9.1", {"start": v(14.74, 17.49) * mm, "end": v(17.63, 17.49) * mm});
            skLineSegment(sketch, "E34.27.9.1", {"start": v(17.63, 17.49) * mm, "end": v(19.07, 14.99) * mm});
            skLineSegment(sketch, "E34.30.9.1", {"start": v(19.07, 14.99) * mm, "end": v(17.63, 12.49) * mm});
            skLineSegment(sketch, "E34.33.9.1", {"start": v(17.63, 12.49) * mm, "end": v(14.74, 12.49) * mm});
            skLineSegment(sketch, "E34.0.9.2", {"start": v(9.33, 8.11) * mm, "end": v(12.22, 8.11) * mm});
            skLineSegment(sketch, "E34.3.9.2", {"start": v(7.89, 5.61) * mm, "end": v(9.33, 8.11) * mm});
            skLineSegment(sketch, "E34.6.9.2", {"start": v(9.33, 3.11) * mm, "end": v(7.89, 5.61) * mm});
            skLineSegment(sketch, "E34.9.9.2", {"start": v(12.22, 3.11) * mm, "end": v(9.33, 3.11) * mm});
            skLineSegment(sketch, "E34.12.9.2", {"start": v(13.66, 5.61) * mm, "end": v(12.22, 3.11) * mm});
            skLineSegment(sketch, "E34.15.9.2", {"start": v(12.22, 8.11) * mm, "end": v(13.66, 5.61) * mm});
            skLineSegment(sketch, "E34.18.9.2", {"start": v(14.74, 6.24) * mm, "end": v(13.3, 8.74) * mm});
            skLineSegment(sketch, "E34.21.9.2", {"start": v(13.3, 8.74) * mm, "end": v(14.74, 11.24) * mm});
            skLineSegment(sketch, "E34.24.9.2", {"start": v(14.74, 11.24) * mm, "end": v(17.63, 11.24) * mm});
            skLineSegment(sketch, "E34.27.9.2", {"start": v(17.63, 11.24) * mm, "end": v(19.07, 8.74) * mm});
            skLineSegment(sketch, "E34.30.9.2", {"start": v(19.07, 8.74) * mm, "end": v(17.63, 6.24) * mm});
            skLineSegment(sketch, "E34.33.9.2", {"start": v(17.63, 6.24) * mm, "end": v(14.74, 6.24) * mm});
            skLineSegment(sketch, "E34.0.9.3", {"start": v(9.33, 1.86) * mm, "end": v(12.22, 1.86) * mm});
            skLineSegment(sketch, "E34.3.9.3", {"start": v(7.89, -0.64) * mm, "end": v(9.33, 1.86) * mm});
            skLineSegment(sketch, "E34.6.9.3", {"start": v(9.33, -3.14) * mm, "end": v(7.89, -0.64) * mm});
            skLineSegment(sketch, "E34.9.9.3", {"start": v(12.22, -3.14) * mm, "end": v(9.33, -3.14) * mm});
            skLineSegment(sketch, "E34.12.9.3", {"start": v(13.66, -0.64) * mm, "end": v(12.22, -3.14) * mm});
            skLineSegment(sketch, "E34.15.9.3", {"start": v(12.22, 1.86) * mm, "end": v(13.66, -0.64) * mm});
            skLineSegment(sketch, "E34.18.9.3", {"start": v(14.74, -0.01) * mm, "end": v(13.3, 2.49) * mm});
            skLineSegment(sketch, "E34.21.9.3", {"start": v(13.3, 2.49) * mm, "end": v(14.74, 4.99) * mm});
            skLineSegment(sketch, "E34.24.9.3", {"start": v(14.74, 4.99) * mm, "end": v(17.63, 4.99) * mm});
            skLineSegment(sketch, "E34.27.9.3", {"start": v(17.63, 4.99) * mm, "end": v(19.07, 2.49) * mm});
            skLineSegment(sketch, "E34.30.9.3", {"start": v(19.07, 2.49) * mm, "end": v(17.63, -0.01) * mm});
            skLineSegment(sketch, "E34.33.9.3", {"start": v(17.63, -0.01) * mm, "end": v(14.74, -0.01) * mm});
            skLineSegment(sketch, "E35.0.10.0", {"start": v(20.32, 20.61) * mm, "end": v(23.2, 20.61) * mm});
            skLineSegment(sketch, "E35.3.10.0", {"start": v(18.88, 18.11) * mm, "end": v(20.32, 20.61) * mm});
            skLineSegment(sketch, "E35.6.10.0", {"start": v(20.32, 15.61) * mm, "end": v(18.88, 18.11) * mm});
            skLineSegment(sketch, "E35.9.10.0", {"start": v(23.2, 15.61) * mm, "end": v(20.32, 15.61) * mm});
            skLineSegment(sketch, "E35.12.10.0", {"start": v(24.65, 18.11) * mm, "end": v(23.2, 15.61) * mm});
            skLineSegment(sketch, "E35.15.10.0", {"start": v(23.2, 20.61) * mm, "end": v(24.65, 18.11) * mm});
            skLineSegment(sketch, "E35.18.10.0", {"start": v(25.73, 18.74) * mm, "end": v(24.3, 21.24) * mm});
            skLineSegment(sketch, "E35.21.10.0", {"start": v(24.3, 21.24) * mm, "end": v(25.73, 23.74) * mm});
            skLineSegment(sketch, "E35.24.10.0", {"start": v(25.73, 23.74) * mm, "end": v(28.62, 23.74) * mm});
            skLineSegment(sketch, "E35.27.10.0", {"start": v(28.62, 23.74) * mm, "end": v(30.07, 21.24) * mm});
            skLineSegment(sketch, "E35.30.10.0", {"start": v(30.07, 21.24) * mm, "end": v(28.62, 18.74) * mm});
            skLineSegment(sketch, "E35.33.10.0", {"start": v(28.62, 18.74) * mm, "end": v(25.73, 18.74) * mm});
            skLineSegment(sketch, "E35.0.10.1", {"start": v(20.32, 14.36) * mm, "end": v(23.2, 14.36) * mm});
            skLineSegment(sketch, "E35.3.10.1", {"start": v(18.88, 11.86) * mm, "end": v(20.32, 14.36) * mm});
            skLineSegment(sketch, "E35.6.10.1", {"start": v(20.32, 9.36) * mm, "end": v(18.88, 11.86) * mm});
            skLineSegment(sketch, "E35.9.10.1", {"start": v(23.2, 9.36) * mm, "end": v(20.32, 9.36) * mm});
            skLineSegment(sketch, "E35.12.10.1", {"start": v(24.65, 11.86) * mm, "end": v(23.2, 9.36) * mm});
            skLineSegment(sketch, "E35.15.10.1", {"start": v(23.2, 14.36) * mm, "end": v(24.65, 11.86) * mm});
            skLineSegment(sketch, "E35.18.10.1", {"start": v(25.73, 12.49) * mm, "end": v(24.3, 14.99) * mm});
            skLineSegment(sketch, "E35.21.10.1", {"start": v(24.3, 14.99) * mm, "end": v(25.73, 17.49) * mm});
            skLineSegment(sketch, "E35.24.10.1", {"start": v(25.73, 17.49) * mm, "end": v(28.62, 17.49) * mm});
            skLineSegment(sketch, "E35.27.10.1", {"start": v(28.62, 17.49) * mm, "end": v(30.07, 14.99) * mm});
            skLineSegment(sketch, "E35.30.10.1", {"start": v(30.07, 14.99) * mm, "end": v(28.62, 12.49) * mm});
            skLineSegment(sketch, "E35.33.10.1", {"start": v(28.62, 12.49) * mm, "end": v(25.73, 12.49) * mm});
            skLineSegment(sketch, "E35.0.10.2", {"start": v(20.32, 8.11) * mm, "end": v(23.2, 8.11) * mm});
            skLineSegment(sketch, "E35.3.10.2", {"start": v(18.88, 5.61) * mm, "end": v(20.32, 8.11) * mm});
            skLineSegment(sketch, "E35.6.10.2", {"start": v(20.32, 3.11) * mm, "end": v(18.88, 5.61) * mm});
            skLineSegment(sketch, "E35.9.10.2", {"start": v(23.2, 3.11) * mm, "end": v(20.32, 3.11) * mm});
            skLineSegment(sketch, "E35.12.10.2", {"start": v(24.65, 5.61) * mm, "end": v(23.2, 3.11) * mm});
            skLineSegment(sketch, "E35.15.10.2", {"start": v(23.2, 8.11) * mm, "end": v(24.65, 5.61) * mm});
            skLineSegment(sketch, "E35.18.10.2", {"start": v(25.73, 6.24) * mm, "end": v(24.3, 8.74) * mm});
            skLineSegment(sketch, "E35.21.10.2", {"start": v(24.3, 8.74) * mm, "end": v(25.73, 11.24) * mm});
            skLineSegment(sketch, "E35.24.10.2", {"start": v(25.73, 11.24) * mm, "end": v(28.62, 11.24) * mm});
            skLineSegment(sketch, "E35.27.10.2", {"start": v(28.62, 11.24) * mm, "end": v(30.07, 8.74) * mm});
            skLineSegment(sketch, "E35.30.10.2", {"start": v(30.07, 8.74) * mm, "end": v(28.62, 6.24) * mm});
            skLineSegment(sketch, "E35.33.10.2", {"start": v(28.62, 6.24) * mm, "end": v(25.73, 6.24) * mm});
            skLineSegment(sketch, "E35.0.10.3", {"start": v(20.32, 1.86) * mm, "end": v(23.2, 1.86) * mm});
            skLineSegment(sketch, "E35.3.10.3", {"start": v(18.88, -0.64) * mm, "end": v(20.32, 1.86) * mm});
            skLineSegment(sketch, "E35.6.10.3", {"start": v(20.32, -3.14) * mm, "end": v(18.88, -0.64) * mm});
            skLineSegment(sketch, "E35.9.10.3", {"start": v(23.2, -3.14) * mm, "end": v(20.32, -3.14) * mm});
            skLineSegment(sketch, "E35.12.10.3", {"start": v(24.65, -0.64) * mm, "end": v(23.2, -3.14) * mm});
            skLineSegment(sketch, "E35.15.10.3", {"start": v(23.2, 1.86) * mm, "end": v(24.65, -0.64) * mm});
            skLineSegment(sketch, "E35.18.10.3", {"start": v(25.73, -0.01) * mm, "end": v(24.3, 2.49) * mm});
            skLineSegment(sketch, "E35.21.10.3", {"start": v(24.3, 2.49) * mm, "end": v(25.73, 4.99) * mm});
            skLineSegment(sketch, "E35.24.10.3", {"start": v(25.73, 4.99) * mm, "end": v(28.62, 4.99) * mm});
            skLineSegment(sketch, "E35.27.10.3", {"start": v(28.62, 4.99) * mm, "end": v(30.07, 2.49) * mm});
            skLineSegment(sketch, "E35.30.10.3", {"start": v(30.07, 2.49) * mm, "end": v(28.62, -0.01) * mm});
            skLineSegment(sketch, "E35.33.10.3", {"start": v(28.62, -0.01) * mm, "end": v(25.73, -0.01) * mm});
            skLineSegment(sketch, "E35.0.11.0", {"start": v(31.32, 20.61) * mm, "end": v(34.2, 20.61) * mm});
            skLineSegment(sketch, "E35.3.11.0", {"start": v(29.87, 18.11) * mm, "end": v(31.32, 20.61) * mm});
            skLineSegment(sketch, "E35.6.11.0", {"start": v(31.32, 15.61) * mm, "end": v(29.87, 18.11) * mm});
            skLineSegment(sketch, "E35.9.11.0", {"start": v(34.2, 15.61) * mm, "end": v(31.32, 15.61) * mm});
            skLineSegment(sketch, "E35.12.11.0", {"start": v(35.65, 18.11) * mm, "end": v(34.2, 15.61) * mm});
            skLineSegment(sketch, "E35.15.11.0", {"start": v(34.2, 20.61) * mm, "end": v(35.65, 18.11) * mm});
            skLineSegment(sketch, "E35.18.11.0", {"start": v(36.73, 18.74) * mm, "end": v(35.28, 21.24) * mm});
            skLineSegment(sketch, "E35.21.11.0", {"start": v(35.28, 21.24) * mm, "end": v(36.73, 23.74) * mm});
            skLineSegment(sketch, "E35.24.11.0", {"start": v(36.73, 23.74) * mm, "end": v(39.61, 23.74) * mm});
            skLineSegment(sketch, "E35.27.11.0", {"start": v(39.61, 23.74) * mm, "end": v(41.06, 21.24) * mm});
            skLineSegment(sketch, "E35.30.11.0", {"start": v(41.06, 21.24) * mm, "end": v(39.61, 18.74) * mm});
            skLineSegment(sketch, "E35.33.11.0", {"start": v(39.61, 18.74) * mm, "end": v(36.73, 18.74) * mm});
            skLineSegment(sketch, "E35.0.11.1", {"start": v(31.32, 14.36) * mm, "end": v(34.2, 14.36) * mm});
            skLineSegment(sketch, "E35.3.11.1", {"start": v(29.87, 11.86) * mm, "end": v(31.32, 14.36) * mm});
            skLineSegment(sketch, "E35.6.11.1", {"start": v(31.32, 9.36) * mm, "end": v(29.87, 11.86) * mm});
            skLineSegment(sketch, "E35.9.11.1", {"start": v(34.2, 9.36) * mm, "end": v(31.32, 9.36) * mm});
            skLineSegment(sketch, "E35.12.11.1", {"start": v(35.65, 11.86) * mm, "end": v(34.2, 9.36) * mm});
            skLineSegment(sketch, "E35.15.11.1", {"start": v(34.2, 14.36) * mm, "end": v(35.65, 11.86) * mm});
            skLineSegment(sketch, "E35.18.11.1", {"start": v(36.73, 12.49) * mm, "end": v(35.28, 14.99) * mm});
            skLineSegment(sketch, "E35.21.11.1", {"start": v(35.28, 14.99) * mm, "end": v(36.73, 17.49) * mm});
            skLineSegment(sketch, "E35.24.11.1", {"start": v(36.73, 17.49) * mm, "end": v(39.61, 17.49) * mm});
            skLineSegment(sketch, "E35.27.11.1", {"start": v(39.61, 17.49) * mm, "end": v(41.06, 14.99) * mm});
            skLineSegment(sketch, "E35.30.11.1", {"start": v(41.06, 14.99) * mm, "end": v(39.61, 12.49) * mm});
            skLineSegment(sketch, "E35.33.11.1", {"start": v(39.61, 12.49) * mm, "end": v(36.73, 12.49) * mm});
            skLineSegment(sketch, "E35.0.11.2", {"start": v(31.32, 8.11) * mm, "end": v(34.2, 8.11) * mm});
            skLineSegment(sketch, "E35.3.11.2", {"start": v(29.87, 5.61) * mm, "end": v(31.32, 8.11) * mm});
            skLineSegment(sketch, "E35.6.11.2", {"start": v(31.32, 3.11) * mm, "end": v(29.87, 5.61) * mm});
            skLineSegment(sketch, "E35.9.11.2", {"start": v(34.2, 3.11) * mm, "end": v(31.32, 3.11) * mm});
            skLineSegment(sketch, "E35.12.11.2", {"start": v(35.65, 5.61) * mm, "end": v(34.2, 3.11) * mm});
            skLineSegment(sketch, "E35.15.11.2", {"start": v(34.2, 8.11) * mm, "end": v(35.65, 5.61) * mm});
            skLineSegment(sketch, "E35.18.11.2", {"start": v(36.73, 6.24) * mm, "end": v(35.28, 8.74) * mm});
            skLineSegment(sketch, "E35.21.11.2", {"start": v(35.28, 8.74) * mm, "end": v(36.73, 11.24) * mm});
            skLineSegment(sketch, "E35.24.11.2", {"start": v(36.73, 11.24) * mm, "end": v(39.61, 11.24) * mm});
            skLineSegment(sketch, "E35.27.11.2", {"start": v(39.61, 11.24) * mm, "end": v(41.06, 8.74) * mm});
            skLineSegment(sketch, "E35.30.11.2", {"start": v(41.06, 8.74) * mm, "end": v(39.61, 6.24) * mm});
            skLineSegment(sketch, "E35.33.11.2", {"start": v(39.61, 6.24) * mm, "end": v(36.73, 6.24) * mm});
            skLineSegment(sketch, "E35.0.11.3", {"start": v(31.32, 1.86) * mm, "end": v(34.2, 1.86) * mm});
            skLineSegment(sketch, "E35.3.11.3", {"start": v(29.87, -0.64) * mm, "end": v(31.32, 1.86) * mm});
            skLineSegment(sketch, "E35.6.11.3", {"start": v(31.32, -3.14) * mm, "end": v(29.87, -0.64) * mm});
            skLineSegment(sketch, "E35.9.11.3", {"start": v(34.2, -3.14) * mm, "end": v(31.32, -3.14) * mm});
            skLineSegment(sketch, "E35.12.11.3", {"start": v(35.65, -0.64) * mm, "end": v(34.2, -3.14) * mm});
            skLineSegment(sketch, "E35.15.11.3", {"start": v(34.2, 1.86) * mm, "end": v(35.65, -0.64) * mm});
            skLineSegment(sketch, "E35.18.11.3", {"start": v(36.73, -0.01) * mm, "end": v(35.28, 2.49) * mm});
            skLineSegment(sketch, "E35.21.11.3", {"start": v(35.28, 2.49) * mm, "end": v(36.73, 4.99) * mm});
            skLineSegment(sketch, "E35.24.11.3", {"start": v(36.73, 4.99) * mm, "end": v(39.61, 4.99) * mm});
            skLineSegment(sketch, "E35.27.11.3", {"start": v(39.61, 4.99) * mm, "end": v(41.06, 2.49) * mm});
            skLineSegment(sketch, "E35.30.11.3", {"start": v(41.06, 2.49) * mm, "end": v(39.61, -0.01) * mm});
            skLineSegment(sketch, "E35.33.11.3", {"start": v(39.61, -0.01) * mm, "end": v(36.73, -0.01) * mm});
            skLineSegment(sketch, "E35.0.12.0", {"start": v(42.3, 20.61) * mm, "end": v(45.2, 20.61) * mm});
            skLineSegment(sketch, "E35.3.12.0", {"start": v(40.86, 18.11) * mm, "end": v(42.3, 20.61) * mm});
            skLineSegment(sketch, "E35.6.12.0", {"start": v(42.3, 15.61) * mm, "end": v(40.86, 18.11) * mm});
            skLineSegment(sketch, "E35.9.12.0", {"start": v(45.2, 15.61) * mm, "end": v(42.3, 15.61) * mm});
            skLineSegment(sketch, "E35.12.12.0", {"start": v(46.64, 18.11) * mm, "end": v(45.2, 15.61) * mm});
            skLineSegment(sketch, "E35.15.12.0", {"start": v(45.2, 20.61) * mm, "end": v(46.64, 18.11) * mm});
            skLineSegment(sketch, "E35.18.12.0", {"start": v(47.72, 18.74) * mm, "end": v(46.28, 21.24) * mm});
            skLineSegment(sketch, "E35.21.12.0", {"start": v(46.28, 21.24) * mm, "end": v(47.72, 23.74) * mm});
            skLineSegment(sketch, "E35.24.12.0", {"start": v(47.72, 23.74) * mm, "end": v(50.6, 23.74) * mm});
            skLineSegment(sketch, "E35.27.12.0", {"start": v(50.6, 23.74) * mm, "end": v(52.05, 21.24) * mm});
            skLineSegment(sketch, "E35.30.12.0", {"start": v(52.05, 21.24) * mm, "end": v(50.6, 18.74) * mm});
            skLineSegment(sketch, "E35.33.12.0", {"start": v(50.6, 18.74) * mm, "end": v(47.72, 18.74) * mm});
            skLineSegment(sketch, "E35.0.12.1", {"start": v(42.3, 14.36) * mm, "end": v(45.2, 14.36) * mm});
            skLineSegment(sketch, "E35.3.12.1", {"start": v(40.86, 11.86) * mm, "end": v(42.3, 14.36) * mm});
            skLineSegment(sketch, "E35.6.12.1", {"start": v(42.3, 9.36) * mm, "end": v(40.86, 11.86) * mm});
            skLineSegment(sketch, "E35.9.12.1", {"start": v(45.2, 9.36) * mm, "end": v(42.3, 9.36) * mm});
            skLineSegment(sketch, "E35.12.12.1", {"start": v(46.64, 11.86) * mm, "end": v(45.2, 9.36) * mm});
            skLineSegment(sketch, "E35.15.12.1", {"start": v(45.2, 14.36) * mm, "end": v(46.64, 11.86) * mm});
            skLineSegment(sketch, "E35.18.12.1", {"start": v(47.72, 12.49) * mm, "end": v(46.28, 14.99) * mm});
            skLineSegment(sketch, "E35.21.12.1", {"start": v(46.28, 14.99) * mm, "end": v(47.72, 17.49) * mm});
            skLineSegment(sketch, "E35.24.12.1", {"start": v(47.72, 17.49) * mm, "end": v(50.6, 17.49) * mm});
            skLineSegment(sketch, "E35.27.12.1", {"start": v(50.6, 17.49) * mm, "end": v(52.05, 14.99) * mm});
            skLineSegment(sketch, "E35.30.12.1", {"start": v(52.05, 14.99) * mm, "end": v(50.6, 12.49) * mm});
            skLineSegment(sketch, "E35.33.12.1", {"start": v(50.6, 12.49) * mm, "end": v(47.72, 12.49) * mm});
            skLineSegment(sketch, "E35.0.12.2", {"start": v(42.3, 8.11) * mm, "end": v(45.2, 8.11) * mm});
            skLineSegment(sketch, "E35.3.12.2", {"start": v(40.86, 5.61) * mm, "end": v(42.3, 8.11) * mm});
            skLineSegment(sketch, "E35.6.12.2", {"start": v(42.3, 3.11) * mm, "end": v(40.86, 5.61) * mm});
            skLineSegment(sketch, "E35.9.12.2", {"start": v(45.2, 3.11) * mm, "end": v(42.3, 3.11) * mm});
            skLineSegment(sketch, "E35.12.12.2", {"start": v(46.64, 5.61) * mm, "end": v(45.2, 3.11) * mm});
            skLineSegment(sketch, "E35.15.12.2", {"start": v(45.2, 8.11) * mm, "end": v(46.64, 5.61) * mm});
            skLineSegment(sketch, "E35.18.12.2", {"start": v(47.72, 6.24) * mm, "end": v(46.28, 8.74) * mm});
            skLineSegment(sketch, "E35.21.12.2", {"start": v(46.28, 8.74) * mm, "end": v(47.72, 11.24) * mm});
            skLineSegment(sketch, "E35.24.12.2", {"start": v(47.72, 11.24) * mm, "end": v(50.6, 11.24) * mm});
            skLineSegment(sketch, "E35.27.12.2", {"start": v(50.6, 11.24) * mm, "end": v(52.05, 8.74) * mm});
            skLineSegment(sketch, "E35.30.12.2", {"start": v(52.05, 8.74) * mm, "end": v(50.6, 6.24) * mm});
            skLineSegment(sketch, "E35.33.12.2", {"start": v(50.6, 6.24) * mm, "end": v(47.72, 6.24) * mm});
            skLineSegment(sketch, "E35.0.12.3", {"start": v(42.3, 1.86) * mm, "end": v(45.2, 1.86) * mm});
            skLineSegment(sketch, "E35.3.12.3", {"start": v(40.86, -0.64) * mm, "end": v(42.3, 1.86) * mm});
            skLineSegment(sketch, "E35.6.12.3", {"start": v(42.3, -3.14) * mm, "end": v(40.86, -0.64) * mm});
            skLineSegment(sketch, "E35.9.12.3", {"start": v(45.2, -3.14) * mm, "end": v(42.3, -3.14) * mm});
            skLineSegment(sketch, "E35.12.12.3", {"start": v(46.64, -0.64) * mm, "end": v(45.2, -3.14) * mm});
            skLineSegment(sketch, "E35.15.12.3", {"start": v(45.2, 1.86) * mm, "end": v(46.64, -0.64) * mm});
            skLineSegment(sketch, "E35.18.12.3", {"start": v(47.72, -0.01) * mm, "end": v(46.28, 2.49) * mm});
            skLineSegment(sketch, "E35.21.12.3", {"start": v(46.28, 2.49) * mm, "end": v(47.72, 4.99) * mm});
            skLineSegment(sketch, "E35.24.12.3", {"start": v(47.72, 4.99) * mm, "end": v(50.6, 4.99) * mm});
            skLineSegment(sketch, "E35.27.12.3", {"start": v(50.6, 4.99) * mm, "end": v(52.05, 2.49) * mm});
            skLineSegment(sketch, "E35.30.12.3", {"start": v(52.05, 2.49) * mm, "end": v(50.6, -0.01) * mm});
            skLineSegment(sketch, "E35.33.12.3", {"start": v(50.6, -0.01) * mm, "end": v(47.72, -0.01) * mm});
            skSolve(sketch);
        }
        {
            var Q0;
            {var subQ0=sQuery(id+"F6.wireOp",EDGE,"E30.0");Q0=makeQuery(id+"F6.imprint","IMPRINT",FACE,{"disambiguationData":[TD([[makeQuery(id+"F6.imprint","IMPRINT",EDGE,{"derivedFrom":subQ0}),-1.0]])]});}
            var Q1;
            {var subQ5=sQuery(id+"F6.wireOp",EDGE,"E31.0.1.0");Q1=makeQuery(id+"F6.imprint","IMPRINT",FACE,{"disambiguationData":[TD([[makeQuery(id+"F6.imprint","IMPRINT",EDGE,{"derivedFrom":subQ5}),-1.0]])]});}
            var Q2;
            {var subQ0=sQuery(id+"F6.wireOp",EDGE,"E32.0.0.2");Q2=makeQuery(id+"F6.imprint","IMPRINT",FACE,{"disambiguationData":[TD([[makeQuery(id+"F6.imprint","IMPRINT",EDGE,{"derivedFrom":subQ0}),-1.0]])]});}
            var Q3;
            Q3=makeQuery(id+"F6.imprint","IMPRINT",FACE,{"disambiguationData":[TD([[makeQuery(id+"F6.imprint","IMPRINT",EDGE,{"derivedFrom":sQuery(id+"F6.wireOp",EDGE,"E31.0.1.6")}),-1.0]])]});
            var Q4;
            Q4=makeQuery(id+"F6.imprint","IMPRINT",FACE,{"disambiguationData":[TD([[makeQuery(id+"F6.imprint","IMPRINT",EDGE,{"derivedFrom":sQuery(id+"F6.wireOp",EDGE,"E32.18.0.2")}),-1.0]])]});
            var Q5;
            {var subQ5=sQuery(id+"F6.wireOp",EDGE,"E33.24.0.3");Q5=makeQuery(id+"F6.imprint","IMPRINT",FACE,{"disambiguationData":[TD([[makeQuery(id+"F6.imprint","IMPRINT",EDGE,{"derivedFrom":subQ5}),-1.0]])]});}
            var Q6;
            {var subQ0=sQuery(id+"F6.wireOp",EDGE,"E31.1.0.2");Q6=makeQuery(id+"F6.imprint","IMPRINT",FACE,{"disambiguationData":[TD([[makeQuery(id+"F6.imprint","IMPRINT",EDGE,{"derivedFrom":subQ0}),-1.0]])]});}
            var Q7;
            Q7=makeQuery(id+"F6.imprint","IMPRINT",FACE,{"disambiguationData":[TD([[makeQuery(id+"F6.imprint","IMPRINT",EDGE,{"derivedFrom":sQuery(id+"F6.wireOp",EDGE,"E31.1.1.0")}),-1.0]])]});
            var Q8;
            Q8=makeQuery(id+"F6.imprint","IMPRINT",FACE,{"disambiguationData":[TD([[makeQuery(id+"F6.imprint","IMPRINT",EDGE,{"derivedFrom":sQuery(id+"F6.wireOp",EDGE,"E32.0.1.2")}),-1.0]])]});
            var Q9;
            Q9=makeQuery(id+"F6.imprint","IMPRINT",FACE,{"disambiguationData":[TD([[makeQuery(id+"F6.imprint","IMPRINT",EDGE,{"derivedFrom":sQuery(id+"F6.wireOp",EDGE,"E31.1.1.6")}),-1.0]])]});
            var Q10;
            Q10=makeQuery(id+"F6.imprint","IMPRINT",FACE,{"disambiguationData":[TD([[makeQuery(id+"F6.imprint","IMPRINT",EDGE,{"derivedFrom":sQuery(id+"F6.wireOp",EDGE,"E32.18.1.2")}),-1.0]])]});
            var Q11;
            {var subQ5=sQuery(id+"F6.wireOp",EDGE,"E33.24.1.3");Q11=makeQuery(id+"F6.imprint","IMPRINT",FACE,{"disambiguationData":[TD([[makeQuery(id+"F6.imprint","IMPRINT",EDGE,{"derivedFrom":subQ5}),-1.0]])]});}
            var Q12;
            {var subQ5=sQuery(id+"F6.wireOp",EDGE,"E31.2.0.2");Q12=makeQuery(id+"F6.imprint","IMPRINT",FACE,{"disambiguationData":[TD([[makeQuery(id+"F6.imprint","IMPRINT",EDGE,{"derivedFrom":subQ5}),-1.0]])]});}
            var Q13;
            Q13=makeQuery(id+"F6.imprint","IMPRINT",FACE,{"disambiguationData":[TD([[makeQuery(id+"F6.imprint","IMPRINT",EDGE,{"derivedFrom":sQuery(id+"F6.wireOp",EDGE,"E31.2.1.0")}),-1.0]])]});
            var Q14;
            Q14=makeQuery(id+"F6.imprint","IMPRINT",FACE,{"disambiguationData":[TD([[makeQuery(id+"F6.imprint","IMPRINT",EDGE,{"derivedFrom":sQuery(id+"F6.wireOp",EDGE,"E32.0.2.2")}),-1.0]])]});
            var Q15;
            Q15=makeQuery(id+"F6.imprint","IMPRINT",FACE,{"disambiguationData":[TD([[makeQuery(id+"F6.imprint","IMPRINT",EDGE,{"derivedFrom":sQuery(id+"F6.wireOp",EDGE,"E31.2.1.6")}),-1.0]])]});
            var Q16;
            Q16=makeQuery(id+"F6.imprint","IMPRINT",FACE,{"disambiguationData":[TD([[makeQuery(id+"F6.imprint","IMPRINT",EDGE,{"derivedFrom":sQuery(id+"F6.wireOp",EDGE,"E32.18.2.2")}),-1.0]])]});
            var Q17;
            {var subQ5=sQuery(id+"F6.wireOp",EDGE,"E33.24.2.3");Q17=makeQuery(id+"F6.imprint","IMPRINT",FACE,{"disambiguationData":[TD([[makeQuery(id+"F6.imprint","IMPRINT",EDGE,{"derivedFrom":subQ5}),-1.0]])]});}
            var Q18;
            {var subQ0=sQuery(id+"F6.wireOp",EDGE,"E34.6.3.0");Q18=makeQuery(id+"F6.imprint","IMPRINT",FACE,{"disambiguationData":[TD([[makeQuery(id+"F6.imprint","IMPRINT",EDGE,{"derivedFrom":subQ0}),-1.0]])]});}
            var Q19;
            Q19=makeQuery(id+"F6.imprint","IMPRINT",FACE,{"disambiguationData":[TD([[makeQuery(id+"F6.imprint","IMPRINT",EDGE,{"derivedFrom":sQuery(id+"F6.wireOp",EDGE,"E34.0.3.1")}),-1.0]])]});
            var Q20;
            Q20=makeQuery(id+"F6.imprint","IMPRINT",FACE,{"disambiguationData":[TD([[makeQuery(id+"F6.imprint","IMPRINT",EDGE,{"derivedFrom":sQuery(id+"F6.wireOp",EDGE,"E34.0.3.2")}),-1.0]])]});
            var Q21;
            Q21=makeQuery(id+"F6.imprint","IMPRINT",FACE,{"disambiguationData":[TD([[makeQuery(id+"F6.imprint","IMPRINT",EDGE,{"derivedFrom":sQuery(id+"F6.wireOp",EDGE,"E34.18.3.1")}),-1.0]])]});
            var Q22;
            Q22=makeQuery(id+"F6.imprint","IMPRINT",FACE,{"disambiguationData":[TD([[makeQuery(id+"F6.imprint","IMPRINT",EDGE,{"derivedFrom":sQuery(id+"F6.wireOp",EDGE,"E34.18.3.2")}),-1.0]])]});
            var Q23;
            {var subQ5=sQuery(id+"F6.wireOp",EDGE,"E34.24.3.3");Q23=makeQuery(id+"F6.imprint","IMPRINT",FACE,{"disambiguationData":[TD([[makeQuery(id+"F6.imprint","IMPRINT",EDGE,{"derivedFrom":subQ5}),-1.0]])]});}
            var Q24;
            {var subQ0=sQuery(id+"F6.wireOp",EDGE,"E34.6.4.0");Q24=makeQuery(id+"F6.imprint","IMPRINT",FACE,{"disambiguationData":[TD([[makeQuery(id+"F6.imprint","IMPRINT",EDGE,{"derivedFrom":subQ0}),-1.0]])]});}
            var Q25;
            Q25=makeQuery(id+"F6.imprint","IMPRINT",FACE,{"disambiguationData":[TD([[makeQuery(id+"F6.imprint","IMPRINT",EDGE,{"derivedFrom":sQuery(id+"F6.wireOp",EDGE,"E34.0.4.1")}),-1.0]])]});
            var Q26;
            Q26=makeQuery(id+"F6.imprint","IMPRINT",FACE,{"disambiguationData":[TD([[makeQuery(id+"F6.imprint","IMPRINT",EDGE,{"derivedFrom":sQuery(id+"F6.wireOp",EDGE,"E34.0.4.2")}),-1.0]])]});
            var Q27;
            Q27=makeQuery(id+"F6.imprint","IMPRINT",FACE,{"disambiguationData":[TD([[makeQuery(id+"F6.imprint","IMPRINT",EDGE,{"derivedFrom":sQuery(id+"F6.wireOp",EDGE,"E34.18.4.1")}),-1.0]])]});
            var Q28;
            Q28=makeQuery(id+"F6.imprint","IMPRINT",FACE,{"disambiguationData":[TD([[makeQuery(id+"F6.imprint","IMPRINT",EDGE,{"derivedFrom":sQuery(id+"F6.wireOp",EDGE,"E34.18.4.2")}),-1.0]])]});
            var Q29;
            {var subQ5=sQuery(id+"F6.wireOp",EDGE,"E34.24.4.3");Q29=makeQuery(id+"F6.imprint","IMPRINT",FACE,{"disambiguationData":[TD([[makeQuery(id+"F6.imprint","IMPRINT",EDGE,{"derivedFrom":subQ5}),-1.0]])]});}
            var Q30;
            {var subQ0=sQuery(id+"F6.wireOp",EDGE,"E34.6.5.0");Q30=makeQuery(id+"F6.imprint","IMPRINT",FACE,{"disambiguationData":[TD([[makeQuery(id+"F6.imprint","IMPRINT",EDGE,{"derivedFrom":subQ0}),-1.0]])]});}
            var Q31;
            Q31=makeQuery(id+"F6.imprint","IMPRINT",FACE,{"disambiguationData":[TD([[makeQuery(id+"F6.imprint","IMPRINT",EDGE,{"derivedFrom":sQuery(id+"F6.wireOp",EDGE,"E34.0.5.1")}),-1.0]])]});
            var Q32;
            Q32=makeQuery(id+"F6.imprint","IMPRINT",FACE,{"disambiguationData":[TD([[makeQuery(id+"F6.imprint","IMPRINT",EDGE,{"derivedFrom":sQuery(id+"F6.wireOp",EDGE,"E34.0.5.2")}),-1.0]])]});
            var Q33;
            Q33=makeQuery(id+"F6.imprint","IMPRINT",FACE,{"disambiguationData":[TD([[makeQuery(id+"F6.imprint","IMPRINT",EDGE,{"derivedFrom":sQuery(id+"F6.wireOp",EDGE,"E34.18.5.1")}),-1.0]])]});
            var Q34;
            Q34=makeQuery(id+"F6.imprint","IMPRINT",FACE,{"disambiguationData":[TD([[makeQuery(id+"F6.imprint","IMPRINT",EDGE,{"derivedFrom":sQuery(id+"F6.wireOp",EDGE,"E34.18.5.2")}),-1.0]])]});
            var Q35;
            {var subQ5=sQuery(id+"F6.wireOp",EDGE,"E34.24.5.3");Q35=makeQuery(id+"F6.imprint","IMPRINT",FACE,{"disambiguationData":[TD([[makeQuery(id+"F6.imprint","IMPRINT",EDGE,{"derivedFrom":subQ5}),-1.0]])]});}
            var Q36;
            {var subQ0=sQuery(id+"F6.wireOp",EDGE,"E34.6.6.0");Q36=makeQuery(id+"F6.imprint","IMPRINT",FACE,{"disambiguationData":[TD([[makeQuery(id+"F6.imprint","IMPRINT",EDGE,{"derivedFrom":subQ0}),-1.0]])]});}
            var Q37;
            Q37=makeQuery(id+"F6.imprint","IMPRINT",FACE,{"disambiguationData":[TD([[makeQuery(id+"F6.imprint","IMPRINT",EDGE,{"derivedFrom":sQuery(id+"F6.wireOp",EDGE,"E34.0.6.1")}),-1.0]])]});
            var Q38;
            Q38=makeQuery(id+"F6.imprint","IMPRINT",FACE,{"disambiguationData":[TD([[makeQuery(id+"F6.imprint","IMPRINT",EDGE,{"derivedFrom":sQuery(id+"F6.wireOp",EDGE,"E34.0.6.2")}),-1.0]])]});
            var Q39;
            Q39=makeQuery(id+"F6.imprint","IMPRINT",FACE,{"disambiguationData":[TD([[makeQuery(id+"F6.imprint","IMPRINT",EDGE,{"derivedFrom":sQuery(id+"F6.wireOp",EDGE,"E34.18.6.1")}),-1.0]])]});
            var Q40;
            Q40=makeQuery(id+"F6.imprint","IMPRINT",FACE,{"disambiguationData":[TD([[makeQuery(id+"F6.imprint","IMPRINT",EDGE,{"derivedFrom":sQuery(id+"F6.wireOp",EDGE,"E34.18.6.2")}),-1.0]])]});
            var Q41;
            {var subQ5=sQuery(id+"F6.wireOp",EDGE,"E34.24.6.3");Q41=makeQuery(id+"F6.imprint","IMPRINT",FACE,{"disambiguationData":[TD([[makeQuery(id+"F6.imprint","IMPRINT",EDGE,{"derivedFrom":subQ5}),-1.0]])]});}
            var Q42;
            {var subQ0=sQuery(id+"F6.wireOp",EDGE,"E34.6.7.0");Q42=makeQuery(id+"F6.imprint","IMPRINT",FACE,{"disambiguationData":[TD([[makeQuery(id+"F6.imprint","IMPRINT",EDGE,{"derivedFrom":subQ0}),-1.0]])]});}
            var Q43;
            Q43=makeQuery(id+"F6.imprint","IMPRINT",FACE,{"disambiguationData":[TD([[makeQuery(id+"F6.imprint","IMPRINT",EDGE,{"derivedFrom":sQuery(id+"F6.wireOp",EDGE,"E34.0.7.1")}),-1.0]])]});
            var Q44;
            Q44=makeQuery(id+"F6.imprint","IMPRINT",FACE,{"disambiguationData":[TD([[makeQuery(id+"F6.imprint","IMPRINT",EDGE,{"derivedFrom":sQuery(id+"F6.wireOp",EDGE,"E34.0.7.2")}),-1.0]])]});
            var Q45;
            Q45=makeQuery(id+"F6.imprint","IMPRINT",FACE,{"disambiguationData":[TD([[makeQuery(id+"F6.imprint","IMPRINT",EDGE,{"derivedFrom":sQuery(id+"F6.wireOp",EDGE,"E34.18.7.1")}),-1.0]])]});
            var Q46;
            Q46=makeQuery(id+"F6.imprint","IMPRINT",FACE,{"disambiguationData":[TD([[makeQuery(id+"F6.imprint","IMPRINT",EDGE,{"derivedFrom":sQuery(id+"F6.wireOp",EDGE,"E34.18.7.2")}),-1.0]])]});
            var Q47;
            {var subQ5=sQuery(id+"F6.wireOp",EDGE,"E34.24.7.3");Q47=makeQuery(id+"F6.imprint","IMPRINT",FACE,{"disambiguationData":[TD([[makeQuery(id+"F6.imprint","IMPRINT",EDGE,{"derivedFrom":subQ5}),-1.0]])]});}
            var Q48;
            {var subQ0=sQuery(id+"F6.wireOp",EDGE,"E34.6.8.0");Q48=makeQuery(id+"F6.imprint","IMPRINT",FACE,{"disambiguationData":[TD([[makeQuery(id+"F6.imprint","IMPRINT",EDGE,{"derivedFrom":subQ0}),-1.0]])]});}
            var Q49;
            Q49=makeQuery(id+"F6.imprint","IMPRINT",FACE,{"disambiguationData":[TD([[makeQuery(id+"F6.imprint","IMPRINT",EDGE,{"derivedFrom":sQuery(id+"F6.wireOp",EDGE,"E34.0.8.1")}),-1.0]])]});
            var Q50;
            Q50=makeQuery(id+"F6.imprint","IMPRINT",FACE,{"disambiguationData":[TD([[makeQuery(id+"F6.imprint","IMPRINT",EDGE,{"derivedFrom":sQuery(id+"F6.wireOp",EDGE,"E34.0.8.2")}),-1.0]])]});
            var Q51;
            Q51=makeQuery(id+"F6.imprint","IMPRINT",FACE,{"disambiguationData":[TD([[makeQuery(id+"F6.imprint","IMPRINT",EDGE,{"derivedFrom":sQuery(id+"F6.wireOp",EDGE,"E34.18.8.1")}),-1.0]])]});
            var Q52;
            Q52=makeQuery(id+"F6.imprint","IMPRINT",FACE,{"disambiguationData":[TD([[makeQuery(id+"F6.imprint","IMPRINT",EDGE,{"derivedFrom":sQuery(id+"F6.wireOp",EDGE,"E34.18.8.2")}),-1.0]])]});
            var Q53;
            {var subQ5=sQuery(id+"F6.wireOp",EDGE,"E34.24.8.3");Q53=makeQuery(id+"F6.imprint","IMPRINT",FACE,{"disambiguationData":[TD([[makeQuery(id+"F6.imprint","IMPRINT",EDGE,{"derivedFrom":subQ5}),-1.0]])]});}
            var Q54;
            {var subQ0=sQuery(id+"F6.wireOp",EDGE,"E34.6.9.0");Q54=makeQuery(id+"F6.imprint","IMPRINT",FACE,{"disambiguationData":[TD([[makeQuery(id+"F6.imprint","IMPRINT",EDGE,{"derivedFrom":subQ0}),-1.0]])]});}
            var Q55;
            Q55=makeQuery(id+"F6.imprint","IMPRINT",FACE,{"disambiguationData":[TD([[makeQuery(id+"F6.imprint","IMPRINT",EDGE,{"derivedFrom":sQuery(id+"F6.wireOp",EDGE,"E34.0.9.1")}),-1.0]])]});
            var Q56;
            Q56=makeQuery(id+"F6.imprint","IMPRINT",FACE,{"disambiguationData":[TD([[makeQuery(id+"F6.imprint","IMPRINT",EDGE,{"derivedFrom":sQuery(id+"F6.wireOp",EDGE,"E34.0.9.2")}),-1.0]])]});
            var Q57;
            Q57=makeQuery(id+"F6.imprint","IMPRINT",FACE,{"disambiguationData":[TD([[makeQuery(id+"F6.imprint","IMPRINT",EDGE,{"derivedFrom":sQuery(id+"F6.wireOp",EDGE,"E34.18.9.1")}),-1.0]])]});
            var Q58;
            Q58=makeQuery(id+"F6.imprint","IMPRINT",FACE,{"disambiguationData":[TD([[makeQuery(id+"F6.imprint","IMPRINT",EDGE,{"derivedFrom":sQuery(id+"F6.wireOp",EDGE,"E34.18.9.2")}),-1.0]])]});
            var Q59;
            {var subQ5=sQuery(id+"F6.wireOp",EDGE,"E34.24.9.3");Q59=makeQuery(id+"F6.imprint","IMPRINT",FACE,{"disambiguationData":[TD([[makeQuery(id+"F6.imprint","IMPRINT",EDGE,{"derivedFrom":subQ5}),-1.0]])]});}
            var Q60;
            {var subQ0=sQuery(id+"F6.wireOp",EDGE,"E35.6.10.0");Q60=makeQuery(id+"F6.imprint","IMPRINT",FACE,{"disambiguationData":[TD([[makeQuery(id+"F6.imprint","IMPRINT",EDGE,{"derivedFrom":subQ0}),-1.0]])]});}
            var Q61;
            Q61=makeQuery(id+"F6.imprint","IMPRINT",FACE,{"disambiguationData":[TD([[makeQuery(id+"F6.imprint","IMPRINT",EDGE,{"derivedFrom":sQuery(id+"F6.wireOp",EDGE,"E35.0.10.1")}),-1.0]])]});
            var Q62;
            Q62=makeQuery(id+"F6.imprint","IMPRINT",FACE,{"disambiguationData":[TD([[makeQuery(id+"F6.imprint","IMPRINT",EDGE,{"derivedFrom":sQuery(id+"F6.wireOp",EDGE,"E35.0.10.2")}),-1.0]])]});
            var Q63;
            Q63=makeQuery(id+"F6.imprint","IMPRINT",FACE,{"disambiguationData":[TD([[makeQuery(id+"F6.imprint","IMPRINT",EDGE,{"derivedFrom":sQuery(id+"F6.wireOp",EDGE,"E35.18.10.1")}),-1.0]])]});
            var Q64;
            Q64=makeQuery(id+"F6.imprint","IMPRINT",FACE,{"disambiguationData":[TD([[makeQuery(id+"F6.imprint","IMPRINT",EDGE,{"derivedFrom":sQuery(id+"F6.wireOp",EDGE,"E35.18.10.2")}),-1.0]])]});
            var Q65;
            {var subQ5=sQuery(id+"F6.wireOp",EDGE,"E35.24.10.3");Q65=makeQuery(id+"F6.imprint","IMPRINT",FACE,{"disambiguationData":[TD([[makeQuery(id+"F6.imprint","IMPRINT",EDGE,{"derivedFrom":subQ5}),-1.0]])]});}
            var Q66;
            {var subQ0=sQuery(id+"F6.wireOp",EDGE,"E35.6.11.0");Q66=makeQuery(id+"F6.imprint","IMPRINT",FACE,{"disambiguationData":[TD([[makeQuery(id+"F6.imprint","IMPRINT",EDGE,{"derivedFrom":subQ0}),-1.0]])]});}
            var Q67;
            Q67=makeQuery(id+"F6.imprint","IMPRINT",FACE,{"disambiguationData":[TD([[makeQuery(id+"F6.imprint","IMPRINT",EDGE,{"derivedFrom":sQuery(id+"F6.wireOp",EDGE,"E35.0.11.1")}),-1.0]])]});
            var Q68;
            Q68=makeQuery(id+"F6.imprint","IMPRINT",FACE,{"disambiguationData":[TD([[makeQuery(id+"F6.imprint","IMPRINT",EDGE,{"derivedFrom":sQuery(id+"F6.wireOp",EDGE,"E35.0.11.2")}),-1.0]])]});
            var Q69;
            Q69=makeQuery(id+"F6.imprint","IMPRINT",FACE,{"disambiguationData":[TD([[makeQuery(id+"F6.imprint","IMPRINT",EDGE,{"derivedFrom":sQuery(id+"F6.wireOp",EDGE,"E35.18.11.1")}),-1.0]])]});
            var Q70;
            Q70=makeQuery(id+"F6.imprint","IMPRINT",FACE,{"disambiguationData":[TD([[makeQuery(id+"F6.imprint","IMPRINT",EDGE,{"derivedFrom":sQuery(id+"F6.wireOp",EDGE,"E35.18.11.2")}),-1.0]])]});
            var Q71;
            {var subQ5=sQuery(id+"F6.wireOp",EDGE,"E35.24.11.3");Q71=makeQuery(id+"F6.imprint","IMPRINT",FACE,{"disambiguationData":[TD([[makeQuery(id+"F6.imprint","IMPRINT",EDGE,{"derivedFrom":subQ5}),-1.0]])]});}
            var Q72;
            {var subQ0=sQuery(id+"F6.wireOp",EDGE,"E35.6.12.0");Q72=makeQuery(id+"F6.imprint","IMPRINT",FACE,{"disambiguationData":[TD([[makeQuery(id+"F6.imprint","IMPRINT",EDGE,{"derivedFrom":subQ0}),-1.0]])]});}
            var Q73;
            Q73=makeQuery(id+"F6.imprint","IMPRINT",FACE,{"disambiguationData":[TD([[makeQuery(id+"F6.imprint","IMPRINT",EDGE,{"derivedFrom":sQuery(id+"F6.wireOp",EDGE,"E35.0.12.1")}),-1.0]])]});
            var Q74;
            Q74=makeQuery(id+"F6.imprint","IMPRINT",FACE,{"disambiguationData":[TD([[makeQuery(id+"F6.imprint","IMPRINT",EDGE,{"derivedFrom":sQuery(id+"F6.wireOp",EDGE,"E35.0.12.2")}),-1.0]])]});
            var Q75;
            Q75=makeQuery(id+"F6.imprint","IMPRINT",FACE,{"disambiguationData":[TD([[makeQuery(id+"F6.imprint","IMPRINT",EDGE,{"derivedFrom":sQuery(id+"F6.wireOp",EDGE,"E35.18.12.1")}),-1.0]])]});
            var Q76;
            Q76=makeQuery(id+"F6.imprint","IMPRINT",FACE,{"disambiguationData":[TD([[makeQuery(id+"F6.imprint","IMPRINT",EDGE,{"derivedFrom":sQuery(id+"F6.wireOp",EDGE,"E35.18.12.2")}),-1.0]])]});
            var Q77;
            {var subQ5=sQuery(id+"F6.wireOp",EDGE,"E35.24.12.3");Q77=makeQuery(id+"F6.imprint","IMPRINT",FACE,{"disambiguationData":[TD([[makeQuery(id+"F6.imprint","IMPRINT",EDGE,{"derivedFrom":subQ5}),-1.0]])]});}
            var Q78;
            {var subQ0=sQuery(id+"F6.wireOp",EDGE,"E35.6.13.0");Q78=makeQuery(id+"F6.imprint","IMPRINT",FACE,{"disambiguationData":[TD([[makeQuery(id+"F6.imprint","IMPRINT",EDGE,{"derivedFrom":subQ0}),-1.0]])]});}
            var Q79;
            Q79=makeQuery(id+"F6.imprint","IMPRINT",FACE,{"disambiguationData":[TD([[makeQuery(id+"F6.imprint","IMPRINT",EDGE,{"derivedFrom":sQuery(id+"F6.wireOp",EDGE,"E35.0.13.1")}),-1.0]])]});
            var Q80;
            Q80=makeQuery(id+"F6.imprint","IMPRINT",FACE,{"disambiguationData":[TD([[makeQuery(id+"F6.imprint","IMPRINT",EDGE,{"derivedFrom":sQuery(id+"F6.wireOp",EDGE,"E35.0.13.2")}),-1.0]])]});
            var Q81;
            {var subQ5=sQuery(id+"F6.wireOp",EDGE,"E35.33.13.0");Q81=makeQuery(id+"F6.imprint","IMPRINT",FACE,{"disambiguationData":[TD([[makeQuery(id+"F6.imprint","IMPRINT",EDGE,{"derivedFrom":subQ5}),-1.0]])]});}
            var Q82;
            Q82=makeQuery(id+"F6.imprint","IMPRINT",FACE,{"disambiguationData":[TD([[makeQuery(id+"F6.imprint","IMPRINT",EDGE,{"derivedFrom":sQuery(id+"F6.wireOp",EDGE,"E35.18.13.1")}),-1.0]])]});
            var Q83;
            Q83=makeQuery(id+"F6.imprint","IMPRINT",FACE,{"disambiguationData":[TD([[makeQuery(id+"F6.imprint","IMPRINT",EDGE,{"derivedFrom":sQuery(id+"F6.wireOp",EDGE,"E35.18.13.2")}),-1.0]])]});
            var Q84;
            {var subQ5=sQuery(id+"F6.wireOp",EDGE,"E35.24.13.3");Q84=makeQuery(id+"F6.imprint","IMPRINT",FACE,{"disambiguationData":[TD([[makeQuery(id+"F6.imprint","IMPRINT",EDGE,{"derivedFrom":subQ5}),-1.0]])]});}
            var Q85;
            {var subQ0=sQuery(id+"F6.wireOp",EDGE,"E35.6.14.0");Q85=makeQuery(id+"F6.imprint","IMPRINT",FACE,{"disambiguationData":[TD([[makeQuery(id+"F6.imprint","IMPRINT",EDGE,{"derivedFrom":subQ0}),-1.0]])]});}
            var Q86;
            Q86=makeQuery(id+"F6.imprint","IMPRINT",FACE,{"disambiguationData":[TD([[makeQuery(id+"F6.imprint","IMPRINT",EDGE,{"derivedFrom":sQuery(id+"F6.wireOp",EDGE,"E35.0.14.1")}),-1.0]])]});
            var Q87;
            Q87=makeQuery(id+"F6.imprint","IMPRINT",FACE,{"disambiguationData":[TD([[makeQuery(id+"F6.imprint","IMPRINT",EDGE,{"derivedFrom":sQuery(id+"F6.wireOp",EDGE,"E35.0.14.2")}),-1.0]])]});
            var Q88;
            {var subQ5=sQuery(id+"F6.wireOp",EDGE,"E35.33.14.0");Q88=makeQuery(id+"F6.imprint","IMPRINT",FACE,{"disambiguationData":[TD([[makeQuery(id+"F6.imprint","IMPRINT",EDGE,{"derivedFrom":subQ5}),-1.0]])]});}
            var Q89;
            Q89=makeQuery(id+"F6.imprint","IMPRINT",FACE,{"disambiguationData":[TD([[makeQuery(id+"F6.imprint","IMPRINT",EDGE,{"derivedFrom":sQuery(id+"F6.wireOp",EDGE,"E35.18.14.1")}),-1.0]])]});
            var Q90;
            Q90=makeQuery(id+"F6.imprint","IMPRINT",FACE,{"disambiguationData":[TD([[makeQuery(id+"F6.imprint","IMPRINT",EDGE,{"derivedFrom":sQuery(id+"F6.wireOp",EDGE,"E35.18.14.2")}),-1.0]])]});
            var Q91;
            {var subQ5=sQuery(id+"F6.wireOp",EDGE,"E35.24.14.3");Q91=makeQuery(id+"F6.imprint","IMPRINT",FACE,{"disambiguationData":[TD([[makeQuery(id+"F6.imprint","IMPRINT",EDGE,{"derivedFrom":subQ5}),-1.0]])]});}
            var Q92;
            {var subQ0=sQuery(id+"F6.wireOp",EDGE,"E35.6.15.0");Q92=makeQuery(id+"F6.imprint","IMPRINT",FACE,{"disambiguationData":[TD([[makeQuery(id+"F6.imprint","IMPRINT",EDGE,{"derivedFrom":subQ0}),-1.0]])]});}
            var Q93;
            Q93=makeQuery(id+"F6.imprint","IMPRINT",FACE,{"disambiguationData":[TD([[makeQuery(id+"F6.imprint","IMPRINT",EDGE,{"derivedFrom":sQuery(id+"F6.wireOp",EDGE,"E35.0.15.1")}),-1.0]])]});
            var Q94;
            Q94=makeQuery(id+"F6.imprint","IMPRINT",FACE,{"disambiguationData":[TD([[makeQuery(id+"F6.imprint","IMPRINT",EDGE,{"derivedFrom":sQuery(id+"F6.wireOp",EDGE,"E35.0.15.2")}),-1.0]])]});
            var Q95;
            {var subQ5=sQuery(id+"F6.wireOp",EDGE,"E35.33.15.0");Q95=makeQuery(id+"F6.imprint","IMPRINT",FACE,{"disambiguationData":[TD([[makeQuery(id+"F6.imprint","IMPRINT",EDGE,{"derivedFrom":subQ5}),-1.0]])]});}
            var Q96;
            Q96=makeQuery(id+"F6.imprint","IMPRINT",FACE,{"disambiguationData":[TD([[makeQuery(id+"F6.imprint","IMPRINT",EDGE,{"derivedFrom":sQuery(id+"F6.wireOp",EDGE,"E35.18.15.1")}),-1.0]])]});
            var Q97;
            Q97=makeQuery(id+"F6.imprint","IMPRINT",FACE,{"disambiguationData":[TD([[makeQuery(id+"F6.imprint","IMPRINT",EDGE,{"derivedFrom":sQuery(id+"F6.wireOp",EDGE,"E35.18.15.2")}),-1.0]])]});
            var Q98;
            {var subQ5=sQuery(id+"F6.wireOp",EDGE,"E35.24.15.3");Q98=makeQuery(id+"F6.imprint","IMPRINT",FACE,{"disambiguationData":[TD([[makeQuery(id+"F6.imprint","IMPRINT",EDGE,{"derivedFrom":subQ5}),-1.0]])]});}
            var Q99;
            {var subQ6=sQuery(id+"F6.wireOp",EDGE,"E29.2");Q99=makeQuery(id+"F6.imprint","IMPRINT",FACE,{"disambiguationData":[TD([[makeQuery(id+"F6.imprint","IMPRINT",EDGE,{"derivedFrom":subQ6}),-1.0]])]});}
            var Q100;
            {var subQ1=sQuery(id+"F6.wireOp",EDGE,"E31.2.0.7");Q100=makeQuery(id+"F6.imprint","IMPRINT",FACE,{"disambiguationData":[TD([[makeQuery(id+"F6.imprint","IMPRINT",EDGE,{"derivedFrom":subQ1}),-1.0]])]});}
            var Q101;
            {var subQ1=sQuery(id+"F6.wireOp",EDGE,"E34.21.3.0");Q101=makeQuery(id+"F6.imprint","IMPRINT",FACE,{"disambiguationData":[TD([[makeQuery(id+"F6.imprint","IMPRINT",EDGE,{"derivedFrom":subQ1}),-1.0]])]});}
            var Q102;
            Q102=makeQuery(id+"F3.opSweep","SWEPT_FACE",FACE,{"disambiguationData":[OSD([sQuery(id+"F0.wireOp",EDGE,"E0.bottom"),sQuery(id+"F2.wireOp",EDGE,"E7.right")])]});
            extrude(context, id + "F7", {"entities" : qUnion([Q0, Q1, Q2, Q3, Q4, Q5, Q6, Q7, Q8, Q9, Q10, Q11, Q12, Q13, Q14, Q15, Q16, Q17, Q18, Q19, Q20, Q21, Q22, Q23, Q24, Q25, Q26, Q27, Q28, Q29, Q30, Q31, Q32, Q33, Q34, Q35, Q36, Q37, Q38, Q39, Q40, Q41, Q42, Q43, Q44, Q45, Q46, Q47, Q48, Q49, Q50, Q51, Q52, Q53, Q54, Q55, Q56, Q57, Q58, Q59, Q60, Q61, Q62, Q63, Q64, Q65, Q66, Q67, Q68, Q69, Q70, Q71, Q72, Q73, Q74, Q75, Q76, Q77, Q78, Q79, Q80, Q81, Q82, Q83, Q84, Q85, Q86, Q87, Q88, Q89, Q90, Q91, Q92, Q93, Q94, Q95, Q96, Q97, Q98, Q99, Q100, Q101]), "operationType" : NewBodyOperationType.REMOVE, "endBound" : BoundingType.UP_TO_SURFACE, "oppositeDirection" : true, "depth" : 25 * mm, "endBoundEntityFace" : qUnion([Q102]), "offsetDistance" : 25 * mm});
        }
    });
